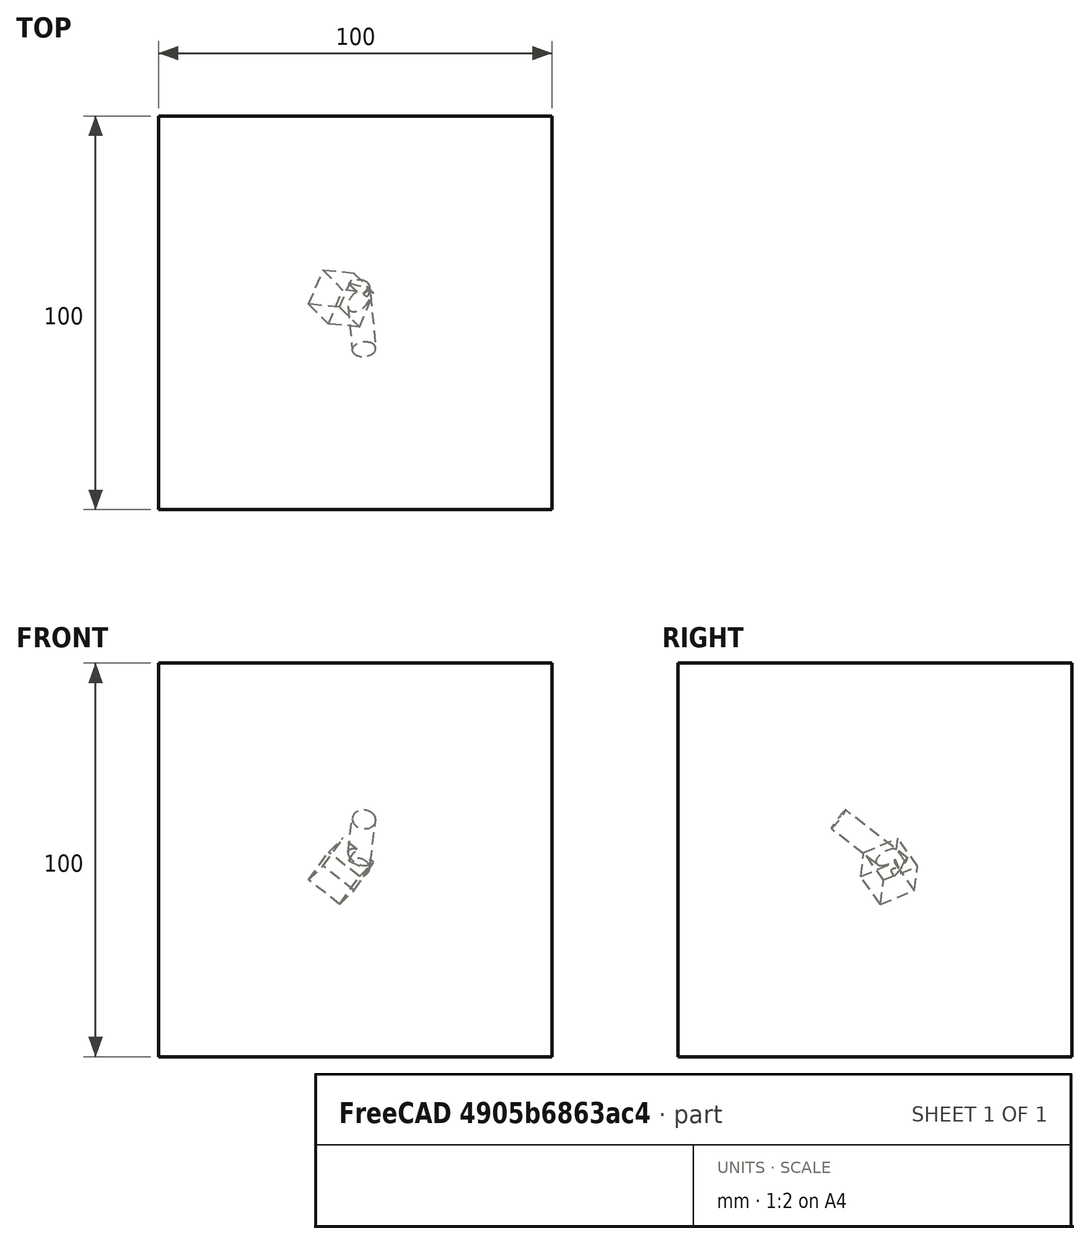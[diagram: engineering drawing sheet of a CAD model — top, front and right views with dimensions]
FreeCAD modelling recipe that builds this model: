
FCSTD DOCUMENT  (FreeCAD 1.0R39109 (Git))
Label: UnionTest
License: All rights reserved
objects: App::DocumentObjectGroupPython×1251, Part::FeaturePython×3, App::Part×2, Part::Fuse×1
note: 4 computed .brp shape members not serialized (recipe doc carries the construction recipe); baked Part::Feature solids carry a one-line shape summary decoded from their .brp

FEATURE [App::DocumentObjectGroupPython] HALFPI  # scripted group (container) (typed FeaturePython)
  name = HALFPI
  value = pi/2.
FEATURE [App::DocumentObjectGroupPython] PI  # scripted group (container) (typed FeaturePython)
  name = PI
  value = 1.*pi
FEATURE [App::DocumentObjectGroupPython] TWOPI  # scripted group (container) (typed FeaturePython)
  name = TWOPI
  value = 2.*pi
FEATURE [App::DocumentObjectGroupPython] Constants  # scripted group (container) (typed FeaturePython)
  Group = -> [HALFPI,PI,TWOPI]
FEATURE [App::DocumentObjectGroupPython] Variables  # scripted group (container) (typed FeaturePython)
FEATURE [App::DocumentObjectGroupPython] Quantities  # scripted group (container) (typed FeaturePython)
FEATURE [App::DocumentObjectGroupPython] Isotopes  # scripted group (container) (typed FeaturePython)
FEATURE [App::DocumentObjectGroupPython] Elements  # scripted group (container) (typed FeaturePython)
FEATURE [App::DocumentObjectGroupPython] Matrix  # scripted group (container) (typed FeaturePython)
FEATURE [App::DocumentObjectGroupPython] Surfaces  # scripted group (container) (typed FeaturePython)
FEATURE [App::DocumentObjectGroupPython] Opticals  # scripted group (container) (typed FeaturePython)
  Group = -> [Matrix,Surfaces]
FEATURE [App::DocumentObjectGroupPython] G4Isotopes  # scripted group (container) (typed FeaturePython)
FEATURE [App::DocumentObjectGroupPython] H_element  # scripted group (container) (typed FeaturePython)
  Z = 1
  atom_value = 1.008
  formula = H
  name = H_element
FEATURE [App::DocumentObjectGroupPython] He_element  # scripted group (container) (typed FeaturePython)
  Z = 2
  atom_value = 4.0026
  formula = He
  name = He_element
FEATURE [App::DocumentObjectGroupPython] Li_element  # scripted group (container) (typed FeaturePython)
  Z = 3
  atom_value = 6.94
  formula = Li
  name = Li_element
FEATURE [App::DocumentObjectGroupPython] Be_element  # scripted group (container) (typed FeaturePython)
  Z = 4
  atom_value = 9.01218
  formula = Be
  name = Be_element
FEATURE [App::DocumentObjectGroupPython] B_element  # scripted group (container) (typed FeaturePython)
  Z = 5
  atom_value = 10.81
  formula = B
  name = B_element
FEATURE [App::DocumentObjectGroupPython] C_element  # scripted group (container) (typed FeaturePython)
  Z = 6
  atom_value = 12.011
  formula = C
  name = C_element
FEATURE [App::DocumentObjectGroupPython] N_element  # scripted group (container) (typed FeaturePython)
  Z = 7
  atom_value = 14.007
  formula = N
  name = N_element
FEATURE [App::DocumentObjectGroupPython] O_element  # scripted group (container) (typed FeaturePython)
  Z = 8
  atom_value = 15.999
  formula = O
  name = O_element
FEATURE [App::DocumentObjectGroupPython] F_element  # scripted group (container) (typed FeaturePython)
  Z = 9
  atom_value = 18.9984
  formula = F
  name = F_element
FEATURE [App::DocumentObjectGroupPython] Ne_element  # scripted group (container) (typed FeaturePython)
  Z = 10
  atom_value = 20.1797
  formula = Ne
  name = Ne_element
FEATURE [App::DocumentObjectGroupPython] Na_element  # scripted group (container) (typed FeaturePython)
  Z = 11
  atom_value = 22.9898
  formula = Na
  name = Na_element
FEATURE [App::DocumentObjectGroupPython] Mg_element  # scripted group (container) (typed FeaturePython)
  Z = 12
  atom_value = 24.305
  formula = Mg
  name = Mg_element
FEATURE [App::DocumentObjectGroupPython] Al_element  # scripted group (container) (typed FeaturePython)
  Z = 13
  atom_value = 26.9815
  formula = Al
  name = Al_element
FEATURE [App::DocumentObjectGroupPython] Si_element  # scripted group (container) (typed FeaturePython)
  Z = 14
  atom_value = 28.085
  formula = Si
  name = Si_element
FEATURE [App::DocumentObjectGroupPython] P_element  # scripted group (container) (typed FeaturePython)
  Z = 15
  atom_value = 30.9738
  formula = P
  name = P_element
FEATURE [App::DocumentObjectGroupPython] S_element  # scripted group (container) (typed FeaturePython)
  Z = 16
  atom_value = 32.06
  formula = S
  name = S_element
FEATURE [App::DocumentObjectGroupPython] Cl_element  # scripted group (container) (typed FeaturePython)
  Z = 17
  atom_value = 35.45
  formula = Cl
  name = Cl_element
FEATURE [App::DocumentObjectGroupPython] Ar_element  # scripted group (container) (typed FeaturePython)
  Z = 18
  atom_value = 39.95
  formula = Ar
  name = Ar_element
FEATURE [App::DocumentObjectGroupPython] K_element  # scripted group (container) (typed FeaturePython)
  Z = 19
  atom_value = 39.0983
  formula = K
  name = K_element
FEATURE [App::DocumentObjectGroupPython] Ca_element  # scripted group (container) (typed FeaturePython)
  Z = 20
  atom_value = 40.078
  formula = Ca
  name = Ca_element
FEATURE [App::DocumentObjectGroupPython] Sc_element  # scripted group (container) (typed FeaturePython)
  Z = 21
  atom_value = 44.9559
  formula = Sc
  name = Sc_element
FEATURE [App::DocumentObjectGroupPython] Ti_element  # scripted group (container) (typed FeaturePython)
  Z = 22
  atom_value = 47.867
  formula = Ti
  name = Ti_element
FEATURE [App::DocumentObjectGroupPython] V_element  # scripted group (container) (typed FeaturePython)
  Z = 23
  atom_value = 50.9415
  formula = V
  name = V_element
FEATURE [App::DocumentObjectGroupPython] Cr_element  # scripted group (container) (typed FeaturePython)
  Z = 24
  atom_value = 51.9961
  formula = Cr
  name = Cr_element
FEATURE [App::DocumentObjectGroupPython] Mn_element  # scripted group (container) (typed FeaturePython)
  Z = 25
  atom_value = 54.938
  formula = Mn
  name = Mn_element
FEATURE [App::DocumentObjectGroupPython] Fe_element  # scripted group (container) (typed FeaturePython)
  Z = 26
  atom_value = 55.845
  formula = Fe
  name = Fe_element
FEATURE [App::DocumentObjectGroupPython] Co_element  # scripted group (container) (typed FeaturePython)
  Z = 27
  atom_value = 58.9332
  formula = Co
  name = Co_element
FEATURE [App::DocumentObjectGroupPython] Ni_element  # scripted group (container) (typed FeaturePython)
  Z = 28
  atom_value = 58.6934
  formula = Ni
  name = Ni_element
FEATURE [App::DocumentObjectGroupPython] Cu_element  # scripted group (container) (typed FeaturePython)
  Z = 29
  atom_value = 63.546
  formula = Cu
  name = Cu_element
FEATURE [App::DocumentObjectGroupPython] Zn_element  # scripted group (container) (typed FeaturePython)
  Z = 30
  atom_value = 65.38
  formula = Zn
  name = Zn_element
FEATURE [App::DocumentObjectGroupPython] Ga_element  # scripted group (container) (typed FeaturePython)
  Z = 31
  atom_value = 69.723
  formula = Ga
  name = Ga_element
FEATURE [App::DocumentObjectGroupPython] Ge_element  # scripted group (container) (typed FeaturePython)
  Z = 32
  atom_value = 72.63
  formula = Ge
  name = Ge_element
FEATURE [App::DocumentObjectGroupPython] As_element  # scripted group (container) (typed FeaturePython)
  Z = 33
  atom_value = 74.9216
  formula = As
  name = As_element
FEATURE [App::DocumentObjectGroupPython] Se_element  # scripted group (container) (typed FeaturePython)
  Z = 34
  atom_value = 78.971
  formula = Se
  name = Se_element
FEATURE [App::DocumentObjectGroupPython] Br_element  # scripted group (container) (typed FeaturePython)
  Z = 35
  atom_value = 79.904
  formula = Br
  name = Br_element
FEATURE [App::DocumentObjectGroupPython] Kr_element  # scripted group (container) (typed FeaturePython)
  Z = 36
  atom_value = 83.798
  formula = Kr
  name = Kr_element
FEATURE [App::DocumentObjectGroupPython] Rb_element  # scripted group (container) (typed FeaturePython)
  Z = 37
  atom_value = 85.4678
  formula = Rb
  name = Rb_element
FEATURE [App::DocumentObjectGroupPython] Sr_element  # scripted group (container) (typed FeaturePython)
  Z = 38
  atom_value = 87.62
  formula = Sr
  name = Sr_element
FEATURE [App::DocumentObjectGroupPython] Y_element  # scripted group (container) (typed FeaturePython)
  Z = 39
  atom_value = 88.9058
  formula = Y
  name = Y_element
FEATURE [App::DocumentObjectGroupPython] Zr_element  # scripted group (container) (typed FeaturePython)
  Z = 40
  atom_value = 91.224
  formula = Zr
  name = Zr_element
FEATURE [App::DocumentObjectGroupPython] Nb_element  # scripted group (container) (typed FeaturePython)
  Z = 41
  atom_value = 92.9064
  formula = Nb
  name = Nb_element
FEATURE [App::DocumentObjectGroupPython] Mo_element  # scripted group (container) (typed FeaturePython)
  Z = 42
  atom_value = 95.95
  formula = Mo
  name = Mo_element
FEATURE [App::DocumentObjectGroupPython] Tc_element  # scripted group (container) (typed FeaturePython)
  Z = 43
  atom_value = 97
  formula = Tc
  name = Tc_element
FEATURE [App::DocumentObjectGroupPython] Ru_element  # scripted group (container) (typed FeaturePython)
  Z = 44
  atom_value = 101.07
  formula = Ru
  name = Ru_element
FEATURE [App::DocumentObjectGroupPython] Rh_element  # scripted group (container) (typed FeaturePython)
  Z = 45
  atom_value = 102.905
  formula = Rh
  name = Rh_element
FEATURE [App::DocumentObjectGroupPython] Pd_element  # scripted group (container) (typed FeaturePython)
  Z = 46
  atom_value = 106.42
  formula = Pd
  name = Pd_element
FEATURE [App::DocumentObjectGroupPython] Ag_element  # scripted group (container) (typed FeaturePython)
  Z = 47
  atom_value = 107.868
  formula = Ag
  name = Ag_element
FEATURE [App::DocumentObjectGroupPython] Cd_element  # scripted group (container) (typed FeaturePython)
  Z = 48
  atom_value = 112.414
  formula = Cd
  name = Cd_element
FEATURE [App::DocumentObjectGroupPython] In_element  # scripted group (container) (typed FeaturePython)
  Z = 49
  atom_value = 114.818
  formula = In
  name = In_element
FEATURE [App::DocumentObjectGroupPython] Sn_element  # scripted group (container) (typed FeaturePython)
  Z = 50
  atom_value = 118.71
  formula = Sn
  name = Sn_element
FEATURE [App::DocumentObjectGroupPython] Sb_element  # scripted group (container) (typed FeaturePython)
  Z = 51
  atom_value = 121.76
  formula = Sb
  name = Sb_element
FEATURE [App::DocumentObjectGroupPython] Te_element  # scripted group (container) (typed FeaturePython)
  Z = 52
  atom_value = 127.6
  formula = Te
  name = Te_element
FEATURE [App::DocumentObjectGroupPython] I_element  # scripted group (container) (typed FeaturePython)
  Z = 53
  atom_value = 126.904
  formula = I
  name = I_element
FEATURE [App::DocumentObjectGroupPython] Xe_element  # scripted group (container) (typed FeaturePython)
  Z = 54
  atom_value = 131.293
  formula = Xe
  name = Xe_element
FEATURE [App::DocumentObjectGroupPython] Cs_element  # scripted group (container) (typed FeaturePython)
  Z = 55
  atom_value = 132.905
  formula = Cs
  name = Cs_element
FEATURE [App::DocumentObjectGroupPython] Ba_element  # scripted group (container) (typed FeaturePython)
  Z = 56
  atom_value = 137.327
  formula = Ba
  name = Ba_element
FEATURE [App::DocumentObjectGroupPython] La_element  # scripted group (container) (typed FeaturePython)
  Z = 57
  atom_value = 138.905
  formula = La
  name = La_element
FEATURE [App::DocumentObjectGroupPython] Ce_element  # scripted group (container) (typed FeaturePython)
  Z = 58
  atom_value = 140.116
  formula = Ce
  name = Ce_element
FEATURE [App::DocumentObjectGroupPython] Pr_element  # scripted group (container) (typed FeaturePython)
  Z = 59
  atom_value = 140.908
  formula = Pr
  name = Pr_element
FEATURE [App::DocumentObjectGroupPython] Nd_element  # scripted group (container) (typed FeaturePython)
  Z = 60
  atom_value = 144.242
  formula = Nd
  name = Nd_element
FEATURE [App::DocumentObjectGroupPython] Pm_element  # scripted group (container) (typed FeaturePython)
  Z = 61
  atom_value = 145
  formula = Pm
  name = Pm_element
FEATURE [App::DocumentObjectGroupPython] Sm_element  # scripted group (container) (typed FeaturePython)
  Z = 62
  atom_value = 150.36
  formula = Sm
  name = Sm_element
FEATURE [App::DocumentObjectGroupPython] Eu_element  # scripted group (container) (typed FeaturePython)
  Z = 63
  atom_value = 151.964
  formula = Eu
  name = Eu_element
FEATURE [App::DocumentObjectGroupPython] Gd_element  # scripted group (container) (typed FeaturePython)
  Z = 64
  atom_value = 157.25
  formula = Gd
  name = Gd_element
FEATURE [App::DocumentObjectGroupPython] Tb_element  # scripted group (container) (typed FeaturePython)
  Z = 65
  atom_value = 158.925
  formula = Tb
  name = Tb_element
FEATURE [App::DocumentObjectGroupPython] Dy_element  # scripted group (container) (typed FeaturePython)
  Z = 66
  atom_value = 162.5
  formula = Dy
  name = Dy_element
FEATURE [App::DocumentObjectGroupPython] Ho_element  # scripted group (container) (typed FeaturePython)
  Z = 67
  atom_value = 164.93
  formula = Ho
  name = Ho_element
FEATURE [App::DocumentObjectGroupPython] Er_element  # scripted group (container) (typed FeaturePython)
  Z = 68
  atom_value = 167.259
  formula = Er
  name = Er_element
FEATURE [App::DocumentObjectGroupPython] Tm_element  # scripted group (container) (typed FeaturePython)
  Z = 69
  atom_value = 168.934
  formula = Tm
  name = Tm_element
FEATURE [App::DocumentObjectGroupPython] Yb_element  # scripted group (container) (typed FeaturePython)
  Z = 70
  atom_value = 173.045
  formula = Yb
  name = Yb_element
FEATURE [App::DocumentObjectGroupPython] Lu_element  # scripted group (container) (typed FeaturePython)
  Z = 71
  atom_value = 174.967
  formula = Lu
  name = Lu_element
FEATURE [App::DocumentObjectGroupPython] Hf_element  # scripted group (container) (typed FeaturePython)
  Z = 72
  atom_value = 178.49
  formula = Hf
  name = Hf_element
FEATURE [App::DocumentObjectGroupPython] Ta_element  # scripted group (container) (typed FeaturePython)
  Z = 73
  atom_value = 180.948
  formula = Ta
  name = Ta_element
FEATURE [App::DocumentObjectGroupPython] W_element  # scripted group (container) (typed FeaturePython)
  Z = 74
  atom_value = 183.84
  formula = W
  name = W_element
FEATURE [App::DocumentObjectGroupPython] Re_element  # scripted group (container) (typed FeaturePython)
  Z = 75
  atom_value = 186.207
  formula = Re
  name = Re_element
FEATURE [App::DocumentObjectGroupPython] Os_element  # scripted group (container) (typed FeaturePython)
  Z = 76
  atom_value = 190.23
  formula = Os
  name = Os_element
FEATURE [App::DocumentObjectGroupPython] Ir_element  # scripted group (container) (typed FeaturePython)
  Z = 77
  atom_value = 192.217
  formula = Ir
  name = Ir_element
FEATURE [App::DocumentObjectGroupPython] Pt_element  # scripted group (container) (typed FeaturePython)
  Z = 78
  atom_value = 195.084
  formula = Pt
  name = Pt_element
FEATURE [App::DocumentObjectGroupPython] Au_element  # scripted group (container) (typed FeaturePython)
  Z = 79
  atom_value = 196.967
  formula = Au
  name = Au_element
FEATURE [App::DocumentObjectGroupPython] Hg_element  # scripted group (container) (typed FeaturePython)
  Z = 80
  atom_value = 200.592
  formula = Hg
  name = Hg_element
FEATURE [App::DocumentObjectGroupPython] Tl_element  # scripted group (container) (typed FeaturePython)
  Z = 81
  atom_value = 204.38
  formula = Tl
  name = Tl_element
FEATURE [App::DocumentObjectGroupPython] Pb_element  # scripted group (container) (typed FeaturePython)
  Z = 82
  atom_value = 207.2
  formula = Pb
  name = Pb_element
FEATURE [App::DocumentObjectGroupPython] Bi_element  # scripted group (container) (typed FeaturePython)
  Z = 83
  atom_value = 208.98
  formula = Bi
  name = Bi_element
FEATURE [App::DocumentObjectGroupPython] Po_element  # scripted group (container) (typed FeaturePython)
  Z = 84
  atom_value = 209
  formula = Po
  name = Po_element
FEATURE [App::DocumentObjectGroupPython] At_element  # scripted group (container) (typed FeaturePython)
  Z = 85
  atom_value = 210
  formula = At
  name = At_element
FEATURE [App::DocumentObjectGroupPython] Rn_element  # scripted group (container) (typed FeaturePython)
  Z = 86
  atom_value = 222
  formula = Rn
  name = Rn_element
FEATURE [App::DocumentObjectGroupPython] Fr_element  # scripted group (container) (typed FeaturePython)
  Z = 87
  atom_value = 223
  formula = Fr
  name = Fr_element
FEATURE [App::DocumentObjectGroupPython] Ra_element  # scripted group (container) (typed FeaturePython)
  Z = 88
  atom_value = 226
  formula = Ra
  name = Ra_element
FEATURE [App::DocumentObjectGroupPython] Ac_element  # scripted group (container) (typed FeaturePython)
  Z = 89
  atom_value = 227
  formula = Ac
  name = Ac_element
FEATURE [App::DocumentObjectGroupPython] Th_element  # scripted group (container) (typed FeaturePython)
  Z = 90
  atom_value = 232.038
  formula = Th
  name = Th_element
FEATURE [App::DocumentObjectGroupPython] Pa_element  # scripted group (container) (typed FeaturePython)
  Z = 91
  atom_value = 231.036
  formula = Pa
  name = Pa_element
FEATURE [App::DocumentObjectGroupPython] U_element  # scripted group (container) (typed FeaturePython)
  Z = 92
  atom_value = 238.029
  formula = U
  name = U_element
FEATURE [App::DocumentObjectGroupPython] Np_element  # scripted group (container) (typed FeaturePython)
  Z = 93
  atom_value = 237
  formula = Np
  name = Np_element
FEATURE [App::DocumentObjectGroupPython] Pu_element  # scripted group (container) (typed FeaturePython)
  Z = 94
  atom_value = 244
  formula = Pu
  name = Pu_element
FEATURE [App::DocumentObjectGroupPython] Am_element  # scripted group (container) (typed FeaturePython)
  Z = 95
  atom_value = 243
  formula = Am
  name = Am_element
FEATURE [App::DocumentObjectGroupPython] Cm_element  # scripted group (container) (typed FeaturePython)
  Z = 96
  atom_value = 247
  formula = Cm
  name = Cm_element
FEATURE [App::DocumentObjectGroupPython] Bk_element  # scripted group (container) (typed FeaturePython)
  Z = 97
  atom_value = 247
  formula = Bk
  name = Bk_element
FEATURE [App::DocumentObjectGroupPython] Cf_element  # scripted group (container) (typed FeaturePython)
  Z = 98
  atom_value = 251
  formula = Cf
  name = Cf_element
FEATURE [App::DocumentObjectGroupPython] G4Elements  # scripted group (container) (typed FeaturePython)
  Group = -> [H_element,He_element,Li_element,Be_element,B_element,C_element,N_element,O_element,F_element,Ne_element,Na_element,Mg_element,Al_element,Si_element,P_element,S_element,Cl_element,Ar_element,K_element,Ca_element,Sc_element,Ti_element,V_element,Cr_element,Mn_element,Fe_element,Co_element,Ni_element,Cu_element,Zn_element,Ga_element,Ge_element,As_element,Se_element,Br_element,Kr_element,Rb_element,+61 more]
FEATURE [App::DocumentObjectGroupPython] H_element001  label="H_element : 0.101"  # scripted group (container) (typed FeaturePython)
  n = 0.101327
FEATURE [App::DocumentObjectGroupPython] C_element001  label="C_element : 0.775"  # scripted group (container) (typed FeaturePython)
  n = 0.7755
FEATURE [App::DocumentObjectGroupPython] N_element001  label="N_element : 0.035"  # scripted group (container) (typed FeaturePython)
  n = 0.035057
FEATURE [App::DocumentObjectGroupPython] O_element001  label="O_element : 0.052"  # scripted group (container) (typed FeaturePython)
  n = 0.0523159
FEATURE [App::DocumentObjectGroupPython] F_element001  label="F_element : 0.017"  # scripted group (container) (typed FeaturePython)
  n = 0.017422
FEATURE [App::DocumentObjectGroupPython] Ca_element001  label="Ca_element : 0.018"  # scripted group (container) (typed FeaturePython)
  n = 0.018378
FEATURE [App::DocumentObjectGroupPython] G4_A_150_TISSUE  label="G4_A-150_TISSUE"  # scripted group (container) (typed FeaturePython)
  Dunit = g/cm3
  Dvalue = 1.127
  Group = -> [H_element001,C_element001,N_element001,O_element001,F_element001,Ca_element001]
  conduct = 2
  density = 1
  expand = 3
  formula = G4_A-150_TISSUE
  name = G4_A-150_TISSUE
  specific = 4
FEATURE [App::DocumentObjectGroupPython] C_element002  label="C_element : 3"  # scripted group (container) (typed FeaturePython)
  n = 3
  ref = C_element
FEATURE [App::DocumentObjectGroupPython] H_element002  label="H_element : 6"  # scripted group (container) (typed FeaturePython)
  n = 6
  ref = H_element
FEATURE [App::DocumentObjectGroupPython] O_element002  label="O_element : 1"  # scripted group (container) (typed FeaturePython)
  n = 1
  ref = O_element
FEATURE [App::DocumentObjectGroupPython] G4_ACETONE  # scripted group (container) (typed FeaturePython)
  Dunit = g/cm3
  Dvalue = 0.7899
  Group = -> [C_element002,H_element002,O_element002]
  conduct = 2
  density = 1
  expand = 3
  formula = G4_ACETONE
  name = G4_ACETONE
  specific = 4
FEATURE [App::DocumentObjectGroupPython] C_element003  label="C_element : 2"  # scripted group (container) (typed FeaturePython)
  n = 2
  ref = C_element
FEATURE [App::DocumentObjectGroupPython] H_element003  label="H_element : 2"  # scripted group (container) (typed FeaturePython)
  n = 2
  ref = H_element
FEATURE [App::DocumentObjectGroupPython] G4_ACETYLENE  # scripted group (container) (typed FeaturePython)
  Dunit = g/cm3
  Dvalue = 0.0010967
  Group = -> [C_element003,H_element003]
  conduct = 2
  density = 1
  expand = 3
  formula = G4_ACETYLENE
  name = G4_ACETYLENE
  specific = 4
FEATURE [App::DocumentObjectGroupPython] C_element004  label="C_element : 5"  # scripted group (container) (typed FeaturePython)
  n = 5
  ref = C_element
FEATURE [App::DocumentObjectGroupPython] H_element004  label="H_element : 5"  # scripted group (container) (typed FeaturePython)
  n = 5
  ref = H_element
FEATURE [App::DocumentObjectGroupPython] N_element002  label="N_element : 5"  # scripted group (container) (typed FeaturePython)
  n = 5
  ref = N_element
FEATURE [App::DocumentObjectGroupPython] G4_ADENINE  # scripted group (container) (typed FeaturePython)
  Dunit = g/cm3
  Dvalue = 1.6
  Group = -> [C_element004,H_element004,N_element002]
  conduct = 2
  density = 1
  expand = 3
  formula = G4_ADENINE
  name = G4_ADENINE
  specific = 4
FEATURE [App::DocumentObjectGroupPython] H_element005  label="H_element : 0.114"  # scripted group (container) (typed FeaturePython)
  n = 0.114
FEATURE [App::DocumentObjectGroupPython] C_element005  label="C_element : 0.598"  # scripted group (container) (typed FeaturePython)
  n = 0.598
FEATURE [App::DocumentObjectGroupPython] N_element003  label="N_element : 0.007"  # scripted group (container) (typed FeaturePython)
  n = 0.007
FEATURE [App::DocumentObjectGroupPython] O_element003  label="O_element : 0.278"  # scripted group (container) (typed FeaturePython)
  n = 0.278
FEATURE [App::DocumentObjectGroupPython] Na_element001  label="Na_element : 0.001"  # scripted group (container) (typed FeaturePython)
  n = 0.001
FEATURE [App::DocumentObjectGroupPython] S_element001  label="S_element : 0.001"  # scripted group (container) (typed FeaturePython)
  n = 0.001
FEATURE [App::DocumentObjectGroupPython] Cl_element001  label="Cl_element : 0.001"  # scripted group (container) (typed FeaturePython)
  n = 0.001
FEATURE [App::DocumentObjectGroupPython] G4_ADIPOSE_TISSUE_ICRP  # scripted group (container) (typed FeaturePython)
  Dunit = g/cm3
  Dvalue = 0.95
  Group = -> [H_element005,C_element005,N_element003,O_element003,Na_element001,S_element001,Cl_element001]
  conduct = 2
  density = 1
  expand = 3
  formula = G4_ADIPOSE_TISSUE_ICRP
  name = G4_ADIPOSE_TISSUE_ICRP
  specific = 4
FEATURE [App::DocumentObjectGroupPython] C_element006  label="C_element : 0.000"  # scripted group (container) (typed FeaturePython)
  n = 0.000124
FEATURE [App::DocumentObjectGroupPython] N_element004  label="N_element : 0.755"  # scripted group (container) (typed FeaturePython)
  n = 0.755268
FEATURE [App::DocumentObjectGroupPython] O_element004  label="O_element : 0.232"  # scripted group (container) (typed FeaturePython)
  n = 0.231781
FEATURE [App::DocumentObjectGroupPython] Ar_element001  label="Ar_element : 0.013"  # scripted group (container) (typed FeaturePython)
  n = 0.012827
FEATURE [App::DocumentObjectGroupPython] G4_AIR  # scripted group (container) (typed FeaturePython)
  Dunit = g/cm3
  Dvalue = 0.00120479
  Group = -> [C_element006,N_element004,O_element004,Ar_element001]
  conduct = 2
  density = 1
  expand = 3
  formula = G4_AIR
  name = G4_AIR
  specific = 4
FEATURE [App::DocumentObjectGroupPython] C_element007  label="C_element : 006"  # scripted group (container) (typed FeaturePython)
  n = 3
  ref = C_element
FEATURE [App::DocumentObjectGroupPython] H_element006  label="H_element : 7"  # scripted group (container) (typed FeaturePython)
  n = 7
  ref = H_element
FEATURE [App::DocumentObjectGroupPython] N_element005  label="N_element : 1"  # scripted group (container) (typed FeaturePython)
  n = 1
  ref = N_element
FEATURE [App::DocumentObjectGroupPython] O_element005  label="O_element : 2"  # scripted group (container) (typed FeaturePython)
  n = 2
  ref = O_element
FEATURE [App::DocumentObjectGroupPython] G4_ALANINE  # scripted group (container) (typed FeaturePython)
  Dunit = g/cm3
  Dvalue = 1.42
  Group = -> [C_element007,H_element006,N_element005,O_element005]
  conduct = 2
  density = 1
  expand = 3
  formula = G4_ALANINE
  name = G4_ALANINE
  specific = 4
FEATURE [App::DocumentObjectGroupPython] Al_element001  label="Al_element : 2"  # scripted group (container) (typed FeaturePython)
  n = 2
  ref = Al_element
FEATURE [App::DocumentObjectGroupPython] O_element006  label="O_element : 3"  # scripted group (container) (typed FeaturePython)
  n = 3
  ref = O_element
FEATURE [App::DocumentObjectGroupPython] G4_ALUMINUM_OXIDE  # scripted group (container) (typed FeaturePython)
  Dunit = g/cm3
  Dvalue = 3.97
  Group = -> [Al_element001,O_element006]
  conduct = 2
  density = 1
  expand = 3
  formula = G4_ALUMINUM_OXIDE
  name = G4_ALUMINUM_OXIDE
  specific = 4
FEATURE [App::DocumentObjectGroupPython] H_element007  label="H_element : 0.106"  # scripted group (container) (typed FeaturePython)
  n = 0.10593
FEATURE [App::DocumentObjectGroupPython] C_element008  label="C_element : 0.789"  # scripted group (container) (typed FeaturePython)
  n = 0.788974
FEATURE [App::DocumentObjectGroupPython] O_element007  label="O_element : 0.105"  # scripted group (container) (typed FeaturePython)
  n = 0.105096
FEATURE [App::DocumentObjectGroupPython] G4_AMBER  # scripted group (container) (typed FeaturePython)
  Dunit = g/cm3
  Dvalue = 1.1
  Group = -> [H_element007,C_element008,O_element007]
  conduct = 2
  density = 1
  expand = 3
  formula = G4_AMBER
  name = G4_AMBER
  specific = 4
FEATURE [App::DocumentObjectGroupPython] N_element006  label="N_element : 006"  # scripted group (container) (typed FeaturePython)
  n = 1
  ref = N_element
FEATURE [App::DocumentObjectGroupPython] H_element008  label="H_element : 3"  # scripted group (container) (typed FeaturePython)
  n = 3
  ref = H_element
FEATURE [App::DocumentObjectGroupPython] G4_AMMONIA  # scripted group (container) (typed FeaturePython)
  Dunit = g/cm3
  Dvalue = 0.000826019
  Group = -> [N_element006,H_element008]
  conduct = 2
  density = 1
  expand = 3
  formula = G4_AMMONIA
  name = G4_AMMONIA
  specific = 4
FEATURE [App::DocumentObjectGroupPython] C_element009  label="C_element : 6"  # scripted group (container) (typed FeaturePython)
  n = 6
  ref = C_element
FEATURE [App::DocumentObjectGroupPython] H_element009  label="H_element : 008"  # scripted group (container) (typed FeaturePython)
  n = 7
  ref = H_element
FEATURE [App::DocumentObjectGroupPython] N_element007  label="N_element : 007"  # scripted group (container) (typed FeaturePython)
  n = 1
  ref = N_element
FEATURE [App::DocumentObjectGroupPython] G4_ANILINE  # scripted group (container) (typed FeaturePython)
  Dunit = g/cm3
  Dvalue = 1.0235
  Group = -> [C_element009,H_element009,N_element007]
  conduct = 2
  density = 1
  expand = 3
  formula = G4_ANILINE
  name = G4_ANILINE
  specific = 4
FEATURE [App::DocumentObjectGroupPython] C_element010  label="C_element : 14"  # scripted group (container) (typed FeaturePython)
  n = 14
  ref = C_element
FEATURE [App::DocumentObjectGroupPython] H_element010  label="H_element : 10"  # scripted group (container) (typed FeaturePython)
  n = 10
  ref = H_element
FEATURE [App::DocumentObjectGroupPython] G4_ANTHRACENE  # scripted group (container) (typed FeaturePython)
  Dunit = g/cm3
  Dvalue = 1.283
  Group = -> [C_element010,H_element010]
  conduct = 2
  density = 1
  expand = 3
  formula = G4_ANTHRACENE
  name = G4_ANTHRACENE
  specific = 4
FEATURE [App::DocumentObjectGroupPython] H_element011  label="H_element : 0.065"  # scripted group (container) (typed FeaturePython)
  n = 0.0654709
FEATURE [App::DocumentObjectGroupPython] C_element011  label="C_element : 0.537"  # scripted group (container) (typed FeaturePython)
  n = 0.536944
FEATURE [App::DocumentObjectGroupPython] N_element008  label="N_element : 0.021"  # scripted group (container) (typed FeaturePython)
  n = 0.0215
FEATURE [App::DocumentObjectGroupPython] O_element008  label="O_element : 0.032"  # scripted group (container) (typed FeaturePython)
  n = 0.032085
FEATURE [App::DocumentObjectGroupPython] F_element002  label="F_element : 0.167"  # scripted group (container) (typed FeaturePython)
  n = 0.167411
FEATURE [App::DocumentObjectGroupPython] Ca_element002  label="Ca_element : 0.177"  # scripted group (container) (typed FeaturePython)
  n = 0.176589
FEATURE [App::DocumentObjectGroupPython] G4_B_100_BONE  label="G4_B-100_BONE"  # scripted group (container) (typed FeaturePython)
  Dunit = g/cm3
  Dvalue = 1.45
  Group = -> [H_element011,C_element011,N_element008,O_element008,F_element002,Ca_element002]
  conduct = 2
  density = 1
  expand = 3
  formula = G4_B-100_BONE
  name = G4_B-100_BONE
  specific = 4
FEATURE [App::DocumentObjectGroupPython] H_element012  label="H_element : 0.057"  # scripted group (container) (typed FeaturePython)
  n = 0.057441
FEATURE [App::DocumentObjectGroupPython] C_element012  label="C_element : 0.790"  # scripted group (container) (typed FeaturePython)
  n = 0.774591
FEATURE [App::DocumentObjectGroupPython] O_element009  label="O_element : 0.168"  # scripted group (container) (typed FeaturePython)
  n = 0.167968
FEATURE [App::DocumentObjectGroupPython] G4_BAKELITE  # scripted group (container) (typed FeaturePython)
  Dunit = g/cm3
  Dvalue = 1.25
  Group = -> [H_element012,C_element012,O_element009]
  conduct = 2
  density = 1
  expand = 3
  formula = G4_BAKELITE
  name = G4_BAKELITE
  specific = 4
FEATURE [App::DocumentObjectGroupPython] Ba_element001  label="Ba_element : 1"  # scripted group (container) (typed FeaturePython)
  n = 1
  ref = Ba_element
FEATURE [App::DocumentObjectGroupPython] F_element003  label="F_element : 2"  # scripted group (container) (typed FeaturePython)
  n = 2
  ref = F_element
FEATURE [App::DocumentObjectGroupPython] G4_BARIUM_FLUORIDE  # scripted group (container) (typed FeaturePython)
  Dunit = g/cm3
  Dvalue = 4.89
  Group = -> [Ba_element001,F_element003]
  conduct = 2
  density = 1
  expand = 3
  formula = G4_BARIUM_FLUORIDE
  name = G4_BARIUM_FLUORIDE
  specific = 4
FEATURE [App::DocumentObjectGroupPython] Ba_element002  label="Ba_element : 002"  # scripted group (container) (typed FeaturePython)
  n = 1
  ref = Ba_element
FEATURE [App::DocumentObjectGroupPython] S_element002  label="S_element : 1"  # scripted group (container) (typed FeaturePython)
  n = 1
  ref = S_element
FEATURE [App::DocumentObjectGroupPython] O_element010  label="O_element : 4"  # scripted group (container) (typed FeaturePython)
  n = 4
  ref = O_element
FEATURE [App::DocumentObjectGroupPython] G4_BARIUM_SULFATE  # scripted group (container) (typed FeaturePython)
  Dunit = g/cm3
  Dvalue = 4.5
  Group = -> [Ba_element002,S_element002,O_element010]
  conduct = 2
  density = 1
  expand = 3
  formula = G4_BARIUM_SULFATE
  name = G4_BARIUM_SULFATE
  specific = 4
FEATURE [App::DocumentObjectGroupPython] C_element013  label="C_element : 007"  # scripted group (container) (typed FeaturePython)
  n = 6
  ref = C_element
FEATURE [App::DocumentObjectGroupPython] H_element013  label="H_element : 009"  # scripted group (container) (typed FeaturePython)
  n = 6
  ref = H_element
FEATURE [App::DocumentObjectGroupPython] G4_BENZENE  # scripted group (container) (typed FeaturePython)
  Dunit = g/cm3
  Dvalue = 0.87865
  Group = -> [C_element013,H_element013]
  conduct = 2
  density = 1
  expand = 3
  formula = G4_BENZENE
  name = G4_BENZENE
  specific = 4
FEATURE [App::DocumentObjectGroupPython] Be_element001  label="Be_element : 1"  # scripted group (container) (typed FeaturePython)
  n = 1
  ref = Be_element
FEATURE [App::DocumentObjectGroupPython] O_element011  label="O_element : 005"  # scripted group (container) (typed FeaturePython)
  n = 1
  ref = O_element
FEATURE [App::DocumentObjectGroupPython] G4_BERYLLIUM_OXIDE  # scripted group (container) (typed FeaturePython)
  Dunit = g/cm3
  Dvalue = 3.01
  Group = -> [Be_element001,O_element011]
  conduct = 2
  density = 1
  expand = 3
  formula = G4_BERYLLIUM_OXIDE
  name = G4_BERYLLIUM_OXIDE
  specific = 4
FEATURE [App::DocumentObjectGroupPython] Bi_element001  label="Bi_element : 4"  # scripted group (container) (typed FeaturePython)
  n = 4
  ref = Bi_element
FEATURE [App::DocumentObjectGroupPython] Ge_element001  label="Ge_element : 3"  # scripted group (container) (typed FeaturePython)
  n = 3
  ref = Ge_element
FEATURE [App::DocumentObjectGroupPython] O_element012  label="O_element : 12"  # scripted group (container) (typed FeaturePython)
  n = 12
  ref = O_element
FEATURE [App::DocumentObjectGroupPython] G4_BGO  # scripted group (container) (typed FeaturePython)
  Dunit = g/cm3
  Dvalue = 7.13
  Group = -> [Bi_element001,Ge_element001,O_element012]
  conduct = 2
  density = 1
  expand = 3
  formula = G4_BGO
  name = G4_BGO
  specific = 4
FEATURE [App::DocumentObjectGroupPython] H_element014  label="H_element : 0.102"  # scripted group (container) (typed FeaturePython)
  n = 0.102
FEATURE [App::DocumentObjectGroupPython] C_element014  label="C_element : 0.110"  # scripted group (container) (typed FeaturePython)
  n = 0.11
FEATURE [App::DocumentObjectGroupPython] N_element009  label="N_element : 0.033"  # scripted group (container) (typed FeaturePython)
  n = 0.033
FEATURE [App::DocumentObjectGroupPython] O_element013  label="O_element : 0.745"  # scripted group (container) (typed FeaturePython)
  n = 0.745
FEATURE [App::DocumentObjectGroupPython] Na_element002  label="Na_element : 0.002"  # scripted group (container) (typed FeaturePython)
  n = 0.001
FEATURE [App::DocumentObjectGroupPython] P_element001  label="P_element : 0.001"  # scripted group (container) (typed FeaturePython)
  n = 0.001
FEATURE [App::DocumentObjectGroupPython] S_element003  label="S_element : 0.002"  # scripted group (container) (typed FeaturePython)
  n = 0.002
FEATURE [App::DocumentObjectGroupPython] Cl_element002  label="Cl_element : 0.003"  # scripted group (container) (typed FeaturePython)
  n = 0.003
FEATURE [App::DocumentObjectGroupPython] K_element001  label="K_element : 0.002"  # scripted group (container) (typed FeaturePython)
  n = 0.002
FEATURE [App::DocumentObjectGroupPython] Fe_element001  label="Fe_element : 0.001"  # scripted group (container) (typed FeaturePython)
  n = 0.001
FEATURE [App::DocumentObjectGroupPython] G4_BLOOD_ICRP  # scripted group (container) (typed FeaturePython)
  Dunit = g/cm3
  Dvalue = 1.06
  Group = -> [H_element014,C_element014,N_element009,O_element013,Na_element002,P_element001,S_element003,Cl_element002,K_element001,Fe_element001]
  conduct = 2
  density = 1
  expand = 3
  formula = G4_BLOOD_ICRP
  name = G4_BLOOD_ICRP
  specific = 4
FEATURE [App::DocumentObjectGroupPython] H_element015  label="H_element : 0.064"  # scripted group (container) (typed FeaturePython)
  n = 0.064
FEATURE [App::DocumentObjectGroupPython] C_element015  label="C_element : 0.278"  # scripted group (container) (typed FeaturePython)
  n = 0.278
FEATURE [App::DocumentObjectGroupPython] N_element010  label="N_element : 0.027"  # scripted group (container) (typed FeaturePython)
  n = 0.027
FEATURE [App::DocumentObjectGroupPython] O_element014  label="O_element : 0.410"  # scripted group (container) (typed FeaturePython)
  n = 0.41
FEATURE [App::DocumentObjectGroupPython] Mg_element001  label="Mg_element : 0.002"  # scripted group (container) (typed FeaturePython)
  n = 0.002
FEATURE [App::DocumentObjectGroupPython] P_element002  label="P_element : 0.070"  # scripted group (container) (typed FeaturePython)
  n = 0.07
FEATURE [App::DocumentObjectGroupPython] S_element004  label="S_element : 0.003"  # scripted group (container) (typed FeaturePython)
  n = 0.002
FEATURE [App::DocumentObjectGroupPython] Ca_element003  label="Ca_element : 0.147"  # scripted group (container) (typed FeaturePython)
  n = 0.147
FEATURE [App::DocumentObjectGroupPython] G4_BONE_COMPACT_ICRU  # scripted group (container) (typed FeaturePython)
  Dunit = g/cm3
  Dvalue = 1.85
  Group = -> [H_element015,C_element015,N_element010,O_element014,Mg_element001,P_element002,S_element004,Ca_element003]
  conduct = 2
  density = 1
  expand = 3
  formula = G4_BONE_COMPACT_ICRU
  name = G4_BONE_COMPACT_ICRU
  specific = 4
FEATURE [App::DocumentObjectGroupPython] H_element016  label="H_element : 0.034"  # scripted group (container) (typed FeaturePython)
  n = 0.034
FEATURE [App::DocumentObjectGroupPython] C_element016  label="C_element : 0.155"  # scripted group (container) (typed FeaturePython)
  n = 0.155
FEATURE [App::DocumentObjectGroupPython] N_element011  label="N_element : 0.042"  # scripted group (container) (typed FeaturePython)
  n = 0.042
FEATURE [App::DocumentObjectGroupPython] O_element015  label="O_element : 0.435"  # scripted group (container) (typed FeaturePython)
  n = 0.435
FEATURE [App::DocumentObjectGroupPython] Na_element003  label="Na_element : 0.003"  # scripted group (container) (typed FeaturePython)
  n = 0.001
FEATURE [App::DocumentObjectGroupPython] Mg_element002  label="Mg_element : 0.003"  # scripted group (container) (typed FeaturePython)
  n = 0.002
FEATURE [App::DocumentObjectGroupPython] P_element003  label="P_element : 0.103"  # scripted group (container) (typed FeaturePython)
  n = 0.103
FEATURE [App::DocumentObjectGroupPython] S_element005  label="S_element : 0.004"  # scripted group (container) (typed FeaturePython)
  n = 0.003
FEATURE [App::DocumentObjectGroupPython] Ca_element004  label="Ca_element : 0.225"  # scripted group (container) (typed FeaturePython)
  n = 0.225
FEATURE [App::DocumentObjectGroupPython] G4_BONE_CORTICAL_ICRP  # scripted group (container) (typed FeaturePython)
  Dunit = g/cm3
  Dvalue = 1.92
  Group = -> [H_element016,C_element016,N_element011,O_element015,Na_element003,Mg_element002,P_element003,S_element005,Ca_element004]
  conduct = 2
  density = 1
  expand = 3
  formula = G4_BONE_CORTICAL_ICRP
  name = G4_BONE_CORTICAL_ICRP
  specific = 4
FEATURE [App::DocumentObjectGroupPython] B_element001  label="B_element : 4"  # scripted group (container) (typed FeaturePython)
  n = 4
  ref = B_element
FEATURE [App::DocumentObjectGroupPython] C_element017  label="C_element : 1"  # scripted group (container) (typed FeaturePython)
  n = 1
  ref = C_element
FEATURE [App::DocumentObjectGroupPython] G4_BORON_CARBIDE  # scripted group (container) (typed FeaturePython)
  Dunit = g/cm3
  Dvalue = 2.52
  Group = -> [B_element001,C_element017]
  conduct = 2
  density = 1
  expand = 3
  formula = G4_BORON_CARBIDE
  name = G4_BORON_CARBIDE
  specific = 4
FEATURE [App::DocumentObjectGroupPython] B_element002  label="B_element : 2"  # scripted group (container) (typed FeaturePython)
  n = 2
  ref = B_element
FEATURE [App::DocumentObjectGroupPython] O_element016  label="O_element : 006"  # scripted group (container) (typed FeaturePython)
  n = 3
  ref = O_element
FEATURE [App::DocumentObjectGroupPython] G4_BORON_OXIDE  # scripted group (container) (typed FeaturePython)
  Dunit = g/cm3
  Dvalue = 1.812
  Group = -> [B_element002,O_element016]
  conduct = 2
  density = 1
  expand = 3
  formula = G4_BORON_OXIDE
  name = G4_BORON_OXIDE
  specific = 4
FEATURE [App::DocumentObjectGroupPython] H_element017  label="H_element : 0.107"  # scripted group (container) (typed FeaturePython)
  n = 0.107
FEATURE [App::DocumentObjectGroupPython] C_element018  label="C_element : 0.145"  # scripted group (container) (typed FeaturePython)
  n = 0.145
FEATURE [App::DocumentObjectGroupPython] N_element012  label="N_element : 0.022"  # scripted group (container) (typed FeaturePython)
  n = 0.022
FEATURE [App::DocumentObjectGroupPython] O_element017  label="O_element : 0.712"  # scripted group (container) (typed FeaturePython)
  n = 0.712
FEATURE [App::DocumentObjectGroupPython] Na_element004  label="Na_element : 0.004"  # scripted group (container) (typed FeaturePython)
  n = 0.002
FEATURE [App::DocumentObjectGroupPython] P_element004  label="P_element : 0.004"  # scripted group (container) (typed FeaturePython)
  n = 0.004
FEATURE [App::DocumentObjectGroupPython] S_element006  label="S_element : 0.005"  # scripted group (container) (typed FeaturePython)
  n = 0.002
FEATURE [App::DocumentObjectGroupPython] Cl_element003  label="Cl_element : 0.004"  # scripted group (container) (typed FeaturePython)
  n = 0.003
FEATURE [App::DocumentObjectGroupPython] K_element002  label="K_element : 0.003"  # scripted group (container) (typed FeaturePython)
  n = 0.003
FEATURE [App::DocumentObjectGroupPython] G4_BRAIN_ICRP  # scripted group (container) (typed FeaturePython)
  Dunit = g/cm3
  Dvalue = 1.04
  Group = -> [H_element017,C_element018,N_element012,O_element017,Na_element004,P_element004,S_element006,Cl_element003,K_element002]
  conduct = 2
  density = 1
  expand = 3
  formula = G4_BRAIN_ICRP
  name = G4_BRAIN_ICRP
  specific = 4
FEATURE [App::DocumentObjectGroupPython] C_element019  label="C_element : 4"  # scripted group (container) (typed FeaturePython)
  n = 4
  ref = C_element
FEATURE [App::DocumentObjectGroupPython] H_element018  label="H_element : 010"  # scripted group (container) (typed FeaturePython)
  n = 10
  ref = H_element
FEATURE [App::DocumentObjectGroupPython] G4_BUTANE  # scripted group (container) (typed FeaturePython)
  Dunit = g/cm3
  Dvalue = 0.00249343
  Group = -> [C_element019,H_element018]
  conduct = 2
  density = 1
  expand = 3
  formula = G4_BUTANE
  name = G4_BUTANE
  specific = 4
FEATURE [App::DocumentObjectGroupPython] C_element020  label="C_element : 008"  # scripted group (container) (typed FeaturePython)
  n = 4
  ref = C_element
FEATURE [App::DocumentObjectGroupPython] H_element019  label="H_element : 011"  # scripted group (container) (typed FeaturePython)
  n = 10
  ref = H_element
FEATURE [App::DocumentObjectGroupPython] O_element018  label="O_element : 007"  # scripted group (container) (typed FeaturePython)
  n = 1
  ref = O_element
FEATURE [App::DocumentObjectGroupPython] G4_N_BUTYL_ALCOHOL  label="G4_N-BUTYL_ALCOHOL"  # scripted group (container) (typed FeaturePython)
  Dunit = g/cm3
  Dvalue = 0.8098
  Group = -> [C_element020,H_element019,O_element018]
  conduct = 2
  density = 1
  expand = 3
  formula = G4_N-BUTYL_ALCOHOL
  name = G4_N-BUTYL_ALCOHOL
  specific = 4
FEATURE [App::DocumentObjectGroupPython] H_element020  label="H_element : 0.025"  # scripted group (container) (typed FeaturePython)
  n = 0.02468
FEATURE [App::DocumentObjectGroupPython] C_element021  label="C_element : 0.502"  # scripted group (container) (typed FeaturePython)
  n = 0.501611
FEATURE [App::DocumentObjectGroupPython] O_element019  label="O_element : 0.005"  # scripted group (container) (typed FeaturePython)
  n = 0.004527
FEATURE [App::DocumentObjectGroupPython] F_element004  label="F_element : 0.465"  # scripted group (container) (typed FeaturePython)
  n = 0.465209
FEATURE [App::DocumentObjectGroupPython] Si_element001  label="Si_element : 0.004"  # scripted group (container) (typed FeaturePython)
  n = 0.003973
FEATURE [App::DocumentObjectGroupPython] G4_C_552  label="G4_C-552"  # scripted group (container) (typed FeaturePython)
  Dunit = g/cm3
  Dvalue = 1.76
  Group = -> [H_element020,C_element021,O_element019,F_element004,Si_element001]
  conduct = 2
  density = 1
  expand = 3
  formula = G4_C-552
  name = G4_C-552
  specific = 4
FEATURE [App::DocumentObjectGroupPython] Cd_element001  label="Cd_element : 1"  # scripted group (container) (typed FeaturePython)
  n = 1
  ref = Cd_element
FEATURE [App::DocumentObjectGroupPython] Te_element001  label="Te_element : 1"  # scripted group (container) (typed FeaturePython)
  n = 1
  ref = Te_element
FEATURE [App::DocumentObjectGroupPython] G4_CADMIUM_TELLURIDE  # scripted group (container) (typed FeaturePython)
  Dunit = g/cm3
  Dvalue = 6.2
  Group = -> [Cd_element001,Te_element001]
  conduct = 2
  density = 1
  expand = 3
  formula = G4_CADMIUM_TELLURIDE
  name = G4_CADMIUM_TELLURIDE
  specific = 4
FEATURE [App::DocumentObjectGroupPython] Cd_element002  label="Cd_element : 002"  # scripted group (container) (typed FeaturePython)
  n = 1
  ref = Cd_element
FEATURE [App::DocumentObjectGroupPython] W_element001  label="W_element : 1"  # scripted group (container) (typed FeaturePython)
  n = 1
  ref = W_element
FEATURE [App::DocumentObjectGroupPython] O_element020  label="O_element : 008"  # scripted group (container) (typed FeaturePython)
  n = 4
  ref = O_element
FEATURE [App::DocumentObjectGroupPython] G4_CADMIUM_TUNGSTATE  # scripted group (container) (typed FeaturePython)
  Dunit = g/cm3
  Dvalue = 7.9
  Group = -> [Cd_element002,W_element001,O_element020]
  conduct = 2
  density = 1
  expand = 3
  formula = G4_CADMIUM_TUNGSTATE
  name = G4_CADMIUM_TUNGSTATE
  specific = 4
FEATURE [App::DocumentObjectGroupPython] Ca_element005  label="Ca_element : 1"  # scripted group (container) (typed FeaturePython)
  n = 1
  ref = Ca_element
FEATURE [App::DocumentObjectGroupPython] C_element022  label="C_element : 009"  # scripted group (container) (typed FeaturePython)
  n = 1
  ref = C_element
FEATURE [App::DocumentObjectGroupPython] O_element021  label="O_element : 009"  # scripted group (container) (typed FeaturePython)
  n = 3
  ref = O_element
FEATURE [App::DocumentObjectGroupPython] G4_CALCIUM_CARBONATE  # scripted group (container) (typed FeaturePython)
  Dunit = g/cm3
  Dvalue = 2.8
  Group = -> [Ca_element005,C_element022,O_element021]
  conduct = 2
  density = 1
  expand = 3
  formula = G4_CALCIUM_CARBONATE
  name = G4_CALCIUM_CARBONATE
  specific = 4
FEATURE [App::DocumentObjectGroupPython] Ca_element006  label="Ca_element : 002"  # scripted group (container) (typed FeaturePython)
  n = 1
  ref = Ca_element
FEATURE [App::DocumentObjectGroupPython] F_element005  label="F_element : 003"  # scripted group (container) (typed FeaturePython)
  n = 2
  ref = F_element
FEATURE [App::DocumentObjectGroupPython] G4_CALCIUM_FLUORIDE  # scripted group (container) (typed FeaturePython)
  Dunit = g/cm3
  Dvalue = 3.18
  Group = -> [Ca_element006,F_element005]
  conduct = 2
  density = 1
  expand = 3
  formula = G4_CALCIUM_FLUORIDE
  name = G4_CALCIUM_FLUORIDE
  specific = 4
FEATURE [App::DocumentObjectGroupPython] Ca_element007  label="Ca_element : 003"  # scripted group (container) (typed FeaturePython)
  n = 1
  ref = Ca_element
FEATURE [App::DocumentObjectGroupPython] O_element022  label="O_element : 010"  # scripted group (container) (typed FeaturePython)
  n = 1
  ref = O_element
FEATURE [App::DocumentObjectGroupPython] G4_CALCIUM_OXIDE  # scripted group (container) (typed FeaturePython)
  Dunit = g/cm3
  Dvalue = 3.3
  Group = -> [Ca_element007,O_element022]
  conduct = 2
  density = 1
  expand = 3
  formula = G4_CALCIUM_OXIDE
  name = G4_CALCIUM_OXIDE
  specific = 4
FEATURE [App::DocumentObjectGroupPython] Ca_element008  label="Ca_element : 004"  # scripted group (container) (typed FeaturePython)
  n = 1
  ref = Ca_element
FEATURE [App::DocumentObjectGroupPython] S_element007  label="S_element : 002"  # scripted group (container) (typed FeaturePython)
  n = 1
  ref = S_element
FEATURE [App::DocumentObjectGroupPython] O_element023  label="O_element : 011"  # scripted group (container) (typed FeaturePython)
  n = 4
  ref = O_element
FEATURE [App::DocumentObjectGroupPython] G4_CALCIUM_SULFATE  # scripted group (container) (typed FeaturePython)
  Dunit = g/cm3
  Dvalue = 2.96
  Group = -> [Ca_element008,S_element007,O_element023]
  conduct = 2
  density = 1
  expand = 3
  formula = G4_CALCIUM_SULFATE
  name = G4_CALCIUM_SULFATE
  specific = 4
FEATURE [App::DocumentObjectGroupPython] Ca_element009  label="Ca_element : 005"  # scripted group (container) (typed FeaturePython)
  n = 1
  ref = Ca_element
FEATURE [App::DocumentObjectGroupPython] W_element002  label="W_element : 002"  # scripted group (container) (typed FeaturePython)
  n = 1
  ref = W_element
FEATURE [App::DocumentObjectGroupPython] O_element024  label="O_element : 012"  # scripted group (container) (typed FeaturePython)
  n = 4
  ref = O_element
FEATURE [App::DocumentObjectGroupPython] G4_CALCIUM_TUNGSTATE  # scripted group (container) (typed FeaturePython)
  Dunit = g/cm3
  Dvalue = 6.062
  Group = -> [Ca_element009,W_element002,O_element024]
  conduct = 2
  density = 1
  expand = 3
  formula = G4_CALCIUM_TUNGSTATE
  name = G4_CALCIUM_TUNGSTATE
  specific = 4
FEATURE [App::DocumentObjectGroupPython] C_element023  label="C_element : 010"  # scripted group (container) (typed FeaturePython)
  n = 1
  ref = C_element
FEATURE [App::DocumentObjectGroupPython] O_element025  label="O_element : 013"  # scripted group (container) (typed FeaturePython)
  n = 2
  ref = O_element
FEATURE [App::DocumentObjectGroupPython] G4_CARBON_DIOXIDE  # scripted group (container) (typed FeaturePython)
  Dunit = g/cm3
  Dvalue = 0.00184212
  Group = -> [C_element023,O_element025]
  conduct = 2
  density = 1
  expand = 3
  formula = G4_CARBON_DIOXIDE
  name = G4_CARBON_DIOXIDE
  specific = 4
FEATURE [App::DocumentObjectGroupPython] C_element024  label="C_element : 011"  # scripted group (container) (typed FeaturePython)
  n = 1
  ref = C_element
FEATURE [App::DocumentObjectGroupPython] Cl_element004  label="Cl_element : 4"  # scripted group (container) (typed FeaturePython)
  n = 4
  ref = Cl_element
FEATURE [App::DocumentObjectGroupPython] G4_CARBON_TETRACHLORIDE  # scripted group (container) (typed FeaturePython)
  Dunit = g/cm3
  Dvalue = 1.594
  Group = -> [C_element024,Cl_element004]
  conduct = 2
  density = 1
  expand = 3
  formula = G4_CARBON_TETRACHLORIDE
  name = G4_CARBON_TETRACHLORIDE
  specific = 4
FEATURE [App::DocumentObjectGroupPython] C_element025  label="C_element : 012"  # scripted group (container) (typed FeaturePython)
  n = 6
  ref = C_element
FEATURE [App::DocumentObjectGroupPython] H_element021  label="H_element : 012"  # scripted group (container) (typed FeaturePython)
  n = 10
  ref = H_element
FEATURE [App::DocumentObjectGroupPython] O_element026  label="O_element : 5"  # scripted group (container) (typed FeaturePython)
  n = 5
  ref = O_element
FEATURE [App::DocumentObjectGroupPython] G4_CELLULOSE_CELLOPHANE  # scripted group (container) (typed FeaturePython)
  Dunit = g/cm3
  Dvalue = 1.42
  Group = -> [C_element025,H_element021,O_element026]
  conduct = 2
  density = 1
  expand = 3
  formula = G4_CELLULOSE_CELLOPHANE
  name = G4_CELLULOSE_CELLOPHANE
  specific = 4
FEATURE [App::DocumentObjectGroupPython] H_element022  label="H_element : 0.067"  # scripted group (container) (typed FeaturePython)
  n = 0.067125
FEATURE [App::DocumentObjectGroupPython] C_element026  label="C_element : 0.545"  # scripted group (container) (typed FeaturePython)
  n = 0.545403
FEATURE [App::DocumentObjectGroupPython] O_element027  label="O_element : 0.387"  # scripted group (container) (typed FeaturePython)
  n = 0.387472
FEATURE [App::DocumentObjectGroupPython] G4_CELLULOSE_BUTYRATE  # scripted group (container) (typed FeaturePython)
  Dunit = g/cm3
  Dvalue = 1.2
  Group = -> [H_element022,C_element026,O_element027]
  conduct = 2
  density = 1
  expand = 3
  formula = G4_CELLULOSE_BUTYRATE
  name = G4_CELLULOSE_BUTYRATE
  specific = 4
FEATURE [App::DocumentObjectGroupPython] H_element023  label="H_element : 0.029"  # scripted group (container) (typed FeaturePython)
  n = 0.029216
FEATURE [App::DocumentObjectGroupPython] C_element027  label="C_element : 0.271"  # scripted group (container) (typed FeaturePython)
  n = 0.271296
FEATURE [App::DocumentObjectGroupPython] N_element013  label="N_element : 0.121"  # scripted group (container) (typed FeaturePython)
  n = 0.121276
FEATURE [App::DocumentObjectGroupPython] O_element028  label="O_element : 0.578"  # scripted group (container) (typed FeaturePython)
  n = 0.578212
FEATURE [App::DocumentObjectGroupPython] G4_CELLULOSE_NITRATE  # scripted group (container) (typed FeaturePython)
  Dunit = g/cm3
  Dvalue = 1.49
  Group = -> [H_element023,C_element027,N_element013,O_element028]
  conduct = 2
  density = 1
  expand = 3
  formula = G4_CELLULOSE_NITRATE
  name = G4_CELLULOSE_NITRATE
  specific = 4
FEATURE [App::DocumentObjectGroupPython] H_element024  label="H_element : 0.108"  # scripted group (container) (typed FeaturePython)
  n = 0.107596
FEATURE [App::DocumentObjectGroupPython] N_element014  label="N_element : 0.001"  # scripted group (container) (typed FeaturePython)
  n = 0.0008
FEATURE [App::DocumentObjectGroupPython] O_element029  label="O_element : 0.875"  # scripted group (container) (typed FeaturePython)
  n = 0.874976
FEATURE [App::DocumentObjectGroupPython] S_element008  label="S_element : 0.015"  # scripted group (container) (typed FeaturePython)
  n = 0.014627
FEATURE [App::DocumentObjectGroupPython] Ce_element001  label="Ce_element : 0.002"  # scripted group (container) (typed FeaturePython)
  n = 0.002001
FEATURE [App::DocumentObjectGroupPython] G4_CERIC_SULFATE  # scripted group (container) (typed FeaturePython)
  Dunit = g/cm3
  Dvalue = 1.03
  Group = -> [H_element024,N_element014,O_element029,S_element008,Ce_element001]
  conduct = 2
  density = 1
  expand = 3
  formula = G4_CERIC_SULFATE
  name = G4_CERIC_SULFATE
  specific = 4
FEATURE [App::DocumentObjectGroupPython] Cs_element001  label="Cs_element : 1"  # scripted group (container) (typed FeaturePython)
  n = 1
  ref = Cs_element
FEATURE [App::DocumentObjectGroupPython] F_element006  label="F_element : 1"  # scripted group (container) (typed FeaturePython)
  n = 1
  ref = F_element
FEATURE [App::DocumentObjectGroupPython] G4_CESIUM_FLUORIDE  # scripted group (container) (typed FeaturePython)
  Dunit = g/cm3
  Dvalue = 4.115
  Group = -> [Cs_element001,F_element006]
  conduct = 2
  density = 1
  expand = 3
  formula = G4_CESIUM_FLUORIDE
  name = G4_CESIUM_FLUORIDE
  specific = 4
FEATURE [App::DocumentObjectGroupPython] Cs_element002  label="Cs_element : 002"  # scripted group (container) (typed FeaturePython)
  n = 1
  ref = Cs_element
FEATURE [App::DocumentObjectGroupPython] I_element001  label="I_element : 1"  # scripted group (container) (typed FeaturePython)
  n = 1
  ref = I_element
FEATURE [App::DocumentObjectGroupPython] G4_CESIUM_IODIDE  # scripted group (container) (typed FeaturePython)
  Dunit = g/cm3
  Dvalue = 4.51
  Group = -> [Cs_element002,I_element001]
  conduct = 2
  density = 1
  expand = 3
  formula = G4_CESIUM_IODIDE
  name = G4_CESIUM_IODIDE
  specific = 4
FEATURE [App::DocumentObjectGroupPython] C_element028  label="C_element : 013"  # scripted group (container) (typed FeaturePython)
  n = 6
  ref = C_element
FEATURE [App::DocumentObjectGroupPython] H_element025  label="H_element : 013"  # scripted group (container) (typed FeaturePython)
  n = 5
  ref = H_element
FEATURE [App::DocumentObjectGroupPython] Cl_element005  label="Cl_element : 1"  # scripted group (container) (typed FeaturePython)
  n = 1
  ref = Cl_element
FEATURE [App::DocumentObjectGroupPython] G4_CHLOROBENZENE  # scripted group (container) (typed FeaturePython)
  Dunit = g/cm3
  Dvalue = 1.1058
  Group = -> [C_element028,H_element025,Cl_element005]
  conduct = 2
  density = 1
  expand = 3
  formula = G4_CHLOROBENZENE
  name = G4_CHLOROBENZENE
  specific = 4
FEATURE [App::DocumentObjectGroupPython] C_element029  label="C_element : 014"  # scripted group (container) (typed FeaturePython)
  n = 1
  ref = C_element
FEATURE [App::DocumentObjectGroupPython] H_element026  label="H_element : 1"  # scripted group (container) (typed FeaturePython)
  n = 1
  ref = H_element
FEATURE [App::DocumentObjectGroupPython] Cl_element006  label="Cl_element : 3"  # scripted group (container) (typed FeaturePython)
  n = 3
  ref = Cl_element
FEATURE [App::DocumentObjectGroupPython] G4_CHLOROFORM  # scripted group (container) (typed FeaturePython)
  Dunit = g/cm3
  Dvalue = 1.4832
  Group = -> [C_element029,H_element026,Cl_element006]
  conduct = 2
  density = 1
  expand = 3
  formula = G4_CHLOROFORM
  name = G4_CHLOROFORM
  specific = 4
FEATURE [App::DocumentObjectGroupPython] H_element027  label="H_element : 0.010"  # scripted group (container) (typed FeaturePython)
  n = 0.01
FEATURE [App::DocumentObjectGroupPython] C_element030  label="C_element : 0.001"  # scripted group (container) (typed FeaturePython)
  n = 0.001
FEATURE [App::DocumentObjectGroupPython] O_element030  label="O_element : 0.529"  # scripted group (container) (typed FeaturePython)
  n = 0.529107
FEATURE [App::DocumentObjectGroupPython] Na_element005  label="Na_element : 0.016"  # scripted group (container) (typed FeaturePython)
  n = 0.016
FEATURE [App::DocumentObjectGroupPython] Mg_element003  label="Mg_element : 0.004"  # scripted group (container) (typed FeaturePython)
  n = 0.002
FEATURE [App::DocumentObjectGroupPython] Al_element002  label="Al_element : 0.034"  # scripted group (container) (typed FeaturePython)
  n = 0.033872
FEATURE [App::DocumentObjectGroupPython] Si_element002  label="Si_element : 0.337"  # scripted group (container) (typed FeaturePython)
  n = 0.337021
FEATURE [App::DocumentObjectGroupPython] K_element003  label="K_element : 0.013"  # scripted group (container) (typed FeaturePython)
  n = 0.013
FEATURE [App::DocumentObjectGroupPython] Ca_element010  label="Ca_element : 0.044"  # scripted group (container) (typed FeaturePython)
  n = 0.044
FEATURE [App::DocumentObjectGroupPython] Fe_element002  label="Fe_element : 0.014"  # scripted group (container) (typed FeaturePython)
  n = 0.014
FEATURE [App::DocumentObjectGroupPython] G4_CONCRETE  # scripted group (container) (typed FeaturePython)
  Dunit = g/cm3
  Dvalue = 2.3
  Group = -> [H_element027,C_element030,O_element030,Na_element005,Mg_element003,Al_element002,Si_element002,K_element003,Ca_element010,Fe_element002]
  conduct = 2
  density = 1
  expand = 3
  formula = G4_CONCRETE
  name = G4_CONCRETE
  specific = 4
FEATURE [App::DocumentObjectGroupPython] C_element031  label="C_element : 015"  # scripted group (container) (typed FeaturePython)
  n = 6
  ref = C_element
FEATURE [App::DocumentObjectGroupPython] H_element028  label="H_element : 12"  # scripted group (container) (typed FeaturePython)
  n = 12
  ref = H_element
FEATURE [App::DocumentObjectGroupPython] G4_CYCLOHEXANE  # scripted group (container) (typed FeaturePython)
  Dunit = g/cm3
  Dvalue = 0.779
  Group = -> [C_element031,H_element028]
  conduct = 2
  density = 1
  expand = 3
  formula = G4_CYCLOHEXANE
  name = G4_CYCLOHEXANE
  specific = 4
FEATURE [App::DocumentObjectGroupPython] C_element032  label="C_element : 016"  # scripted group (container) (typed FeaturePython)
  n = 6
  ref = C_element
FEATURE [App::DocumentObjectGroupPython] H_element029  label="H_element : 4"  # scripted group (container) (typed FeaturePython)
  n = 4
  ref = H_element
FEATURE [App::DocumentObjectGroupPython] Cl_element007  label="Cl_element : 2"  # scripted group (container) (typed FeaturePython)
  n = 2
  ref = Cl_element
FEATURE [App::DocumentObjectGroupPython] G4_1_2_DICHLOROBENZENE  label="G4_1.2-DICHLOROBENZENE"  # scripted group (container) (typed FeaturePython)
  Dunit = g/cm3
  Dvalue = 1.3048
  Group = -> [C_element032,H_element029,Cl_element007]
  conduct = 2
  density = 1
  expand = 3
  formula = G4_1.2-DICHLOROBENZENE
  name = G4_1.2-DICHLOROBENZENE
  specific = 4
FEATURE [App::DocumentObjectGroupPython] C_element033  label="C_element : 017"  # scripted group (container) (typed FeaturePython)
  n = 4
  ref = C_element
FEATURE [App::DocumentObjectGroupPython] H_element030  label="H_element : 8"  # scripted group (container) (typed FeaturePython)
  n = 8
  ref = H_element
FEATURE [App::DocumentObjectGroupPython] O_element031  label="O_element : 014"  # scripted group (container) (typed FeaturePython)
  n = 1
  ref = O_element
FEATURE [App::DocumentObjectGroupPython] Cl_element008  label="Cl_element : 005"  # scripted group (container) (typed FeaturePython)
  n = 2
  ref = Cl_element
FEATURE [App::DocumentObjectGroupPython] G4_DICHLORODIETHYL_ETHER  # scripted group (container) (typed FeaturePython)
  Dunit = g/cm3
  Dvalue = 1.2199
  Group = -> [C_element033,H_element030,O_element031,Cl_element008]
  conduct = 2
  density = 1
  expand = 3
  formula = G4_DICHLORODIETHYL_ETHER
  name = G4_DICHLORODIETHYL_ETHER
  specific = 4
FEATURE [App::DocumentObjectGroupPython] C_element034  label="C_element : 018"  # scripted group (container) (typed FeaturePython)
  n = 2
  ref = C_element
FEATURE [App::DocumentObjectGroupPython] H_element031  label="H_element : 014"  # scripted group (container) (typed FeaturePython)
  n = 4
  ref = H_element
FEATURE [App::DocumentObjectGroupPython] Cl_element009  label="Cl_element : 006"  # scripted group (container) (typed FeaturePython)
  n = 2
  ref = Cl_element
FEATURE [App::DocumentObjectGroupPython] G4_1_2_DICHLOROETHANE  label="G4_1.2-DICHLOROETHANE"  # scripted group (container) (typed FeaturePython)
  Dunit = g/cm3
  Dvalue = 1.2351
  Group = -> [C_element034,H_element031,Cl_element009]
  conduct = 2
  density = 1
  expand = 3
  formula = G4_1.2-DICHLOROETHANE
  name = G4_1.2-DICHLOROETHANE
  specific = 4
FEATURE [App::DocumentObjectGroupPython] C_element035  label="C_element : 019"  # scripted group (container) (typed FeaturePython)
  n = 4
  ref = C_element
FEATURE [App::DocumentObjectGroupPython] H_element032  label="H_element : 015"  # scripted group (container) (typed FeaturePython)
  n = 10
  ref = H_element
FEATURE [App::DocumentObjectGroupPython] O_element032  label="O_element : 015"  # scripted group (container) (typed FeaturePython)
  n = 1
  ref = O_element
FEATURE [App::DocumentObjectGroupPython] G4_DIETHYL_ETHER  # scripted group (container) (typed FeaturePython)
  Dunit = g/cm3
  Dvalue = 0.71378
  Group = -> [C_element035,H_element032,O_element032]
  conduct = 2
  density = 1
  expand = 3
  formula = G4_DIETHYL_ETHER
  name = G4_DIETHYL_ETHER
  specific = 4
FEATURE [App::DocumentObjectGroupPython] C_element036  label="C_element : 020"  # scripted group (container) (typed FeaturePython)
  n = 3
  ref = C_element
FEATURE [App::DocumentObjectGroupPython] H_element033  label="H_element : 016"  # scripted group (container) (typed FeaturePython)
  n = 7
  ref = H_element
FEATURE [App::DocumentObjectGroupPython] N_element015  label="N_element : 008"  # scripted group (container) (typed FeaturePython)
  n = 1
  ref = N_element
FEATURE [App::DocumentObjectGroupPython] O_element033  label="O_element : 016"  # scripted group (container) (typed FeaturePython)
  n = 1
  ref = O_element
FEATURE [App::DocumentObjectGroupPython] G4_N_N_DIMETHYL_FORMAMIDE  label="G4_N.N-DIMETHYL_FORMAMIDE"  # scripted group (container) (typed FeaturePython)
  Dunit = g/cm3
  Dvalue = 0.9487
  Group = -> [C_element036,H_element033,N_element015,O_element033]
  conduct = 2
  density = 1
  expand = 3
  formula = G4_N.N-DIMETHYL_FORMAMIDE
  name = G4_N.N-DIMETHYL_FORMAMIDE
  specific = 4
FEATURE [App::DocumentObjectGroupPython] C_element037  label="C_element : 021"  # scripted group (container) (typed FeaturePython)
  n = 2
  ref = C_element
FEATURE [App::DocumentObjectGroupPython] H_element034  label="H_element : 017"  # scripted group (container) (typed FeaturePython)
  n = 6
  ref = H_element
FEATURE [App::DocumentObjectGroupPython] O_element034  label="O_element : 017"  # scripted group (container) (typed FeaturePython)
  n = 1
  ref = O_element
FEATURE [App::DocumentObjectGroupPython] S_element009  label="S_element : 003"  # scripted group (container) (typed FeaturePython)
  n = 1
  ref = S_element
FEATURE [App::DocumentObjectGroupPython] G4_DIMETHYL_SULFOXIDE  # scripted group (container) (typed FeaturePython)
  Dunit = g/cm3
  Dvalue = 1.1014
  Group = -> [C_element037,H_element034,O_element034,S_element009]
  conduct = 2
  density = 1
  expand = 3
  formula = G4_DIMETHYL_SULFOXIDE
  name = G4_DIMETHYL_SULFOXIDE
  specific = 4
FEATURE [App::DocumentObjectGroupPython] C_element038  label="C_element : 022"  # scripted group (container) (typed FeaturePython)
  n = 2
  ref = C_element
FEATURE [App::DocumentObjectGroupPython] H_element035  label="H_element : 018"  # scripted group (container) (typed FeaturePython)
  n = 6
  ref = H_element
FEATURE [App::DocumentObjectGroupPython] G4_ETHANE  # scripted group (container) (typed FeaturePython)
  Dunit = g/cm3
  Dvalue = 0.00125324
  Group = -> [C_element038,H_element035]
  conduct = 2
  density = 1
  expand = 3
  formula = G4_ETHANE
  name = G4_ETHANE
  specific = 4
FEATURE [App::DocumentObjectGroupPython] C_element039  label="C_element : 023"  # scripted group (container) (typed FeaturePython)
  n = 2
  ref = C_element
FEATURE [App::DocumentObjectGroupPython] H_element036  label="H_element : 019"  # scripted group (container) (typed FeaturePython)
  n = 6
  ref = H_element
FEATURE [App::DocumentObjectGroupPython] O_element035  label="O_element : 018"  # scripted group (container) (typed FeaturePython)
  n = 1
  ref = O_element
FEATURE [App::DocumentObjectGroupPython] G4_ETHYL_ALCOHOL  # scripted group (container) (typed FeaturePython)
  Dunit = g/cm3
  Dvalue = 0.7893
  Group = -> [C_element039,H_element036,O_element035]
  conduct = 2
  density = 1
  expand = 3
  formula = G4_ETHYL_ALCOHOL
  name = G4_ETHYL_ALCOHOL
  specific = 4
FEATURE [App::DocumentObjectGroupPython] H_element037  label="H_element : 0.090"  # scripted group (container) (typed FeaturePython)
  n = 0.090027
FEATURE [App::DocumentObjectGroupPython] C_element040  label="C_element : 0.585"  # scripted group (container) (typed FeaturePython)
  n = 0.585182
FEATURE [App::DocumentObjectGroupPython] O_element036  label="O_element : 0.325"  # scripted group (container) (typed FeaturePython)
  n = 0.324791
FEATURE [App::DocumentObjectGroupPython] G4_ETHYL_CELLULOSE  # scripted group (container) (typed FeaturePython)
  Dunit = g/cm3
  Dvalue = 1.13
  Group = -> [H_element037,C_element040,O_element036]
  conduct = 2
  density = 1
  expand = 3
  formula = G4_ETHYL_CELLULOSE
  name = G4_ETHYL_CELLULOSE
  specific = 4
FEATURE [App::DocumentObjectGroupPython] C_element041  label="C_element : 024"  # scripted group (container) (typed FeaturePython)
  n = 2
  ref = C_element
FEATURE [App::DocumentObjectGroupPython] H_element038  label="H_element : 020"  # scripted group (container) (typed FeaturePython)
  n = 4
  ref = H_element
FEATURE [App::DocumentObjectGroupPython] G4_ETHYLENE  # scripted group (container) (typed FeaturePython)
  Dunit = g/cm3
  Dvalue = 0.00117497
  Group = -> [C_element041,H_element038]
  conduct = 2
  density = 1
  expand = 3
  formula = G4_ETHYLENE
  name = G4_ETHYLENE
  specific = 4
FEATURE [App::DocumentObjectGroupPython] H_element039  label="H_element : 0.096"  # scripted group (container) (typed FeaturePython)
  n = 0.096
FEATURE [App::DocumentObjectGroupPython] C_element042  label="C_element : 0.195"  # scripted group (container) (typed FeaturePython)
  n = 0.195
FEATURE [App::DocumentObjectGroupPython] N_element016  label="N_element : 0.057"  # scripted group (container) (typed FeaturePython)
  n = 0.057
FEATURE [App::DocumentObjectGroupPython] O_element037  label="O_element : 0.646"  # scripted group (container) (typed FeaturePython)
  n = 0.646
FEATURE [App::DocumentObjectGroupPython] Na_element006  label="Na_element : 0.017"  # scripted group (container) (typed FeaturePython)
  n = 0.001
FEATURE [App::DocumentObjectGroupPython] P_element005  label="P_element : 0.104"  # scripted group (container) (typed FeaturePython)
  n = 0.001
FEATURE [App::DocumentObjectGroupPython] S_element010  label="S_element : 0.016"  # scripted group (container) (typed FeaturePython)
  n = 0.003
FEATURE [App::DocumentObjectGroupPython] Cl_element010  label="Cl_element : 0.005"  # scripted group (container) (typed FeaturePython)
  n = 0.001
FEATURE [App::DocumentObjectGroupPython] G4_EYE_LENS_ICRP  # scripted group (container) (typed FeaturePython)
  Dunit = g/cm3
  Dvalue = 1.07
  Group = -> [H_element039,C_element042,N_element016,O_element037,Na_element006,P_element005,S_element010,Cl_element010]
  conduct = 2
  density = 1
  expand = 3
  formula = G4_EYE_LENS_ICRP
  name = G4_EYE_LENS_ICRP
  specific = 4
FEATURE [App::DocumentObjectGroupPython] Fe_element003  label="Fe_element : 2"  # scripted group (container) (typed FeaturePython)
  n = 2
  ref = Fe_element
FEATURE [App::DocumentObjectGroupPython] O_element038  label="O_element : 019"  # scripted group (container) (typed FeaturePython)
  n = 3
  ref = O_element
FEATURE [App::DocumentObjectGroupPython] G4_FERRIC_OXIDE  # scripted group (container) (typed FeaturePython)
  Dunit = g/cm3
  Dvalue = 5.2
  Group = -> [Fe_element003,O_element038]
  conduct = 2
  density = 1
  expand = 3
  formula = G4_FERRIC_OXIDE
  name = G4_FERRIC_OXIDE
  specific = 4
FEATURE [App::DocumentObjectGroupPython] Fe_element004  label="Fe_element : 1"  # scripted group (container) (typed FeaturePython)
  n = 1
  ref = Fe_element
FEATURE [App::DocumentObjectGroupPython] B_element003  label="B_element : 1"  # scripted group (container) (typed FeaturePython)
  n = 1
  ref = B_element
FEATURE [App::DocumentObjectGroupPython] G4_FERROBORIDE  # scripted group (container) (typed FeaturePython)
  Dunit = g/cm3
  Dvalue = 7.15
  Group = -> [Fe_element004,B_element003]
  conduct = 2
  density = 1
  expand = 3
  formula = G4_FERROBORIDE
  name = G4_FERROBORIDE
  specific = 4
FEATURE [App::DocumentObjectGroupPython] Fe_element005  label="Fe_element : 003"  # scripted group (container) (typed FeaturePython)
  n = 1
  ref = Fe_element
FEATURE [App::DocumentObjectGroupPython] O_element039  label="O_element : 020"  # scripted group (container) (typed FeaturePython)
  n = 1
  ref = O_element
FEATURE [App::DocumentObjectGroupPython] G4_FERROUS_OXIDE  # scripted group (container) (typed FeaturePython)
  Dunit = g/cm3
  Dvalue = 5.7
  Group = -> [Fe_element005,O_element039]
  conduct = 2
  density = 1
  expand = 3
  formula = G4_FERROUS_OXIDE
  name = G4_FERROUS_OXIDE
  specific = 4
FEATURE [App::DocumentObjectGroupPython] H_element040  label="H_element : 0.115"  # scripted group (container) (typed FeaturePython)
  n = 0.108259
FEATURE [App::DocumentObjectGroupPython] N_element017  label="N_element : 0.000"  # scripted group (container) (typed FeaturePython)
  n = 2.7e-05
FEATURE [App::DocumentObjectGroupPython] O_element040  label="O_element : 0.879"  # scripted group (container) (typed FeaturePython)
  n = 0.878636
FEATURE [App::DocumentObjectGroupPython] Na_element007  label="Na_element : 0.000"  # scripted group (container) (typed FeaturePython)
  n = 2.2e-05
FEATURE [App::DocumentObjectGroupPython] S_element011  label="S_element : 0.013"  # scripted group (container) (typed FeaturePython)
  n = 0.012968
FEATURE [App::DocumentObjectGroupPython] Cl_element011  label="Cl_element : 0.000"  # scripted group (container) (typed FeaturePython)
  n = 3.4e-05
FEATURE [App::DocumentObjectGroupPython] Fe_element006  label="Fe_element : 0.000"  # scripted group (container) (typed FeaturePython)
  n = 5.4e-05
FEATURE [App::DocumentObjectGroupPython] G4_FERROUS_SULFATE  # scripted group (container) (typed FeaturePython)
  Dunit = g/cm3
  Dvalue = 1.024
  Group = -> [H_element040,N_element017,O_element040,Na_element007,S_element011,Cl_element011,Fe_element006]
  conduct = 2
  density = 1
  expand = 3
  formula = G4_FERROUS_SULFATE
  name = G4_FERROUS_SULFATE
  specific = 4
FEATURE [App::DocumentObjectGroupPython] C_element043  label="C_element : 0.099"  # scripted group (container) (typed FeaturePython)
  n = 0.099335
FEATURE [App::DocumentObjectGroupPython] F_element007  label="F_element : 0.314"  # scripted group (container) (typed FeaturePython)
  n = 0.314247
FEATURE [App::DocumentObjectGroupPython] Cl_element012  label="Cl_element : 0.586"  # scripted group (container) (typed FeaturePython)
  n = 0.586418
FEATURE [App::DocumentObjectGroupPython] G4_FREON_12  label="G4_FREON-12"  # scripted group (container) (typed FeaturePython)
  Dunit = g/cm3
  Dvalue = 1.12
  Group = -> [C_element043,F_element007,Cl_element012]
  conduct = 2
  density = 1
  expand = 3
  formula = G4_FREON-12
  name = G4_FREON-12
  specific = 4
FEATURE [App::DocumentObjectGroupPython] C_element044  label="C_element : 0.057"  # scripted group (container) (typed FeaturePython)
  n = 0.057245
FEATURE [App::DocumentObjectGroupPython] F_element008  label="F_element : 0.181"  # scripted group (container) (typed FeaturePython)
  n = 0.181096
FEATURE [App::DocumentObjectGroupPython] Br_element001  label="Br_element : 0.762"  # scripted group (container) (typed FeaturePython)
  n = 0.761659
FEATURE [App::DocumentObjectGroupPython] G4_FREON_12B2  label="G4_FREON-12B2"  # scripted group (container) (typed FeaturePython)
  Dunit = g/cm3
  Dvalue = 1.8
  Group = -> [C_element044,F_element008,Br_element001]
  conduct = 2
  density = 1
  expand = 3
  formula = G4_FREON-12B2
  name = G4_FREON-12B2
  specific = 4
FEATURE [App::DocumentObjectGroupPython] C_element045  label="C_element : 0.115"  # scripted group (container) (typed FeaturePython)
  n = 0.114983
FEATURE [App::DocumentObjectGroupPython] F_element009  label="F_element : 0.546"  # scripted group (container) (typed FeaturePython)
  n = 0.545621
FEATURE [App::DocumentObjectGroupPython] Cl_element013  label="Cl_element : 0.339"  # scripted group (container) (typed FeaturePython)
  n = 0.339396
FEATURE [App::DocumentObjectGroupPython] G4_FREON_13  label="G4_FREON-13"  # scripted group (container) (typed FeaturePython)
  Dunit = g/cm3
  Dvalue = 0.95
  Group = -> [C_element045,F_element009,Cl_element013]
  conduct = 2
  density = 1
  expand = 3
  formula = G4_FREON-13
  name = G4_FREON-13
  specific = 4
FEATURE [App::DocumentObjectGroupPython] C_element046  label="C_element : 025"  # scripted group (container) (typed FeaturePython)
  n = 1
  ref = C_element
FEATURE [App::DocumentObjectGroupPython] F_element010  label="F_element : 3"  # scripted group (container) (typed FeaturePython)
  n = 3
  ref = F_element
FEATURE [App::DocumentObjectGroupPython] Br_element002  label="Br_element : 1"  # scripted group (container) (typed FeaturePython)
  n = 1
  ref = Br_element
FEATURE [App::DocumentObjectGroupPython] G4_FREON_13B1  label="G4_FREON-13B1"  # scripted group (container) (typed FeaturePython)
  Dunit = g/cm3
  Dvalue = 1.5
  Group = -> [C_element046,F_element010,Br_element002]
  conduct = 2
  density = 1
  expand = 3
  formula = G4_FREON-13B1
  name = G4_FREON-13B1
  specific = 4
FEATURE [App::DocumentObjectGroupPython] C_element047  label="C_element : 0.061"  # scripted group (container) (typed FeaturePython)
  n = 0.061309
FEATURE [App::DocumentObjectGroupPython] F_element011  label="F_element : 0.291"  # scripted group (container) (typed FeaturePython)
  n = 0.290924
FEATURE [App::DocumentObjectGroupPython] I_element002  label="I_element : 0.648"  # scripted group (container) (typed FeaturePython)
  n = 0.647767
FEATURE [App::DocumentObjectGroupPython] G4_FREON_13I1  label="G4_FREON-13I1"  # scripted group (container) (typed FeaturePython)
  Dunit = g/cm3
  Dvalue = 1.8
  Group = -> [C_element047,F_element011,I_element002]
  conduct = 2
  density = 1
  expand = 3
  formula = G4_FREON-13I1
  name = G4_FREON-13I1
  specific = 4
FEATURE [App::DocumentObjectGroupPython] Gd_element001  label="Gd_element : 2"  # scripted group (container) (typed FeaturePython)
  n = 2
  ref = Gd_element
FEATURE [App::DocumentObjectGroupPython] O_element041  label="O_element : 021"  # scripted group (container) (typed FeaturePython)
  n = 2
  ref = O_element
FEATURE [App::DocumentObjectGroupPython] S_element012  label="S_element : 004"  # scripted group (container) (typed FeaturePython)
  n = 1
  ref = S_element
FEATURE [App::DocumentObjectGroupPython] G4_GADOLINIUM_OXYSULFIDE  # scripted group (container) (typed FeaturePython)
  Dunit = g/cm3
  Dvalue = 7.44
  Group = -> [Gd_element001,O_element041,S_element012]
  conduct = 2
  density = 1
  expand = 3
  formula = G4_GADOLINIUM_OXYSULFIDE
  name = G4_GADOLINIUM_OXYSULFIDE
  specific = 4
FEATURE [App::DocumentObjectGroupPython] Ga_element001  label="Ga_element : 1"  # scripted group (container) (typed FeaturePython)
  n = 1
  ref = Ga_element
FEATURE [App::DocumentObjectGroupPython] As_element001  label="As_element : 1"  # scripted group (container) (typed FeaturePython)
  n = 1
  ref = As_element
FEATURE [App::DocumentObjectGroupPython] G4_GALLIUM_ARSENIDE  # scripted group (container) (typed FeaturePython)
  Dunit = g/cm3
  Dvalue = 5.31
  Group = -> [Ga_element001,As_element001]
  conduct = 2
  density = 1
  expand = 3
  formula = G4_GALLIUM_ARSENIDE
  name = G4_GALLIUM_ARSENIDE
  specific = 4
FEATURE [App::DocumentObjectGroupPython] H_element041  label="H_element : 0.081"  # scripted group (container) (typed FeaturePython)
  n = 0.08118
FEATURE [App::DocumentObjectGroupPython] C_element048  label="C_element : 0.416"  # scripted group (container) (typed FeaturePython)
  n = 0.41606
FEATURE [App::DocumentObjectGroupPython] N_element018  label="N_element : 0.111"  # scripted group (container) (typed FeaturePython)
  n = 0.11124
FEATURE [App::DocumentObjectGroupPython] O_element042  label="O_element : 0.381"  # scripted group (container) (typed FeaturePython)
  n = 0.38064
FEATURE [App::DocumentObjectGroupPython] S_element013  label="S_element : 0.011"  # scripted group (container) (typed FeaturePython)
  n = 0.01088
FEATURE [App::DocumentObjectGroupPython] G4_GEL_PHOTO_EMULSION  # scripted group (container) (typed FeaturePython)
  Dunit = g/cm3
  Dvalue = 1.2914
  Group = -> [H_element041,C_element048,N_element018,O_element042,S_element013]
  conduct = 2
  density = 1
  expand = 3
  formula = G4_GEL_PHOTO_EMULSION
  name = G4_GEL_PHOTO_EMULSION
  specific = 4
FEATURE [App::DocumentObjectGroupPython] B_element004  label="B_element : 0.040"  # scripted group (container) (typed FeaturePython)
  n = 0.0400639
FEATURE [App::DocumentObjectGroupPython] O_element043  label="O_element : 0.540"  # scripted group (container) (typed FeaturePython)
  n = 0.539561
FEATURE [App::DocumentObjectGroupPython] Na_element008  label="Na_element : 0.028"  # scripted group (container) (typed FeaturePython)
  n = 0.0281909
FEATURE [App::DocumentObjectGroupPython] Al_element003  label="Al_element : 0.012"  # scripted group (container) (typed FeaturePython)
  n = 0.011644
FEATURE [App::DocumentObjectGroupPython] Si_element003  label="Si_element : 0.377"  # scripted group (container) (typed FeaturePython)
  n = 0.377219
FEATURE [App::DocumentObjectGroupPython] K_element004  label="K_element : 0.014"  # scripted group (container) (typed FeaturePython)
  n = 0.00332099
FEATURE [App::DocumentObjectGroupPython] G4_Pyrex_Glass  # scripted group (container) (typed FeaturePython)
  Dunit = g/cm3
  Dvalue = 2.23
  Group = -> [B_element004,O_element043,Na_element008,Al_element003,Si_element003,K_element004]
  conduct = 2
  density = 1
  expand = 3
  formula = G4_Pyrex_Glass
  name = G4_Pyrex_Glass
  specific = 4
FEATURE [App::DocumentObjectGroupPython] O_element044  label="O_element : 0.156"  # scripted group (container) (typed FeaturePython)
  n = 0.156453
FEATURE [App::DocumentObjectGroupPython] Si_element004  label="Si_element : 0.081"  # scripted group (container) (typed FeaturePython)
  n = 0.080866
FEATURE [App::DocumentObjectGroupPython] Ti_element001  label="Ti_element : 0.008"  # scripted group (container) (typed FeaturePython)
  n = 0.008092
FEATURE [App::DocumentObjectGroupPython] As_element002  label="As_element : 0.003"  # scripted group (container) (typed FeaturePython)
  n = 0.002651
FEATURE [App::DocumentObjectGroupPython] Pb_element001  label="Pb_element : 0.752"  # scripted group (container) (typed FeaturePython)
  n = 0.751938
FEATURE [App::DocumentObjectGroupPython] G4_GLASS_LEAD  # scripted group (container) (typed FeaturePython)
  Dunit = g/cm3
  Dvalue = 6.22
  Group = -> [O_element044,Si_element004,Ti_element001,As_element002,Pb_element001]
  conduct = 2
  density = 1
  expand = 3
  formula = G4_GLASS_LEAD
  name = G4_GLASS_LEAD
  specific = 4
FEATURE [App::DocumentObjectGroupPython] O_element045  label="O_element : 0.460"  # scripted group (container) (typed FeaturePython)
  n = 0.4598
FEATURE [App::DocumentObjectGroupPython] Na_element009  label="Na_element : 0.096"  # scripted group (container) (typed FeaturePython)
  n = 0.0964411
FEATURE [App::DocumentObjectGroupPython] Si_element005  label="Si_element : 0.378"  # scripted group (container) (typed FeaturePython)
  n = 0.336553
FEATURE [App::DocumentObjectGroupPython] Ca_element011  label="Ca_element : 0.107"  # scripted group (container) (typed FeaturePython)
  n = 0.107205
FEATURE [App::DocumentObjectGroupPython] G4_GLASS_PLATE  # scripted group (container) (typed FeaturePython)
  Dunit = g/cm3
  Dvalue = 2.4
  Group = -> [O_element045,Na_element009,Si_element005,Ca_element011]
  conduct = 2
  density = 1
  expand = 3
  formula = G4_GLASS_PLATE
  name = G4_GLASS_PLATE
  specific = 4
FEATURE [App::DocumentObjectGroupPython] C_element049  label="C_element : 026"  # scripted group (container) (typed FeaturePython)
  n = 5
  ref = C_element
FEATURE [App::DocumentObjectGroupPython] H_element042  label="H_element : 021"  # scripted group (container) (typed FeaturePython)
  n = 10
  ref = H_element
FEATURE [App::DocumentObjectGroupPython] N_element019  label="N_element : 2"  # scripted group (container) (typed FeaturePython)
  n = 2
  ref = N_element
FEATURE [App::DocumentObjectGroupPython] O_element046  label="O_element : 022"  # scripted group (container) (typed FeaturePython)
  n = 3
  ref = O_element
FEATURE [App::DocumentObjectGroupPython] G4_GLUTAMINE  # scripted group (container) (typed FeaturePython)
  Dunit = g/cm3
  Dvalue = 1.46
  Group = -> [C_element049,H_element042,N_element019,O_element046]
  conduct = 2
  density = 1
  expand = 3
  formula = G4_GLUTAMINE
  name = G4_GLUTAMINE
  specific = 4
FEATURE [App::DocumentObjectGroupPython] C_element050  label="C_element : 027"  # scripted group (container) (typed FeaturePython)
  n = 3
  ref = C_element
FEATURE [App::DocumentObjectGroupPython] H_element043  label="H_element : 022"  # scripted group (container) (typed FeaturePython)
  n = 8
  ref = H_element
FEATURE [App::DocumentObjectGroupPython] O_element047  label="O_element : 023"  # scripted group (container) (typed FeaturePython)
  n = 3
  ref = O_element
FEATURE [App::DocumentObjectGroupPython] G4_GLYCEROL  # scripted group (container) (typed FeaturePython)
  Dunit = g/cm3
  Dvalue = 1.2613
  Group = -> [C_element050,H_element043,O_element047]
  conduct = 2
  density = 1
  expand = 3
  formula = G4_GLYCEROL
  name = G4_GLYCEROL
  specific = 4
FEATURE [App::DocumentObjectGroupPython] C_element051  label="C_element : 028"  # scripted group (container) (typed FeaturePython)
  n = 5
  ref = C_element
FEATURE [App::DocumentObjectGroupPython] H_element044  label="H_element : 023"  # scripted group (container) (typed FeaturePython)
  n = 5
  ref = H_element
FEATURE [App::DocumentObjectGroupPython] N_element020  label="N_element : 009"  # scripted group (container) (typed FeaturePython)
  n = 5
  ref = N_element
FEATURE [App::DocumentObjectGroupPython] O_element048  label="O_element : 024"  # scripted group (container) (typed FeaturePython)
  n = 1
  ref = O_element
FEATURE [App::DocumentObjectGroupPython] G4_GUANINE  # scripted group (container) (typed FeaturePython)
  Dunit = g/cm3
  Dvalue = 2.2
  Group = -> [C_element051,H_element044,N_element020,O_element048]
  conduct = 2
  density = 1
  expand = 3
  formula = G4_GUANINE
  name = G4_GUANINE
  specific = 4
FEATURE [App::DocumentObjectGroupPython] Ca_element012  label="Ca_element : 006"  # scripted group (container) (typed FeaturePython)
  n = 1
  ref = Ca_element
FEATURE [App::DocumentObjectGroupPython] S_element014  label="S_element : 005"  # scripted group (container) (typed FeaturePython)
  n = 1
  ref = S_element
FEATURE [App::DocumentObjectGroupPython] O_element049  label="O_element : 6"  # scripted group (container) (typed FeaturePython)
  n = 6
  ref = O_element
FEATURE [App::DocumentObjectGroupPython] H_element045  label="H_element : 024"  # scripted group (container) (typed FeaturePython)
  n = 4
  ref = H_element
FEATURE [App::DocumentObjectGroupPython] G4_GYPSUM  # scripted group (container) (typed FeaturePython)
  Dunit = g/cm3
  Dvalue = 2.32
  Group = -> [Ca_element012,S_element014,O_element049,H_element045]
  conduct = 2
  density = 1
  expand = 3
  formula = G4_GYPSUM
  name = G4_GYPSUM
  specific = 4
FEATURE [App::DocumentObjectGroupPython] C_element052  label="C_element : 7"  # scripted group (container) (typed FeaturePython)
  n = 7
  ref = C_element
FEATURE [App::DocumentObjectGroupPython] H_element046  label="H_element : 16"  # scripted group (container) (typed FeaturePython)
  n = 16
  ref = H_element
FEATURE [App::DocumentObjectGroupPython] G4_N_HEPTANE  label="G4_N-HEPTANE"  # scripted group (container) (typed FeaturePython)
  Dunit = g/cm3
  Dvalue = 0.68376
  Group = -> [C_element052,H_element046]
  conduct = 2
  density = 1
  expand = 3
  formula = G4_N-HEPTANE
  name = G4_N-HEPTANE
  specific = 4
FEATURE [App::DocumentObjectGroupPython] C_element053  label="C_element : 029"  # scripted group (container) (typed FeaturePython)
  n = 6
  ref = C_element
FEATURE [App::DocumentObjectGroupPython] H_element047  label="H_element : 14"  # scripted group (container) (typed FeaturePython)
  n = 14
  ref = H_element
FEATURE [App::DocumentObjectGroupPython] G4_N_HEXANE  label="G4_N-HEXANE"  # scripted group (container) (typed FeaturePython)
  Dunit = g/cm3
  Dvalue = 0.6603
  Group = -> [C_element053,H_element047]
  conduct = 2
  density = 1
  expand = 3
  formula = G4_N-HEXANE
  name = G4_N-HEXANE
  specific = 4
FEATURE [App::DocumentObjectGroupPython] C_element054  label="C_element : 22"  # scripted group (container) (typed FeaturePython)
  n = 22
  ref = C_element
FEATURE [App::DocumentObjectGroupPython] H_element048  label="H_element : 025"  # scripted group (container) (typed FeaturePython)
  n = 10
  ref = H_element
FEATURE [App::DocumentObjectGroupPython] N_element021  label="N_element : 010"  # scripted group (container) (typed FeaturePython)
  n = 2
  ref = N_element
FEATURE [App::DocumentObjectGroupPython] O_element050  label="O_element : 025"  # scripted group (container) (typed FeaturePython)
  n = 5
  ref = O_element
FEATURE [App::DocumentObjectGroupPython] G4_KAPTON  # scripted group (container) (typed FeaturePython)
  Dunit = g/cm3
  Dvalue = 1.42
  Group = -> [C_element054,H_element048,N_element021,O_element050]
  conduct = 2
  density = 1
  expand = 3
  formula = G4_KAPTON
  name = G4_KAPTON
  specific = 4
FEATURE [App::DocumentObjectGroupPython] La_element001  label="La_element : 1"  # scripted group (container) (typed FeaturePython)
  n = 1
  ref = La_element
FEATURE [App::DocumentObjectGroupPython] Br_element003  label="Br_element : 002"  # scripted group (container) (typed FeaturePython)
  n = 1
  ref = Br_element
FEATURE [App::DocumentObjectGroupPython] O_element051  label="O_element : 026"  # scripted group (container) (typed FeaturePython)
  n = 1
  ref = O_element
FEATURE [App::DocumentObjectGroupPython] G4_LANTHANUM_OXYBROMIDE  # scripted group (container) (typed FeaturePython)
  Dunit = g/cm3
  Dvalue = 6.28
  Group = -> [La_element001,Br_element003,O_element051]
  conduct = 2
  density = 1
  expand = 3
  formula = G4_LANTHANUM_OXYBROMIDE
  name = G4_LANTHANUM_OXYBROMIDE
  specific = 4
FEATURE [App::DocumentObjectGroupPython] La_element002  label="La_element : 2"  # scripted group (container) (typed FeaturePython)
  n = 2
  ref = La_element
FEATURE [App::DocumentObjectGroupPython] O_element052  label="O_element : 027"  # scripted group (container) (typed FeaturePython)
  n = 2
  ref = O_element
FEATURE [App::DocumentObjectGroupPython] S_element015  label="S_element : 006"  # scripted group (container) (typed FeaturePython)
  n = 1
  ref = S_element
FEATURE [App::DocumentObjectGroupPython] G4_LANTHANUM_OXYSULFIDE  # scripted group (container) (typed FeaturePython)
  Dunit = g/cm3
  Dvalue = 5.86
  Group = -> [La_element002,O_element052,S_element015]
  conduct = 2
  density = 1
  expand = 3
  formula = G4_LANTHANUM_OXYSULFIDE
  name = G4_LANTHANUM_OXYSULFIDE
  specific = 4
FEATURE [App::DocumentObjectGroupPython] O_element053  label="O_element : 0.072"  # scripted group (container) (typed FeaturePython)
  n = 0.071682
FEATURE [App::DocumentObjectGroupPython] Pb_element002  label="Pb_element : 0.928"  # scripted group (container) (typed FeaturePython)
  n = 0.928318
FEATURE [App::DocumentObjectGroupPython] G4_LEAD_OXIDE  # scripted group (container) (typed FeaturePython)
  Dunit = g/cm3
  Dvalue = 9.53
  Group = -> [O_element053,Pb_element002]
  conduct = 2
  density = 1
  expand = 3
  formula = G4_LEAD_OXIDE
  name = G4_LEAD_OXIDE
  specific = 4
FEATURE [App::DocumentObjectGroupPython] Li_element001  label="Li_element : 1"  # scripted group (container) (typed FeaturePython)
  n = 1
  ref = Li_element
FEATURE [App::DocumentObjectGroupPython] N_element022  label="N_element : 011"  # scripted group (container) (typed FeaturePython)
  n = 1
  ref = N_element
FEATURE [App::DocumentObjectGroupPython] H_element049  label="H_element : 026"  # scripted group (container) (typed FeaturePython)
  n = 2
  ref = H_element
FEATURE [App::DocumentObjectGroupPython] G4_LITHIUM_AMIDE  # scripted group (container) (typed FeaturePython)
  Dunit = g/cm3
  Dvalue = 1.178
  Group = -> [Li_element001,N_element022,H_element049]
  conduct = 2
  density = 1
  expand = 3
  formula = G4_LITHIUM_AMIDE
  name = G4_LITHIUM_AMIDE
  specific = 4
FEATURE [App::DocumentObjectGroupPython] Li_element002  label="Li_element : 2"  # scripted group (container) (typed FeaturePython)
  n = 2
  ref = Li_element
FEATURE [App::DocumentObjectGroupPython] C_element055  label="C_element : 030"  # scripted group (container) (typed FeaturePython)
  n = 1
  ref = C_element
FEATURE [App::DocumentObjectGroupPython] O_element054  label="O_element : 028"  # scripted group (container) (typed FeaturePython)
  n = 3
  ref = O_element
FEATURE [App::DocumentObjectGroupPython] G4_LITHIUM_CARBONATE  # scripted group (container) (typed FeaturePython)
  Dunit = g/cm3
  Dvalue = 2.11
  Group = -> [Li_element002,C_element055,O_element054]
  conduct = 2
  density = 1
  expand = 3
  formula = G4_LITHIUM_CARBONATE
  name = G4_LITHIUM_CARBONATE
  specific = 4
FEATURE [App::DocumentObjectGroupPython] Li_element003  label="Li_element : 003"  # scripted group (container) (typed FeaturePython)
  n = 1
  ref = Li_element
FEATURE [App::DocumentObjectGroupPython] F_element012  label="F_element : 004"  # scripted group (container) (typed FeaturePython)
  n = 1
  ref = F_element
FEATURE [App::DocumentObjectGroupPython] G4_LITHIUM_FLUORIDE  # scripted group (container) (typed FeaturePython)
  Dunit = g/cm3
  Dvalue = 2.635
  Group = -> [Li_element003,F_element012]
  conduct = 2
  density = 1
  expand = 3
  formula = G4_LITHIUM_FLUORIDE
  name = G4_LITHIUM_FLUORIDE
  specific = 4
FEATURE [App::DocumentObjectGroupPython] Li_element004  label="Li_element : 004"  # scripted group (container) (typed FeaturePython)
  n = 1
  ref = Li_element
FEATURE [App::DocumentObjectGroupPython] H_element050  label="H_element : 027"  # scripted group (container) (typed FeaturePython)
  n = 1
  ref = H_element
FEATURE [App::DocumentObjectGroupPython] G4_LITHIUM_HYDRIDE  # scripted group (container) (typed FeaturePython)
  Dunit = g/cm3
  Dvalue = 0.82
  Group = -> [Li_element004,H_element050]
  conduct = 2
  density = 1
  expand = 3
  formula = G4_LITHIUM_HYDRIDE
  name = G4_LITHIUM_HYDRIDE
  specific = 4
FEATURE [App::DocumentObjectGroupPython] Li_element005  label="Li_element : 005"  # scripted group (container) (typed FeaturePython)
  n = 1
  ref = Li_element
FEATURE [App::DocumentObjectGroupPython] I_element003  label="I_element : 002"  # scripted group (container) (typed FeaturePython)
  n = 1
  ref = I_element
FEATURE [App::DocumentObjectGroupPython] G4_LITHIUM_IODIDE  # scripted group (container) (typed FeaturePython)
  Dunit = g/cm3
  Dvalue = 3.494
  Group = -> [Li_element005,I_element003]
  conduct = 2
  density = 1
  expand = 3
  formula = G4_LITHIUM_IODIDE
  name = G4_LITHIUM_IODIDE
  specific = 4
FEATURE [App::DocumentObjectGroupPython] Li_element006  label="Li_element : 006"  # scripted group (container) (typed FeaturePython)
  n = 2
  ref = Li_element
FEATURE [App::DocumentObjectGroupPython] O_element055  label="O_element : 029"  # scripted group (container) (typed FeaturePython)
  n = 1
  ref = O_element
FEATURE [App::DocumentObjectGroupPython] G4_LITHIUM_OXIDE  # scripted group (container) (typed FeaturePython)
  Dunit = g/cm3
  Dvalue = 2.013
  Group = -> [Li_element006,O_element055]
  conduct = 2
  density = 1
  expand = 3
  formula = G4_LITHIUM_OXIDE
  name = G4_LITHIUM_OXIDE
  specific = 4
FEATURE [App::DocumentObjectGroupPython] Li_element007  label="Li_element : 007"  # scripted group (container) (typed FeaturePython)
  n = 2
  ref = Li_element
FEATURE [App::DocumentObjectGroupPython] B_element005  label="B_element : 005"  # scripted group (container) (typed FeaturePython)
  n = 4
  ref = B_element
FEATURE [App::DocumentObjectGroupPython] O_element056  label="O_element : 7"  # scripted group (container) (typed FeaturePython)
  n = 7
  ref = O_element
FEATURE [App::DocumentObjectGroupPython] G4_LITHIUM_TETRABORATE  # scripted group (container) (typed FeaturePython)
  Dunit = g/cm3
  Dvalue = 2.44
  Group = -> [Li_element007,B_element005,O_element056]
  conduct = 2
  density = 1
  expand = 3
  formula = G4_LITHIUM_TETRABORATE
  name = G4_LITHIUM_TETRABORATE
  specific = 4
FEATURE [App::DocumentObjectGroupPython] H_element051  label="H_element : 0.105"  # scripted group (container) (typed FeaturePython)
  n = 0.105
FEATURE [App::DocumentObjectGroupPython] C_element056  label="C_element : 0.083"  # scripted group (container) (typed FeaturePython)
  n = 0.083
FEATURE [App::DocumentObjectGroupPython] N_element023  label="N_element : 0.023"  # scripted group (container) (typed FeaturePython)
  n = 0.023
FEATURE [App::DocumentObjectGroupPython] O_element057  label="O_element : 0.779"  # scripted group (container) (typed FeaturePython)
  n = 0.779
FEATURE [App::DocumentObjectGroupPython] Na_element010  label="Na_element : 0.097"  # scripted group (container) (typed FeaturePython)
  n = 0.002
FEATURE [App::DocumentObjectGroupPython] P_element006  label="P_element : 0.105"  # scripted group (container) (typed FeaturePython)
  n = 0.001
FEATURE [App::DocumentObjectGroupPython] S_element016  label="S_element : 0.017"  # scripted group (container) (typed FeaturePython)
  n = 0.002
FEATURE [App::DocumentObjectGroupPython] Cl_element014  label="Cl_element : 0.587"  # scripted group (container) (typed FeaturePython)
  n = 0.003
FEATURE [App::DocumentObjectGroupPython] K_element005  label="K_element : 0.015"  # scripted group (container) (typed FeaturePython)
  n = 0.002
FEATURE [App::DocumentObjectGroupPython] G4_LUNG_ICRP  # scripted group (container) (typed FeaturePython)
  Dunit = g/cm3
  Dvalue = 1.04
  Group = -> [H_element051,C_element056,N_element023,O_element057,Na_element010,P_element006,S_element016,Cl_element014,K_element005]
  conduct = 2
  density = 1
  expand = 3
  formula = G4_LUNG_ICRP
  name = G4_LUNG_ICRP
  specific = 4
FEATURE [App::DocumentObjectGroupPython] H_element052  label="H_element : 0.116"  # scripted group (container) (typed FeaturePython)
  n = 0.114318
FEATURE [App::DocumentObjectGroupPython] C_element057  label="C_element : 0.656"  # scripted group (container) (typed FeaturePython)
  n = 0.655824
FEATURE [App::DocumentObjectGroupPython] O_element058  label="O_element : 0.092"  # scripted group (container) (typed FeaturePython)
  n = 0.0921831
FEATURE [App::DocumentObjectGroupPython] Mg_element004  label="Mg_element : 0.135"  # scripted group (container) (typed FeaturePython)
  n = 0.134792
FEATURE [App::DocumentObjectGroupPython] Ca_element013  label="Ca_element : 0.003"  # scripted group (container) (typed FeaturePython)
  n = 0.002883
FEATURE [App::DocumentObjectGroupPython] G4_M3_WAX  # scripted group (container) (typed FeaturePython)
  Dunit = g/cm3
  Dvalue = 1.05
  Group = -> [H_element052,C_element057,O_element058,Mg_element004,Ca_element013]
  conduct = 2
  density = 1
  expand = 3
  formula = G4_M3_WAX
  name = G4_M3_WAX
  specific = 4
FEATURE [App::DocumentObjectGroupPython] Mg_element005  label="Mg_element : 1"  # scripted group (container) (typed FeaturePython)
  n = 1
  ref = Mg_element
FEATURE [App::DocumentObjectGroupPython] C_element058  label="C_element : 031"  # scripted group (container) (typed FeaturePython)
  n = 1
  ref = C_element
FEATURE [App::DocumentObjectGroupPython] O_element059  label="O_element : 030"  # scripted group (container) (typed FeaturePython)
  n = 3
  ref = O_element
FEATURE [App::DocumentObjectGroupPython] G4_MAGNESIUM_CARBONATE  # scripted group (container) (typed FeaturePython)
  Dunit = g/cm3
  Dvalue = 2.958
  Group = -> [Mg_element005,C_element058,O_element059]
  conduct = 2
  density = 1
  expand = 3
  formula = G4_MAGNESIUM_CARBONATE
  name = G4_MAGNESIUM_CARBONATE
  specific = 4
FEATURE [App::DocumentObjectGroupPython] Mg_element006  label="Mg_element : 002"  # scripted group (container) (typed FeaturePython)
  n = 1
  ref = Mg_element
FEATURE [App::DocumentObjectGroupPython] F_element013  label="F_element : 005"  # scripted group (container) (typed FeaturePython)
  n = 2
  ref = F_element
FEATURE [App::DocumentObjectGroupPython] G4_MAGNESIUM_FLUORIDE  # scripted group (container) (typed FeaturePython)
  Dunit = g/cm3
  Dvalue = 3
  Group = -> [Mg_element006,F_element013]
  conduct = 2
  density = 1
  expand = 3
  formula = G4_MAGNESIUM_FLUORIDE
  name = G4_MAGNESIUM_FLUORIDE
  specific = 4
FEATURE [App::DocumentObjectGroupPython] Mg_element007  label="Mg_element : 003"  # scripted group (container) (typed FeaturePython)
  n = 1
  ref = Mg_element
FEATURE [App::DocumentObjectGroupPython] O_element060  label="O_element : 031"  # scripted group (container) (typed FeaturePython)
  n = 1
  ref = O_element
FEATURE [App::DocumentObjectGroupPython] G4_MAGNESIUM_OXIDE  # scripted group (container) (typed FeaturePython)
  Dunit = g/cm3
  Dvalue = 3.58
  Group = -> [Mg_element007,O_element060]
  conduct = 2
  density = 1
  expand = 3
  formula = G4_MAGNESIUM_OXIDE
  name = G4_MAGNESIUM_OXIDE
  specific = 4
FEATURE [App::DocumentObjectGroupPython] Mg_element008  label="Mg_element : 004"  # scripted group (container) (typed FeaturePython)
  n = 1
  ref = Mg_element
FEATURE [App::DocumentObjectGroupPython] B_element006  label="B_element : 006"  # scripted group (container) (typed FeaturePython)
  n = 4
  ref = B_element
FEATURE [App::DocumentObjectGroupPython] O_element061  label="O_element : 032"  # scripted group (container) (typed FeaturePython)
  n = 7
  ref = O_element
FEATURE [App::DocumentObjectGroupPython] G4_MAGNESIUM_TETRABORATE  # scripted group (container) (typed FeaturePython)
  Dunit = g/cm3
  Dvalue = 2.53
  Group = -> [Mg_element008,B_element006,O_element061]
  conduct = 2
  density = 1
  expand = 3
  formula = G4_MAGNESIUM_TETRABORATE
  name = G4_MAGNESIUM_TETRABORATE
  specific = 4
FEATURE [App::DocumentObjectGroupPython] Hg_element001  label="Hg_element : 1"  # scripted group (container) (typed FeaturePython)
  n = 1
  ref = Hg_element
FEATURE [App::DocumentObjectGroupPython] I_element004  label="I_element : 2"  # scripted group (container) (typed FeaturePython)
  n = 2
  ref = I_element
FEATURE [App::DocumentObjectGroupPython] G4_MERCURIC_IODIDE  # scripted group (container) (typed FeaturePython)
  Dunit = g/cm3
  Dvalue = 6.36
  Group = -> [Hg_element001,I_element004]
  conduct = 2
  density = 1
  expand = 3
  formula = G4_MERCURIC_IODIDE
  name = G4_MERCURIC_IODIDE
  specific = 4
FEATURE [App::DocumentObjectGroupPython] C_element059  label="C_element : 032"  # scripted group (container) (typed FeaturePython)
  n = 1
  ref = C_element
FEATURE [App::DocumentObjectGroupPython] H_element053  label="H_element : 028"  # scripted group (container) (typed FeaturePython)
  n = 4
  ref = H_element
FEATURE [App::DocumentObjectGroupPython] G4_METHANE  # scripted group (container) (typed FeaturePython)
  Dunit = g/cm3
  Dvalue = 0.000667151
  Group = -> [C_element059,H_element053]
  conduct = 2
  density = 1
  expand = 3
  formula = G4_METHANE
  name = G4_METHANE
  specific = 4
FEATURE [App::DocumentObjectGroupPython] C_element060  label="C_element : 033"  # scripted group (container) (typed FeaturePython)
  n = 1
  ref = C_element
FEATURE [App::DocumentObjectGroupPython] H_element054  label="H_element : 029"  # scripted group (container) (typed FeaturePython)
  n = 4
  ref = H_element
FEATURE [App::DocumentObjectGroupPython] O_element062  label="O_element : 033"  # scripted group (container) (typed FeaturePython)
  n = 1
  ref = O_element
FEATURE [App::DocumentObjectGroupPython] G4_METHANOL  # scripted group (container) (typed FeaturePython)
  Dunit = g/cm3
  Dvalue = 0.7914
  Group = -> [C_element060,H_element054,O_element062]
  conduct = 2
  density = 1
  expand = 3
  formula = G4_METHANOL
  name = G4_METHANOL
  specific = 4
FEATURE [App::DocumentObjectGroupPython] H_element055  label="H_element : 0.134"  # scripted group (container) (typed FeaturePython)
  n = 0.13404
FEATURE [App::DocumentObjectGroupPython] C_element061  label="C_element : 0.778"  # scripted group (container) (typed FeaturePython)
  n = 0.77796
FEATURE [App::DocumentObjectGroupPython] O_element063  label="O_element : 0.035"  # scripted group (container) (typed FeaturePython)
  n = 0.03502
FEATURE [App::DocumentObjectGroupPython] Mg_element009  label="Mg_element : 0.039"  # scripted group (container) (typed FeaturePython)
  n = 0.038594
FEATURE [App::DocumentObjectGroupPython] Ti_element002  label="Ti_element : 0.014"  # scripted group (container) (typed FeaturePython)
  n = 0.014386
FEATURE [App::DocumentObjectGroupPython] G4_MIX_D_WAX  # scripted group (container) (typed FeaturePython)
  Dunit = g/cm3
  Dvalue = 0.99
  Group = -> [H_element055,C_element061,O_element063,Mg_element009,Ti_element002]
  conduct = 2
  density = 1
  expand = 3
  formula = G4_MIX_D_WAX
  name = G4_MIX_D_WAX
  specific = 4
FEATURE [App::DocumentObjectGroupPython] H_element056  label="H_element : 0.135"  # scripted group (container) (typed FeaturePython)
  n = 0.081192
FEATURE [App::DocumentObjectGroupPython] C_element062  label="C_element : 0.583"  # scripted group (container) (typed FeaturePython)
  n = 0.583442
FEATURE [App::DocumentObjectGroupPython] N_element024  label="N_element : 0.018"  # scripted group (container) (typed FeaturePython)
  n = 0.017798
FEATURE [App::DocumentObjectGroupPython] O_element064  label="O_element : 0.186"  # scripted group (container) (typed FeaturePython)
  n = 0.186381
FEATURE [App::DocumentObjectGroupPython] Mg_element010  label="Mg_element : 0.130"  # scripted group (container) (typed FeaturePython)
  n = 0.130287
FEATURE [App::DocumentObjectGroupPython] Cl_element015  label="Cl_element : 0.588"  # scripted group (container) (typed FeaturePython)
  n = 0.0009
FEATURE [App::DocumentObjectGroupPython] G4_MS20_TISSUE  # scripted group (container) (typed FeaturePython)
  Dunit = g/cm3
  Dvalue = 1
  Group = -> [H_element056,C_element062,N_element024,O_element064,Mg_element010,Cl_element015]
  conduct = 2
  density = 1
  expand = 3
  formula = G4_MS20_TISSUE
  name = G4_MS20_TISSUE
  specific = 4
FEATURE [App::DocumentObjectGroupPython] H_element057  label="H_element : 0.136"  # scripted group (container) (typed FeaturePython)
  n = 0.102
FEATURE [App::DocumentObjectGroupPython] C_element063  label="C_element : 0.143"  # scripted group (container) (typed FeaturePython)
  n = 0.143
FEATURE [App::DocumentObjectGroupPython] N_element025  label="N_element : 0.034"  # scripted group (container) (typed FeaturePython)
  n = 0.034
FEATURE [App::DocumentObjectGroupPython] O_element065  label="O_element : 0.710"  # scripted group (container) (typed FeaturePython)
  n = 0.71
FEATURE [App::DocumentObjectGroupPython] Na_element011  label="Na_element : 0.098"  # scripted group (container) (typed FeaturePython)
  n = 0.001
FEATURE [App::DocumentObjectGroupPython] P_element007  label="P_element : 0.002"  # scripted group (container) (typed FeaturePython)
  n = 0.002
FEATURE [App::DocumentObjectGroupPython] S_element017  label="S_element : 0.018"  # scripted group (container) (typed FeaturePython)
  n = 0.003
FEATURE [App::DocumentObjectGroupPython] Cl_element016  label="Cl_element : 0.589"  # scripted group (container) (typed FeaturePython)
  n = 0.001
FEATURE [App::DocumentObjectGroupPython] K_element006  label="K_element : 0.004"  # scripted group (container) (typed FeaturePython)
  n = 0.004
FEATURE [App::DocumentObjectGroupPython] G4_MUSCLE_SKELETAL_ICRP  # scripted group (container) (typed FeaturePython)
  Dunit = g/cm3
  Dvalue = 1.05
  Group = -> [H_element057,C_element063,N_element025,O_element065,Na_element011,P_element007,S_element017,Cl_element016,K_element006]
  conduct = 2
  density = 1
  expand = 3
  formula = G4_MUSCLE_SKELETAL_ICRP
  name = G4_MUSCLE_SKELETAL_ICRP
  specific = 4
FEATURE [App::DocumentObjectGroupPython] H_element058  label="H_element : 0.137"  # scripted group (container) (typed FeaturePython)
  n = 0.102102
FEATURE [App::DocumentObjectGroupPython] C_element064  label="C_element : 0.123"  # scripted group (container) (typed FeaturePython)
  n = 0.123123
FEATURE [App::DocumentObjectGroupPython] N_element026  label="N_element : 0.756"  # scripted group (container) (typed FeaturePython)
  n = 0.035035
FEATURE [App::DocumentObjectGroupPython] O_element066  label="O_element : 0.730"  # scripted group (container) (typed FeaturePython)
  n = 0.72973
FEATURE [App::DocumentObjectGroupPython] Na_element012  label="Na_element : 0.099"  # scripted group (container) (typed FeaturePython)
  n = 0.001001
FEATURE [App::DocumentObjectGroupPython] P_element008  label="P_element : 0.106"  # scripted group (container) (typed FeaturePython)
  n = 0.002002
FEATURE [App::DocumentObjectGroupPython] S_element018  label="S_element : 0.019"  # scripted group (container) (typed FeaturePython)
  n = 0.004004
FEATURE [App::DocumentObjectGroupPython] K_element007  label="K_element : 0.016"  # scripted group (container) (typed FeaturePython)
  n = 0.003003
FEATURE [App::DocumentObjectGroupPython] G4_MUSCLE_STRIATED_ICRU  # scripted group (container) (typed FeaturePython)
  Dunit = g/cm3
  Dvalue = 1.04
  Group = -> [H_element058,C_element064,N_element026,O_element066,Na_element012,P_element008,S_element018,K_element007]
  conduct = 2
  density = 1
  expand = 3
  formula = G4_MUSCLE_STRIATED_ICRU
  name = G4_MUSCLE_STRIATED_ICRU
  specific = 4
FEATURE [App::DocumentObjectGroupPython] H_element059  label="H_element : 0.098"  # scripted group (container) (typed FeaturePython)
  n = 0.0982341
FEATURE [App::DocumentObjectGroupPython] C_element065  label="C_element : 0.156"  # scripted group (container) (typed FeaturePython)
  n = 0.156214
FEATURE [App::DocumentObjectGroupPython] N_element027  label="N_element : 0.757"  # scripted group (container) (typed FeaturePython)
  n = 0.035451
FEATURE [App::DocumentObjectGroupPython] O_element067  label="O_element : 0.880"  # scripted group (container) (typed FeaturePython)
  n = 0.710101
FEATURE [App::DocumentObjectGroupPython] G4_MUSCLE_WITH_SUCROSE  # scripted group (container) (typed FeaturePython)
  Dunit = g/cm3
  Dvalue = 1.11
  Group = -> [H_element059,C_element065,N_element027,O_element067]
  conduct = 2
  density = 1
  expand = 3
  formula = G4_MUSCLE_WITH_SUCROSE
  name = G4_MUSCLE_WITH_SUCROSE
  specific = 4
FEATURE [App::DocumentObjectGroupPython] H_element060  label="H_element : 0.138"  # scripted group (container) (typed FeaturePython)
  n = 0.101969
FEATURE [App::DocumentObjectGroupPython] C_element066  label="C_element : 0.120"  # scripted group (container) (typed FeaturePython)
  n = 0.120058
FEATURE [App::DocumentObjectGroupPython] N_element028  label="N_element : 0.758"  # scripted group (container) (typed FeaturePython)
  n = 0.035451
FEATURE [App::DocumentObjectGroupPython] O_element068  label="O_element : 0.743"  # scripted group (container) (typed FeaturePython)
  n = 0.742522
FEATURE [App::DocumentObjectGroupPython] G4_MUSCLE_WITHOUT_SUCROSE  # scripted group (container) (typed FeaturePython)
  Dunit = g/cm3
  Dvalue = 1.07
  Group = -> [H_element060,C_element066,N_element028,O_element068]
  conduct = 2
  density = 1
  expand = 3
  formula = G4_MUSCLE_WITHOUT_SUCROSE
  name = G4_MUSCLE_WITHOUT_SUCROSE
  specific = 4
FEATURE [App::DocumentObjectGroupPython] C_element067  label="C_element : 10"  # scripted group (container) (typed FeaturePython)
  n = 10
  ref = C_element
FEATURE [App::DocumentObjectGroupPython] H_element061  label="H_element : 030"  # scripted group (container) (typed FeaturePython)
  n = 8
  ref = H_element
FEATURE [App::DocumentObjectGroupPython] G4_NAPHTHALENE  # scripted group (container) (typed FeaturePython)
  Dunit = g/cm3
  Dvalue = 1.145
  Group = -> [C_element067,H_element061]
  conduct = 2
  density = 1
  expand = 3
  formula = G4_NAPHTHALENE
  name = G4_NAPHTHALENE
  specific = 4
FEATURE [App::DocumentObjectGroupPython] C_element068  label="C_element : 034"  # scripted group (container) (typed FeaturePython)
  n = 6
  ref = C_element
FEATURE [App::DocumentObjectGroupPython] H_element062  label="H_element : 031"  # scripted group (container) (typed FeaturePython)
  n = 5
  ref = H_element
FEATURE [App::DocumentObjectGroupPython] N_element029  label="N_element : 012"  # scripted group (container) (typed FeaturePython)
  n = 1
  ref = N_element
FEATURE [App::DocumentObjectGroupPython] O_element069  label="O_element : 034"  # scripted group (container) (typed FeaturePython)
  n = 2
  ref = O_element
FEATURE [App::DocumentObjectGroupPython] G4_NITROBENZENE  # scripted group (container) (typed FeaturePython)
  Dunit = g/cm3
  Dvalue = 1.19867
  Group = -> [C_element068,H_element062,N_element029,O_element069]
  conduct = 2
  density = 1
  expand = 3
  formula = G4_NITROBENZENE
  name = G4_NITROBENZENE
  specific = 4
FEATURE [App::DocumentObjectGroupPython] N_element030  label="N_element : 013"  # scripted group (container) (typed FeaturePython)
  n = 2
  ref = N_element
FEATURE [App::DocumentObjectGroupPython] O_element070  label="O_element : 035"  # scripted group (container) (typed FeaturePython)
  n = 1
  ref = O_element
FEATURE [App::DocumentObjectGroupPython] G4_NITROUS_OXIDE  # scripted group (container) (typed FeaturePython)
  Dunit = g/cm3
  Dvalue = 0.00183094
  Group = -> [N_element030,O_element070]
  conduct = 2
  density = 1
  expand = 3
  formula = G4_NITROUS_OXIDE
  name = G4_NITROUS_OXIDE
  specific = 4
FEATURE [App::DocumentObjectGroupPython] H_element063  label="H_element : 0.104"  # scripted group (container) (typed FeaturePython)
  n = 0.103509
FEATURE [App::DocumentObjectGroupPython] C_element069  label="C_element : 0.648"  # scripted group (container) (typed FeaturePython)
  n = 0.648416
FEATURE [App::DocumentObjectGroupPython] N_element031  label="N_element : 0.100"  # scripted group (container) (typed FeaturePython)
  n = 0.0995361
FEATURE [App::DocumentObjectGroupPython] O_element071  label="O_element : 0.149"  # scripted group (container) (typed FeaturePython)
  n = 0.148539
FEATURE [App::DocumentObjectGroupPython] G4_NYLON_8062  label="G4_NYLON-8062"  # scripted group (container) (typed FeaturePython)
  Dunit = g/cm3
  Dvalue = 1.08
  Group = -> [H_element063,C_element069,N_element031,O_element071]
  conduct = 2
  density = 1
  expand = 3
  formula = G4_NYLON-8062
  name = G4_NYLON-8062
  specific = 4
FEATURE [App::DocumentObjectGroupPython] C_element070  label="C_element : 035"  # scripted group (container) (typed FeaturePython)
  n = 6
  ref = C_element
FEATURE [App::DocumentObjectGroupPython] H_element064  label="H_element : 11"  # scripted group (container) (typed FeaturePython)
  n = 11
  ref = H_element
FEATURE [App::DocumentObjectGroupPython] N_element032  label="N_element : 014"  # scripted group (container) (typed FeaturePython)
  n = 1
  ref = N_element
FEATURE [App::DocumentObjectGroupPython] O_element072  label="O_element : 036"  # scripted group (container) (typed FeaturePython)
  n = 1
  ref = O_element
FEATURE [App::DocumentObjectGroupPython] G4_NYLON_6_6  label="G4_NYLON-6-6"  # scripted group (container) (typed FeaturePython)
  Dunit = g/cm3
  Dvalue = 1.14
  Group = -> [C_element070,H_element064,N_element032,O_element072]
  conduct = 2
  density = 1
  expand = 3
  formula = G4_NYLON-6-6
  name = G4_NYLON-6-6
  specific = 4
FEATURE [App::DocumentObjectGroupPython] H_element065  label="H_element : 0.139"  # scripted group (container) (typed FeaturePython)
  n = 0.107062
FEATURE [App::DocumentObjectGroupPython] C_element071  label="C_element : 0.680"  # scripted group (container) (typed FeaturePython)
  n = 0.680449
FEATURE [App::DocumentObjectGroupPython] N_element033  label="N_element : 0.099"  # scripted group (container) (typed FeaturePython)
  n = 0.099189
FEATURE [App::DocumentObjectGroupPython] O_element073  label="O_element : 0.113"  # scripted group (container) (typed FeaturePython)
  n = 0.1133
FEATURE [App::DocumentObjectGroupPython] G4_NYLON_6_10  label="G4_NYLON-6-10"  # scripted group (container) (typed FeaturePython)
  Dunit = g/cm3
  Dvalue = 1.14
  Group = -> [H_element065,C_element071,N_element033,O_element073]
  conduct = 2
  density = 1
  expand = 3
  formula = G4_NYLON-6-10
  name = G4_NYLON-6-10
  specific = 4
FEATURE [App::DocumentObjectGroupPython] H_element066  label="H_element : 0.140"  # scripted group (container) (typed FeaturePython)
  n = 0.115476
FEATURE [App::DocumentObjectGroupPython] C_element072  label="C_element : 0.721"  # scripted group (container) (typed FeaturePython)
  n = 0.720818
FEATURE [App::DocumentObjectGroupPython] N_element034  label="N_element : 0.076"  # scripted group (container) (typed FeaturePython)
  n = 0.0764169
FEATURE [App::DocumentObjectGroupPython] O_element074  label="O_element : 0.087"  # scripted group (container) (typed FeaturePython)
  n = 0.0872889
FEATURE [App::DocumentObjectGroupPython] G4_NYLON_11_RILSAN  label="G4_NYLON-11_RILSAN"  # scripted group (container) (typed FeaturePython)
  Dunit = g/cm3
  Dvalue = 1.425
  Group = -> [H_element066,C_element072,N_element034,O_element074]
  conduct = 2
  density = 1
  expand = 3
  formula = G4_NYLON-11_RILSAN
  name = G4_NYLON-11_RILSAN
  specific = 4
FEATURE [App::DocumentObjectGroupPython] C_element073  label="C_element : 8"  # scripted group (container) (typed FeaturePython)
  n = 8
  ref = C_element
FEATURE [App::DocumentObjectGroupPython] H_element067  label="H_element : 18"  # scripted group (container) (typed FeaturePython)
  n = 18
  ref = H_element
FEATURE [App::DocumentObjectGroupPython] G4_OCTANE  # scripted group (container) (typed FeaturePython)
  Dunit = g/cm3
  Dvalue = 0.7026
  Group = -> [C_element073,H_element067]
  conduct = 2
  density = 1
  expand = 3
  formula = G4_OCTANE
  name = G4_OCTANE
  specific = 4
FEATURE [App::DocumentObjectGroupPython] C_element074  label="C_element : 25"  # scripted group (container) (typed FeaturePython)
  n = 25
  ref = C_element
FEATURE [App::DocumentObjectGroupPython] H_element068  label="H_element : 52"  # scripted group (container) (typed FeaturePython)
  n = 52
  ref = H_element
FEATURE [App::DocumentObjectGroupPython] G4_PARAFFIN  # scripted group (container) (typed FeaturePython)
  Dunit = g/cm3
  Dvalue = 0.93
  Group = -> [C_element074,H_element068]
  conduct = 2
  density = 1
  expand = 3
  formula = G4_PARAFFIN
  name = G4_PARAFFIN
  specific = 4
FEATURE [App::DocumentObjectGroupPython] C_element075  label="C_element : 036"  # scripted group (container) (typed FeaturePython)
  n = 5
  ref = C_element
FEATURE [App::DocumentObjectGroupPython] H_element069  label="H_element : 032"  # scripted group (container) (typed FeaturePython)
  n = 12
  ref = H_element
FEATURE [App::DocumentObjectGroupPython] G4_N_PENTANE  label="G4_N-PENTANE"  # scripted group (container) (typed FeaturePython)
  Dunit = g/cm3
  Dvalue = 0.6262
  Group = -> [C_element075,H_element069]
  conduct = 2
  density = 1
  expand = 3
  formula = G4_N-PENTANE
  name = G4_N-PENTANE
  specific = 4
FEATURE [App::DocumentObjectGroupPython] H_element070  label="H_element : 0.014"  # scripted group (container) (typed FeaturePython)
  n = 0.0141
FEATURE [App::DocumentObjectGroupPython] C_element076  label="C_element : 0.072"  # scripted group (container) (typed FeaturePython)
  n = 0.072261
FEATURE [App::DocumentObjectGroupPython] N_element035  label="N_element : 0.019"  # scripted group (container) (typed FeaturePython)
  n = 0.01932
FEATURE [App::DocumentObjectGroupPython] O_element075  label="O_element : 0.066"  # scripted group (container) (typed FeaturePython)
  n = 0.066101
FEATURE [App::DocumentObjectGroupPython] S_element019  label="S_element : 0.020"  # scripted group (container) (typed FeaturePython)
  n = 0.00189
FEATURE [App::DocumentObjectGroupPython] Br_element004  label="Br_element : 0.349"  # scripted group (container) (typed FeaturePython)
  n = 0.349103
FEATURE [App::DocumentObjectGroupPython] Ag_element001  label="Ag_element : 0.474"  # scripted group (container) (typed FeaturePython)
  n = 0.474105
FEATURE [App::DocumentObjectGroupPython] I_element005  label="I_element : 0.003"  # scripted group (container) (typed FeaturePython)
  n = 0.00312
FEATURE [App::DocumentObjectGroupPython] G4_PHOTO_EMULSION  # scripted group (container) (typed FeaturePython)
  Dunit = g/cm3
  Dvalue = 3.815
  Group = -> [H_element070,C_element076,N_element035,O_element075,S_element019,Br_element004,Ag_element001,I_element005]
  conduct = 2
  density = 1
  expand = 3
  formula = G4_PHOTO_EMULSION
  name = G4_PHOTO_EMULSION
  specific = 4
FEATURE [App::DocumentObjectGroupPython] C_element077  label="C_element : 9"  # scripted group (container) (typed FeaturePython)
  n = 9
  ref = C_element
FEATURE [App::DocumentObjectGroupPython] H_element071  label="H_element : 033"  # scripted group (container) (typed FeaturePython)
  n = 10
  ref = H_element
FEATURE [App::DocumentObjectGroupPython] G4_PLASTIC_SC_VINYLTOLUENE  # scripted group (container) (typed FeaturePython)
  Dunit = g/cm3
  Dvalue = 1.032
  Group = -> [C_element077,H_element071]
  conduct = 2
  density = 1
  expand = 3
  formula = G4_PLASTIC_SC_VINYLTOLUENE
  name = G4_PLASTIC_SC_VINYLTOLUENE
  specific = 4
FEATURE [App::DocumentObjectGroupPython] Pu_element001  label="Pu_element : 1"  # scripted group (container) (typed FeaturePython)
  n = 1
  ref = Pu_element
FEATURE [App::DocumentObjectGroupPython] O_element076  label="O_element : 037"  # scripted group (container) (typed FeaturePython)
  n = 2
  ref = O_element
FEATURE [App::DocumentObjectGroupPython] G4_PLUTONIUM_DIOXIDE  # scripted group (container) (typed FeaturePython)
  Dunit = g/cm3
  Dvalue = 11.46
  Group = -> [Pu_element001,O_element076]
  conduct = 2
  density = 1
  expand = 3
  formula = G4_PLUTONIUM_DIOXIDE
  name = G4_PLUTONIUM_DIOXIDE
  specific = 4
FEATURE [App::DocumentObjectGroupPython] C_element078  label="C_element : 037"  # scripted group (container) (typed FeaturePython)
  n = 3
  ref = C_element
FEATURE [App::DocumentObjectGroupPython] H_element072  label="H_element : 034"  # scripted group (container) (typed FeaturePython)
  n = 3
  ref = H_element
FEATURE [App::DocumentObjectGroupPython] N_element036  label="N_element : 015"  # scripted group (container) (typed FeaturePython)
  n = 1
  ref = N_element
FEATURE [App::DocumentObjectGroupPython] G4_POLYACRYLONITRILE  # scripted group (container) (typed FeaturePython)
  Dunit = g/cm3
  Dvalue = 1.17
  Group = -> [C_element078,H_element072,N_element036]
  conduct = 2
  density = 1
  expand = 3
  formula = G4_POLYACRYLONITRILE
  name = G4_POLYACRYLONITRILE
  specific = 4
FEATURE [App::DocumentObjectGroupPython] C_element079  label="C_element : 16"  # scripted group (container) (typed FeaturePython)
  n = 16
  ref = C_element
FEATURE [App::DocumentObjectGroupPython] H_element073  label="H_element : 035"  # scripted group (container) (typed FeaturePython)
  n = 14
  ref = H_element
FEATURE [App::DocumentObjectGroupPython] O_element077  label="O_element : 038"  # scripted group (container) (typed FeaturePython)
  n = 3
  ref = O_element
FEATURE [App::DocumentObjectGroupPython] G4_POLYCARBONATE  # scripted group (container) (typed FeaturePython)
  Dunit = g/cm3
  Dvalue = 1.2
  Group = -> [C_element079,H_element073,O_element077]
  conduct = 2
  density = 1
  expand = 3
  formula = G4_POLYCARBONATE
  name = G4_POLYCARBONATE
  specific = 4
FEATURE [App::DocumentObjectGroupPython] C_element080  label="C_element : 038"  # scripted group (container) (typed FeaturePython)
  n = 8
  ref = C_element
FEATURE [App::DocumentObjectGroupPython] H_element074  label="H_element : 036"  # scripted group (container) (typed FeaturePython)
  n = 7
  ref = H_element
FEATURE [App::DocumentObjectGroupPython] Cl_element017  label="Cl_element : 007"  # scripted group (container) (typed FeaturePython)
  n = 1
  ref = Cl_element
FEATURE [App::DocumentObjectGroupPython] G4_POLYCHLOROSTYRENE  # scripted group (container) (typed FeaturePython)
  Dunit = g/cm3
  Dvalue = 1.3
  Group = -> [C_element080,H_element074,Cl_element017]
  conduct = 2
  density = 1
  expand = 3
  formula = G4_POLYCHLOROSTYRENE
  name = G4_POLYCHLOROSTYRENE
  specific = 4
FEATURE [App::DocumentObjectGroupPython] C_element081  label="C_element : 039"  # scripted group (container) (typed FeaturePython)
  n = 1
  ref = C_element
FEATURE [App::DocumentObjectGroupPython] H_element075  label="H_element : 037"  # scripted group (container) (typed FeaturePython)
  n = 2
  ref = H_element
FEATURE [App::DocumentObjectGroupPython] G4_POLYETHYLENE  # scripted group (container) (typed FeaturePython)
  Dunit = g/cm3
  Dvalue = 0.94
  Group = -> [C_element081,H_element075]
  conduct = 2
  density = 1
  expand = 3
  formula = G4_POLYETHYLENE
  name = G4_POLYETHYLENE
  specific = 4
FEATURE [App::DocumentObjectGroupPython] C_element082  label="C_element : 040"  # scripted group (container) (typed FeaturePython)
  n = 10
  ref = C_element
FEATURE [App::DocumentObjectGroupPython] H_element076  label="H_element : 038"  # scripted group (container) (typed FeaturePython)
  n = 8
  ref = H_element
FEATURE [App::DocumentObjectGroupPython] O_element078  label="O_element : 039"  # scripted group (container) (typed FeaturePython)
  n = 4
  ref = O_element
FEATURE [App::DocumentObjectGroupPython] G4_MYLAR  # scripted group (container) (typed FeaturePython)
  Dunit = g/cm3
  Dvalue = 1.4
  Group = -> [C_element082,H_element076,O_element078]
  conduct = 2
  density = 1
  expand = 3
  formula = G4_MYLAR
  name = G4_MYLAR
  specific = 4
FEATURE [App::DocumentObjectGroupPython] C_element083  label="C_element : 041"  # scripted group (container) (typed FeaturePython)
  n = 5
  ref = C_element
FEATURE [App::DocumentObjectGroupPython] H_element077  label="H_element : 039"  # scripted group (container) (typed FeaturePython)
  n = 8
  ref = H_element
FEATURE [App::DocumentObjectGroupPython] O_element079  label="O_element : 040"  # scripted group (container) (typed FeaturePython)
  n = 2
  ref = O_element
FEATURE [App::DocumentObjectGroupPython] G4_PLEXIGLASS  # scripted group (container) (typed FeaturePython)
  Dunit = g/cm3
  Dvalue = 1.19
  Group = -> [C_element083,H_element077,O_element079]
  conduct = 2
  density = 1
  expand = 3
  formula = G4_PLEXIGLASS
  name = G4_PLEXIGLASS
  specific = 4
FEATURE [App::DocumentObjectGroupPython] C_element084  label="C_element : 042"  # scripted group (container) (typed FeaturePython)
  n = 1
  ref = C_element
FEATURE [App::DocumentObjectGroupPython] H_element078  label="H_element : 040"  # scripted group (container) (typed FeaturePython)
  n = 2
  ref = H_element
FEATURE [App::DocumentObjectGroupPython] O_element080  label="O_element : 041"  # scripted group (container) (typed FeaturePython)
  n = 1
  ref = O_element
FEATURE [App::DocumentObjectGroupPython] G4_POLYOXYMETHYLENE  # scripted group (container) (typed FeaturePython)
  Dunit = g/cm3
  Dvalue = 1.425
  Group = -> [C_element084,H_element078,O_element080]
  conduct = 2
  density = 1
  expand = 3
  formula = G4_POLYOXYMETHYLENE
  name = G4_POLYOXYMETHYLENE
  specific = 4
FEATURE [App::DocumentObjectGroupPython] C_element085  label="C_element : 043"  # scripted group (container) (typed FeaturePython)
  n = 2
  ref = C_element
FEATURE [App::DocumentObjectGroupPython] H_element079  label="H_element : 041"  # scripted group (container) (typed FeaturePython)
  n = 4
  ref = H_element
FEATURE [App::DocumentObjectGroupPython] G4_POLYPROPYLENE  # scripted group (container) (typed FeaturePython)
  Dunit = g/cm3
  Dvalue = 0.9
  Group = -> [C_element085,H_element079]
  conduct = 2
  density = 1
  expand = 3
  formula = G4_POLYPROPYLENE
  name = G4_POLYPROPYLENE
  specific = 4
FEATURE [App::DocumentObjectGroupPython] C_element086  label="C_element : 044"  # scripted group (container) (typed FeaturePython)
  n = 8
  ref = C_element
FEATURE [App::DocumentObjectGroupPython] H_element080  label="H_element : 042"  # scripted group (container) (typed FeaturePython)
  n = 8
  ref = H_element
FEATURE [App::DocumentObjectGroupPython] G4_POLYSTYRENE  # scripted group (container) (typed FeaturePython)
  Dunit = g/cm3
  Dvalue = 1.06
  Group = -> [C_element086,H_element080]
  conduct = 2
  density = 1
  expand = 3
  formula = G4_POLYSTYRENE
  name = G4_POLYSTYRENE
  specific = 4
FEATURE [App::DocumentObjectGroupPython] C_element087  label="C_element : 045"  # scripted group (container) (typed FeaturePython)
  n = 2
  ref = C_element
FEATURE [App::DocumentObjectGroupPython] F_element014  label="F_element : 4"  # scripted group (container) (typed FeaturePython)
  n = 4
  ref = F_element
FEATURE [App::DocumentObjectGroupPython] G4_TEFLON  # scripted group (container) (typed FeaturePython)
  Dunit = g/cm3
  Dvalue = 2.2
  Group = -> [C_element087,F_element014]
  conduct = 2
  density = 1
  expand = 3
  formula = G4_TEFLON
  name = G4_TEFLON
  specific = 4
FEATURE [App::DocumentObjectGroupPython] C_element088  label="C_element : 046"  # scripted group (container) (typed FeaturePython)
  n = 2
  ref = C_element
FEATURE [App::DocumentObjectGroupPython] F_element015  label="F_element : 006"  # scripted group (container) (typed FeaturePython)
  n = 3
  ref = F_element
FEATURE [App::DocumentObjectGroupPython] Cl_element018  label="Cl_element : 008"  # scripted group (container) (typed FeaturePython)
  n = 1
  ref = Cl_element
FEATURE [App::DocumentObjectGroupPython] G4_POLYTRIFLUOROCHLOROETHYLENE  # scripted group (container) (typed FeaturePython)
  Dunit = g/cm3
  Dvalue = 2.1
  Group = -> [C_element088,F_element015,Cl_element018]
  conduct = 2
  density = 1
  expand = 3
  formula = G4_POLYTRIFLUOROCHLOROETHYLENE
  name = G4_POLYTRIFLUOROCHLOROETHYLENE
  specific = 4
FEATURE [App::DocumentObjectGroupPython] C_element089  label="C_element : 047"  # scripted group (container) (typed FeaturePython)
  n = 4
  ref = C_element
FEATURE [App::DocumentObjectGroupPython] H_element081  label="H_element : 043"  # scripted group (container) (typed FeaturePython)
  n = 6
  ref = H_element
FEATURE [App::DocumentObjectGroupPython] O_element081  label="O_element : 042"  # scripted group (container) (typed FeaturePython)
  n = 2
  ref = O_element
FEATURE [App::DocumentObjectGroupPython] G4_POLYVINYL_ACETATE  # scripted group (container) (typed FeaturePython)
  Dunit = g/cm3
  Dvalue = 1.19
  Group = -> [C_element089,H_element081,O_element081]
  conduct = 2
  density = 1
  expand = 3
  formula = G4_POLYVINYL_ACETATE
  name = G4_POLYVINYL_ACETATE
  specific = 4
FEATURE [App::DocumentObjectGroupPython] C_element090  label="C_element : 048"  # scripted group (container) (typed FeaturePython)
  n = 2
  ref = C_element
FEATURE [App::DocumentObjectGroupPython] H_element082  label="H_element : 044"  # scripted group (container) (typed FeaturePython)
  n = 4
  ref = H_element
FEATURE [App::DocumentObjectGroupPython] O_element082  label="O_element : 043"  # scripted group (container) (typed FeaturePython)
  n = 1
  ref = O_element
FEATURE [App::DocumentObjectGroupPython] G4_POLYVINYL_ALCOHOL  # scripted group (container) (typed FeaturePython)
  Dunit = g/cm3
  Dvalue = 1.3
  Group = -> [C_element090,H_element082,O_element082]
  conduct = 2
  density = 1
  expand = 3
  formula = G4_POLYVINYL_ALCOHOL
  name = G4_POLYVINYL_ALCOHOL
  specific = 4
FEATURE [App::DocumentObjectGroupPython] C_element091  label="C_element : 049"  # scripted group (container) (typed FeaturePython)
  n = 8
  ref = C_element
FEATURE [App::DocumentObjectGroupPython] H_element083  label="H_element : 045"  # scripted group (container) (typed FeaturePython)
  n = 14
  ref = H_element
FEATURE [App::DocumentObjectGroupPython] O_element083  label="O_element : 044"  # scripted group (container) (typed FeaturePython)
  n = 2
  ref = O_element
FEATURE [App::DocumentObjectGroupPython] G4_POLYVINYL_BUTYRAL  # scripted group (container) (typed FeaturePython)
  Dunit = g/cm3
  Dvalue = 1.12
  Group = -> [C_element091,H_element083,O_element083]
  conduct = 2
  density = 1
  expand = 3
  formula = G4_POLYVINYL_BUTYRAL
  name = G4_POLYVINYL_BUTYRAL
  specific = 4
FEATURE [App::DocumentObjectGroupPython] C_element092  label="C_element : 050"  # scripted group (container) (typed FeaturePython)
  n = 2
  ref = C_element
FEATURE [App::DocumentObjectGroupPython] H_element084  label="H_element : 046"  # scripted group (container) (typed FeaturePython)
  n = 3
  ref = H_element
FEATURE [App::DocumentObjectGroupPython] Cl_element019  label="Cl_element : 009"  # scripted group (container) (typed FeaturePython)
  n = 1
  ref = Cl_element
FEATURE [App::DocumentObjectGroupPython] G4_POLYVINYL_CHLORIDE  # scripted group (container) (typed FeaturePython)
  Dunit = g/cm3
  Dvalue = 1.3
  Group = -> [C_element092,H_element084,Cl_element019]
  conduct = 2
  density = 1
  expand = 3
  formula = G4_POLYVINYL_CHLORIDE
  name = G4_POLYVINYL_CHLORIDE
  specific = 4
FEATURE [App::DocumentObjectGroupPython] C_element093  label="C_element : 051"  # scripted group (container) (typed FeaturePython)
  n = 2
  ref = C_element
FEATURE [App::DocumentObjectGroupPython] H_element085  label="H_element : 047"  # scripted group (container) (typed FeaturePython)
  n = 2
  ref = H_element
FEATURE [App::DocumentObjectGroupPython] Cl_element020  label="Cl_element : 010"  # scripted group (container) (typed FeaturePython)
  n = 2
  ref = Cl_element
FEATURE [App::DocumentObjectGroupPython] G4_POLYVINYLIDENE_CHLORIDE  # scripted group (container) (typed FeaturePython)
  Dunit = g/cm3
  Dvalue = 1.7
  Group = -> [C_element093,H_element085,Cl_element020]
  conduct = 2
  density = 1
  expand = 3
  formula = G4_POLYVINYLIDENE_CHLORIDE
  name = G4_POLYVINYLIDENE_CHLORIDE
  specific = 4
FEATURE [App::DocumentObjectGroupPython] C_element094  label="C_element : 052"  # scripted group (container) (typed FeaturePython)
  n = 2
  ref = C_element
FEATURE [App::DocumentObjectGroupPython] H_element086  label="H_element : 048"  # scripted group (container) (typed FeaturePython)
  n = 2
  ref = H_element
FEATURE [App::DocumentObjectGroupPython] F_element016  label="F_element : 007"  # scripted group (container) (typed FeaturePython)
  n = 2
  ref = F_element
FEATURE [App::DocumentObjectGroupPython] G4_POLYVINYLIDENE_FLUORIDE  # scripted group (container) (typed FeaturePython)
  Dunit = g/cm3
  Dvalue = 1.76
  Group = -> [C_element094,H_element086,F_element016]
  conduct = 2
  density = 1
  expand = 3
  formula = G4_POLYVINYLIDENE_FLUORIDE
  name = G4_POLYVINYLIDENE_FLUORIDE
  specific = 4
FEATURE [App::DocumentObjectGroupPython] C_element095  label="C_element : 053"  # scripted group (container) (typed FeaturePython)
  n = 6
  ref = C_element
FEATURE [App::DocumentObjectGroupPython] H_element087  label="H_element : 9"  # scripted group (container) (typed FeaturePython)
  n = 9
  ref = H_element
FEATURE [App::DocumentObjectGroupPython] N_element037  label="N_element : 016"  # scripted group (container) (typed FeaturePython)
  n = 1
  ref = N_element
FEATURE [App::DocumentObjectGroupPython] O_element084  label="O_element : 045"  # scripted group (container) (typed FeaturePython)
  n = 1
  ref = O_element
FEATURE [App::DocumentObjectGroupPython] G4_POLYVINYL_PYRROLIDONE  # scripted group (container) (typed FeaturePython)
  Dunit = g/cm3
  Dvalue = 1.25
  Group = -> [C_element095,H_element087,N_element037,O_element084]
  conduct = 2
  density = 1
  expand = 3
  formula = G4_POLYVINYL_PYRROLIDONE
  name = G4_POLYVINYL_PYRROLIDONE
  specific = 4
FEATURE [App::DocumentObjectGroupPython] K_element008  label="K_element : 1"  # scripted group (container) (typed FeaturePython)
  n = 1
  ref = K_element
FEATURE [App::DocumentObjectGroupPython] I_element006  label="I_element : 003"  # scripted group (container) (typed FeaturePython)
  n = 1
  ref = I_element
FEATURE [App::DocumentObjectGroupPython] G4_POTASSIUM_IODIDE  # scripted group (container) (typed FeaturePython)
  Dunit = g/cm3
  Dvalue = 3.13
  Group = -> [K_element008,I_element006]
  conduct = 2
  density = 1
  expand = 3
  formula = G4_POTASSIUM_IODIDE
  name = G4_POTASSIUM_IODIDE
  specific = 4
FEATURE [App::DocumentObjectGroupPython] K_element009  label="K_element : 2"  # scripted group (container) (typed FeaturePython)
  n = 2
  ref = K_element
FEATURE [App::DocumentObjectGroupPython] O_element085  label="O_element : 046"  # scripted group (container) (typed FeaturePython)
  n = 1
  ref = O_element
FEATURE [App::DocumentObjectGroupPython] G4_POTASSIUM_OXIDE  # scripted group (container) (typed FeaturePython)
  Dunit = g/cm3
  Dvalue = 2.32
  Group = -> [K_element009,O_element085]
  conduct = 2
  density = 1
  expand = 3
  formula = G4_POTASSIUM_OXIDE
  name = G4_POTASSIUM_OXIDE
  specific = 4
FEATURE [App::DocumentObjectGroupPython] C_element096  label="C_element : 054"  # scripted group (container) (typed FeaturePython)
  n = 3
  ref = C_element
FEATURE [App::DocumentObjectGroupPython] H_element088  label="H_element : 049"  # scripted group (container) (typed FeaturePython)
  n = 8
  ref = H_element
FEATURE [App::DocumentObjectGroupPython] G4_PROPANE  # scripted group (container) (typed FeaturePython)
  Dunit = g/cm3
  Dvalue = 0.00187939
  Group = -> [C_element096,H_element088]
  conduct = 2
  density = 1
  expand = 3
  formula = G4_PROPANE
  name = G4_PROPANE
  specific = 4
FEATURE [App::DocumentObjectGroupPython] C_element097  label="C_element : 055"  # scripted group (container) (typed FeaturePython)
  n = 3
  ref = C_element
FEATURE [App::DocumentObjectGroupPython] H_element089  label="H_element : 050"  # scripted group (container) (typed FeaturePython)
  n = 8
  ref = H_element
FEATURE [App::DocumentObjectGroupPython] G4_lPROPANE  # scripted group (container) (typed FeaturePython)
  Dunit = g/cm3
  Dvalue = 0.43
  Group = -> [C_element097,H_element089]
  conduct = 2
  density = 1
  expand = 3
  formula = G4_lPROPANE
  name = G4_lPROPANE
  specific = 4
FEATURE [App::DocumentObjectGroupPython] C_element098  label="C_element : 056"  # scripted group (container) (typed FeaturePython)
  n = 3
  ref = C_element
FEATURE [App::DocumentObjectGroupPython] H_element090  label="H_element : 051"  # scripted group (container) (typed FeaturePython)
  n = 8
  ref = H_element
FEATURE [App::DocumentObjectGroupPython] O_element086  label="O_element : 047"  # scripted group (container) (typed FeaturePython)
  n = 1
  ref = O_element
FEATURE [App::DocumentObjectGroupPython] G4_N_PROPYL_ALCOHOL  label="G4_N-PROPYL_ALCOHOL"  # scripted group (container) (typed FeaturePython)
  Dunit = g/cm3
  Dvalue = 0.8035
  Group = -> [C_element098,H_element090,O_element086]
  conduct = 2
  density = 1
  expand = 3
  formula = G4_N-PROPYL_ALCOHOL
  name = G4_N-PROPYL_ALCOHOL
  specific = 4
FEATURE [App::DocumentObjectGroupPython] C_element099  label="C_element : 057"  # scripted group (container) (typed FeaturePython)
  n = 5
  ref = C_element
FEATURE [App::DocumentObjectGroupPython] H_element091  label="H_element : 052"  # scripted group (container) (typed FeaturePython)
  n = 5
  ref = H_element
FEATURE [App::DocumentObjectGroupPython] N_element038  label="N_element : 017"  # scripted group (container) (typed FeaturePython)
  n = 1
  ref = N_element
FEATURE [App::DocumentObjectGroupPython] G4_PYRIDINE  # scripted group (container) (typed FeaturePython)
  Dunit = g/cm3
  Dvalue = 0.9819
  Group = -> [C_element099,H_element091,N_element038]
  conduct = 2
  density = 1
  expand = 3
  formula = G4_PYRIDINE
  name = G4_PYRIDINE
  specific = 4
FEATURE [App::DocumentObjectGroupPython] H_element092  label="H_element : 0.144"  # scripted group (container) (typed FeaturePython)
  n = 0.143711
FEATURE [App::DocumentObjectGroupPython] C_element100  label="C_element : 0.856"  # scripted group (container) (typed FeaturePython)
  n = 0.856289
FEATURE [App::DocumentObjectGroupPython] G4_RUBBER_BUTYL  # scripted group (container) (typed FeaturePython)
  Dunit = g/cm3
  Dvalue = 0.92
  Group = -> [H_element092,C_element100]
  conduct = 2
  density = 1
  expand = 3
  formula = G4_RUBBER_BUTYL
  name = G4_RUBBER_BUTYL
  specific = 4
FEATURE [App::DocumentObjectGroupPython] H_element093  label="H_element : 0.118"  # scripted group (container) (typed FeaturePython)
  n = 0.118371
FEATURE [App::DocumentObjectGroupPython] C_element101  label="C_element : 0.882"  # scripted group (container) (typed FeaturePython)
  n = 0.881629
FEATURE [App::DocumentObjectGroupPython] G4_RUBBER_NATURAL  # scripted group (container) (typed FeaturePython)
  Dunit = g/cm3
  Dvalue = 0.92
  Group = -> [H_element093,C_element101]
  conduct = 2
  density = 1
  expand = 3
  formula = G4_RUBBER_NATURAL
  name = G4_RUBBER_NATURAL
  specific = 4
FEATURE [App::DocumentObjectGroupPython] H_element094  label="H_element : 0.145"  # scripted group (container) (typed FeaturePython)
  n = 0.05692
FEATURE [App::DocumentObjectGroupPython] C_element102  label="C_element : 0.543"  # scripted group (container) (typed FeaturePython)
  n = 0.542646
FEATURE [App::DocumentObjectGroupPython] Cl_element021  label="Cl_element : 0.400"  # scripted group (container) (typed FeaturePython)
  n = 0.400434
FEATURE [App::DocumentObjectGroupPython] G4_RUBBER_NEOPRENE  # scripted group (container) (typed FeaturePython)
  Dunit = g/cm3
  Dvalue = 1.23
  Group = -> [H_element094,C_element102,Cl_element021]
  conduct = 2
  density = 1
  expand = 3
  formula = G4_RUBBER_NEOPRENE
  name = G4_RUBBER_NEOPRENE
  specific = 4
FEATURE [App::DocumentObjectGroupPython] Si_element006  label="Si_element : 1"  # scripted group (container) (typed FeaturePython)
  n = 1
  ref = Si_element
FEATURE [App::DocumentObjectGroupPython] O_element087  label="O_element : 048"  # scripted group (container) (typed FeaturePython)
  n = 2
  ref = O_element
FEATURE [App::DocumentObjectGroupPython] G4_SILICON_DIOXIDE  # scripted group (container) (typed FeaturePython)
  Dunit = g/cm3
  Dvalue = 2.32
  Group = -> [Si_element006,O_element087]
  conduct = 2
  density = 1
  expand = 3
  formula = G4_SILICON_DIOXIDE
  name = G4_SILICON_DIOXIDE
  specific = 4
FEATURE [App::DocumentObjectGroupPython] Ag_element002  label="Ag_element : 1"  # scripted group (container) (typed FeaturePython)
  n = 1
  ref = Ag_element
FEATURE [App::DocumentObjectGroupPython] Br_element005  label="Br_element : 003"  # scripted group (container) (typed FeaturePython)
  n = 1
  ref = Br_element
FEATURE [App::DocumentObjectGroupPython] G4_SILVER_BROMIDE  # scripted group (container) (typed FeaturePython)
  Dunit = g/cm3
  Dvalue = 6.473
  Group = -> [Ag_element002,Br_element005]
  conduct = 2
  density = 1
  expand = 3
  formula = G4_SILVER_BROMIDE
  name = G4_SILVER_BROMIDE
  specific = 4
FEATURE [App::DocumentObjectGroupPython] Ag_element003  label="Ag_element : 002"  # scripted group (container) (typed FeaturePython)
  n = 1
  ref = Ag_element
FEATURE [App::DocumentObjectGroupPython] Cl_element022  label="Cl_element : 011"  # scripted group (container) (typed FeaturePython)
  n = 1
  ref = Cl_element
FEATURE [App::DocumentObjectGroupPython] G4_SILVER_CHLORIDE  # scripted group (container) (typed FeaturePython)
  Dunit = g/cm3
  Dvalue = 5.56
  Group = -> [Ag_element003,Cl_element022]
  conduct = 2
  density = 1
  expand = 3
  formula = G4_SILVER_CHLORIDE
  name = G4_SILVER_CHLORIDE
  specific = 4
FEATURE [App::DocumentObjectGroupPython] Br_element006  label="Br_element : 0.423"  # scripted group (container) (typed FeaturePython)
  n = 0.422895
FEATURE [App::DocumentObjectGroupPython] Ag_element004  label="Ag_element : 0.574"  # scripted group (container) (typed FeaturePython)
  n = 0.573748
FEATURE [App::DocumentObjectGroupPython] I_element007  label="I_element : 0.649"  # scripted group (container) (typed FeaturePython)
  n = 0.003357
FEATURE [App::DocumentObjectGroupPython] G4_SILVER_HALIDES  # scripted group (container) (typed FeaturePython)
  Dunit = g/cm3
  Dvalue = 6.47
  Group = -> [Br_element006,Ag_element004,I_element007]
  conduct = 2
  density = 1
  expand = 3
  formula = G4_SILVER_HALIDES
  name = G4_SILVER_HALIDES
  specific = 4
FEATURE [App::DocumentObjectGroupPython] Ag_element005  label="Ag_element : 003"  # scripted group (container) (typed FeaturePython)
  n = 1
  ref = Ag_element
FEATURE [App::DocumentObjectGroupPython] I_element008  label="I_element : 004"  # scripted group (container) (typed FeaturePython)
  n = 1
  ref = I_element
FEATURE [App::DocumentObjectGroupPython] G4_SILVER_IODIDE  # scripted group (container) (typed FeaturePython)
  Dunit = g/cm3
  Dvalue = 6.01
  Group = -> [Ag_element005,I_element008]
  conduct = 2
  density = 1
  expand = 3
  formula = G4_SILVER_IODIDE
  name = G4_SILVER_IODIDE
  specific = 4
FEATURE [App::DocumentObjectGroupPython] H_element095  label="H_element : 0.100"  # scripted group (container) (typed FeaturePython)
  n = 0.1
FEATURE [App::DocumentObjectGroupPython] C_element103  label="C_element : 0.204"  # scripted group (container) (typed FeaturePython)
  n = 0.204
FEATURE [App::DocumentObjectGroupPython] N_element039  label="N_element : 0.759"  # scripted group (container) (typed FeaturePython)
  n = 0.042
FEATURE [App::DocumentObjectGroupPython] O_element088  label="O_element : 0.645"  # scripted group (container) (typed FeaturePython)
  n = 0.645
FEATURE [App::DocumentObjectGroupPython] Na_element013  label="Na_element : 0.100"  # scripted group (container) (typed FeaturePython)
  n = 0.002
FEATURE [App::DocumentObjectGroupPython] P_element009  label="P_element : 0.107"  # scripted group (container) (typed FeaturePython)
  n = 0.001
FEATURE [App::DocumentObjectGroupPython] S_element020  label="S_element : 0.021"  # scripted group (container) (typed FeaturePython)
  n = 0.002
FEATURE [App::DocumentObjectGroupPython] Cl_element023  label="Cl_element : 0.590"  # scripted group (container) (typed FeaturePython)
  n = 0.003
FEATURE [App::DocumentObjectGroupPython] K_element010  label="K_element : 0.001"  # scripted group (container) (typed FeaturePython)
  n = 0.001
FEATURE [App::DocumentObjectGroupPython] G4_SKIN_ICRP  # scripted group (container) (typed FeaturePython)
  Dunit = g/cm3
  Dvalue = 1.09
  Group = -> [H_element095,C_element103,N_element039,O_element088,Na_element013,P_element009,S_element020,Cl_element023,K_element010]
  conduct = 2
  density = 1
  expand = 3
  formula = G4_SKIN_ICRP
  name = G4_SKIN_ICRP
  specific = 4
FEATURE [App::DocumentObjectGroupPython] Na_element014  label="Na_element : 2"  # scripted group (container) (typed FeaturePython)
  n = 2
  ref = Na_element
FEATURE [App::DocumentObjectGroupPython] C_element104  label="C_element : 058"  # scripted group (container) (typed FeaturePython)
  n = 1
  ref = C_element
FEATURE [App::DocumentObjectGroupPython] O_element089  label="O_element : 049"  # scripted group (container) (typed FeaturePython)
  n = 3
  ref = O_element
FEATURE [App::DocumentObjectGroupPython] G4_SODIUM_CARBONATE  # scripted group (container) (typed FeaturePython)
  Dunit = g/cm3
  Dvalue = 2.532
  Group = -> [Na_element014,C_element104,O_element089]
  conduct = 2
  density = 1
  expand = 3
  formula = G4_SODIUM_CARBONATE
  name = G4_SODIUM_CARBONATE
  specific = 4
FEATURE [App::DocumentObjectGroupPython] Na_element015  label="Na_element : 1"  # scripted group (container) (typed FeaturePython)
  n = 1
  ref = Na_element
FEATURE [App::DocumentObjectGroupPython] I_element009  label="I_element : 005"  # scripted group (container) (typed FeaturePython)
  n = 1
  ref = I_element
FEATURE [App::DocumentObjectGroupPython] G4_SODIUM_IODIDE  # scripted group (container) (typed FeaturePython)
  Dunit = g/cm3
  Dvalue = 3.667
  Group = -> [Na_element015,I_element009]
  conduct = 2
  density = 1
  expand = 3
  formula = G4_SODIUM_IODIDE
  name = G4_SODIUM_IODIDE
  specific = 4
FEATURE [App::DocumentObjectGroupPython] Na_element016  label="Na_element : 003"  # scripted group (container) (typed FeaturePython)
  n = 2
  ref = Na_element
FEATURE [App::DocumentObjectGroupPython] O_element090  label="O_element : 050"  # scripted group (container) (typed FeaturePython)
  n = 1
  ref = O_element
FEATURE [App::DocumentObjectGroupPython] G4_SODIUM_MONOXIDE  # scripted group (container) (typed FeaturePython)
  Dunit = g/cm3
  Dvalue = 2.27
  Group = -> [Na_element016,O_element090]
  conduct = 2
  density = 1
  expand = 3
  formula = G4_SODIUM_MONOXIDE
  name = G4_SODIUM_MONOXIDE
  specific = 4
FEATURE [App::DocumentObjectGroupPython] Na_element017  label="Na_element : 004"  # scripted group (container) (typed FeaturePython)
  n = 1
  ref = Na_element
FEATURE [App::DocumentObjectGroupPython] N_element040  label="N_element : 018"  # scripted group (container) (typed FeaturePython)
  n = 1
  ref = N_element
FEATURE [App::DocumentObjectGroupPython] O_element091  label="O_element : 051"  # scripted group (container) (typed FeaturePython)
  n = 3
  ref = O_element
FEATURE [App::DocumentObjectGroupPython] G4_SODIUM_NITRATE  # scripted group (container) (typed FeaturePython)
  Dunit = g/cm3
  Dvalue = 2.261
  Group = -> [Na_element017,N_element040,O_element091]
  conduct = 2
  density = 1
  expand = 3
  formula = G4_SODIUM_NITRATE
  name = G4_SODIUM_NITRATE
  specific = 4
FEATURE [App::DocumentObjectGroupPython] C_element105  label="C_element : 059"  # scripted group (container) (typed FeaturePython)
  n = 14
  ref = C_element
FEATURE [App::DocumentObjectGroupPython] H_element096  label="H_element : 053"  # scripted group (container) (typed FeaturePython)
  n = 12
  ref = H_element
FEATURE [App::DocumentObjectGroupPython] G4_STILBENE  # scripted group (container) (typed FeaturePython)
  Dunit = g/cm3
  Dvalue = 0.9707
  Group = -> [C_element105,H_element096]
  conduct = 2
  density = 1
  expand = 3
  formula = G4_STILBENE
  name = G4_STILBENE
  specific = 4
FEATURE [App::DocumentObjectGroupPython] C_element106  label="C_element : 12"  # scripted group (container) (typed FeaturePython)
  n = 12
  ref = C_element
FEATURE [App::DocumentObjectGroupPython] H_element097  label="H_element : 22"  # scripted group (container) (typed FeaturePython)
  n = 22
  ref = H_element
FEATURE [App::DocumentObjectGroupPython] O_element092  label="O_element : 11"  # scripted group (container) (typed FeaturePython)
  n = 11
  ref = O_element
FEATURE [App::DocumentObjectGroupPython] G4_SUCROSE  # scripted group (container) (typed FeaturePython)
  Dunit = g/cm3
  Dvalue = 1.5805
  Group = -> [C_element106,H_element097,O_element092]
  conduct = 2
  density = 1
  expand = 3
  formula = G4_SUCROSE
  name = G4_SUCROSE
  specific = 4
FEATURE [App::DocumentObjectGroupPython] C_element107  label="C_element : 18"  # scripted group (container) (typed FeaturePython)
  n = 18
  ref = C_element
FEATURE [App::DocumentObjectGroupPython] H_element098  label="H_element : 054"  # scripted group (container) (typed FeaturePython)
  n = 14
  ref = H_element
FEATURE [App::DocumentObjectGroupPython] G4_TERPHENYL  # scripted group (container) (typed FeaturePython)
  Dunit = g/cm3
  Dvalue = 1.24
  Group = -> [C_element107,H_element098]
  conduct = 2
  density = 1
  expand = 3
  formula = G4_TERPHENYL
  name = G4_TERPHENYL
  specific = 4
FEATURE [App::DocumentObjectGroupPython] H_element099  label="H_element : 0.146"  # scripted group (container) (typed FeaturePython)
  n = 0.106
FEATURE [App::DocumentObjectGroupPython] C_element108  label="C_element : 0.883"  # scripted group (container) (typed FeaturePython)
  n = 0.099
FEATURE [App::DocumentObjectGroupPython] N_element041  label="N_element : 0.020"  # scripted group (container) (typed FeaturePython)
  n = 0.02
FEATURE [App::DocumentObjectGroupPython] O_element093  label="O_element : 0.766"  # scripted group (container) (typed FeaturePython)
  n = 0.766
FEATURE [App::DocumentObjectGroupPython] Na_element018  label="Na_element : 0.101"  # scripted group (container) (typed FeaturePython)
  n = 0.002
FEATURE [App::DocumentObjectGroupPython] P_element010  label="P_element : 0.108"  # scripted group (container) (typed FeaturePython)
  n = 0.001
FEATURE [App::DocumentObjectGroupPython] S_element021  label="S_element : 0.022"  # scripted group (container) (typed FeaturePython)
  n = 0.002
FEATURE [App::DocumentObjectGroupPython] Cl_element024  label="Cl_element : 0.002"  # scripted group (container) (typed FeaturePython)
  n = 0.002
FEATURE [App::DocumentObjectGroupPython] K_element011  label="K_element : 0.017"  # scripted group (container) (typed FeaturePython)
  n = 0.002
FEATURE [App::DocumentObjectGroupPython] G4_TESTIS_ICRP  # scripted group (container) (typed FeaturePython)
  Dunit = g/cm3
  Dvalue = 1.04
  Group = -> [H_element099,C_element108,N_element041,O_element093,Na_element018,P_element010,S_element021,Cl_element024,K_element011]
  conduct = 2
  density = 1
  expand = 3
  formula = G4_TESTIS_ICRP
  name = G4_TESTIS_ICRP
  specific = 4
FEATURE [App::DocumentObjectGroupPython] C_element109  label="C_element : 060"  # scripted group (container) (typed FeaturePython)
  n = 2
  ref = C_element
FEATURE [App::DocumentObjectGroupPython] Cl_element025  label="Cl_element : 012"  # scripted group (container) (typed FeaturePython)
  n = 4
  ref = Cl_element
FEATURE [App::DocumentObjectGroupPython] G4_TETRACHLOROETHYLENE  # scripted group (container) (typed FeaturePython)
  Dunit = g/cm3
  Dvalue = 1.625
  Group = -> [C_element109,Cl_element025]
  conduct = 2
  density = 1
  expand = 3
  formula = G4_TETRACHLOROETHYLENE
  name = G4_TETRACHLOROETHYLENE
  specific = 4
FEATURE [App::DocumentObjectGroupPython] Tl_element001  label="Tl_element : 1"  # scripted group (container) (typed FeaturePython)
  n = 1
  ref = Tl_element
FEATURE [App::DocumentObjectGroupPython] Cl_element026  label="Cl_element : 013"  # scripted group (container) (typed FeaturePython)
  n = 1
  ref = Cl_element
FEATURE [App::DocumentObjectGroupPython] G4_THALLIUM_CHLORIDE  # scripted group (container) (typed FeaturePython)
  Dunit = g/cm3
  Dvalue = 7.004
  Group = -> [Tl_element001,Cl_element026]
  conduct = 2
  density = 1
  expand = 3
  formula = G4_THALLIUM_CHLORIDE
  name = G4_THALLIUM_CHLORIDE
  specific = 4
FEATURE [App::DocumentObjectGroupPython] H_element100  label="H_element : 0.147"  # scripted group (container) (typed FeaturePython)
  n = 0.105
FEATURE [App::DocumentObjectGroupPython] C_element110  label="C_element : 0.256"  # scripted group (container) (typed FeaturePython)
  n = 0.256
FEATURE [App::DocumentObjectGroupPython] N_element042  label="N_element : 0.760"  # scripted group (container) (typed FeaturePython)
  n = 0.027
FEATURE [App::DocumentObjectGroupPython] O_element094  label="O_element : 0.602"  # scripted group (container) (typed FeaturePython)
  n = 0.602
FEATURE [App::DocumentObjectGroupPython] Na_element019  label="Na_element : 0.102"  # scripted group (container) (typed FeaturePython)
  n = 0.001
FEATURE [App::DocumentObjectGroupPython] P_element011  label="P_element : 0.109"  # scripted group (container) (typed FeaturePython)
  n = 0.002
FEATURE [App::DocumentObjectGroupPython] S_element022  label="S_element : 0.023"  # scripted group (container) (typed FeaturePython)
  n = 0.003
FEATURE [App::DocumentObjectGroupPython] Cl_element027  label="Cl_element : 0.591"  # scripted group (container) (typed FeaturePython)
  n = 0.002
FEATURE [App::DocumentObjectGroupPython] K_element012  label="K_element : 0.018"  # scripted group (container) (typed FeaturePython)
  n = 0.002
FEATURE [App::DocumentObjectGroupPython] G4_TISSUE_SOFT_ICRP  # scripted group (container) (typed FeaturePython)
  Dunit = g/cm3
  Dvalue = 1.03
  Group = -> [H_element100,C_element110,N_element042,O_element094,Na_element019,P_element011,S_element022,Cl_element027,K_element012]
  conduct = 2
  density = 1
  expand = 3
  formula = G4_TISSUE_SOFT_ICRP
  name = G4_TISSUE_SOFT_ICRP
  specific = 4
FEATURE [App::DocumentObjectGroupPython] H_element101  label="H_element : 0.148"  # scripted group (container) (typed FeaturePython)
  n = 0.101
FEATURE [App::DocumentObjectGroupPython] C_element111  label="C_element : 0.111"  # scripted group (container) (typed FeaturePython)
  n = 0.111
FEATURE [App::DocumentObjectGroupPython] N_element043  label="N_element : 0.026"  # scripted group (container) (typed FeaturePython)
  n = 0.026
FEATURE [App::DocumentObjectGroupPython] O_element095  label="O_element : 0.762"  # scripted group (container) (typed FeaturePython)
  n = 0.762
FEATURE [App::DocumentObjectGroupPython] G4_TISSUE_SOFT_ICRU_4  label="G4_TISSUE_SOFT_ICRU-4"  # scripted group (container) (typed FeaturePython)
  Dunit = g/cm3
  Dvalue = 1
  Group = -> [H_element101,C_element111,N_element043,O_element095]
  conduct = 2
  density = 1
  expand = 3
  formula = G4_TISSUE_SOFT_ICRU-4
  name = G4_TISSUE_SOFT_ICRU-4
  specific = 4
FEATURE [App::DocumentObjectGroupPython] H_element102  label="H_element : 0.149"  # scripted group (container) (typed FeaturePython)
  n = 0.101869
FEATURE [App::DocumentObjectGroupPython] C_element112  label="C_element : 0.456"  # scripted group (container) (typed FeaturePython)
  n = 0.456179
FEATURE [App::DocumentObjectGroupPython] N_element044  label="N_element : 0.761"  # scripted group (container) (typed FeaturePython)
  n = 0.035172
FEATURE [App::DocumentObjectGroupPython] O_element096  label="O_element : 0.407"  # scripted group (container) (typed FeaturePython)
  n = 0.40678
FEATURE [App::DocumentObjectGroupPython] G4_TISSUE_METHANE  label="G4_TISSUE-METHANE"  # scripted group (container) (typed FeaturePython)
  Dunit = g/cm3
  Dvalue = 0.00106409
  Group = -> [H_element102,C_element112,N_element044,O_element096]
  conduct = 2
  density = 1
  expand = 3
  formula = G4_TISSUE-METHANE
  name = G4_TISSUE-METHANE
  specific = 4
FEATURE [App::DocumentObjectGroupPython] H_element103  label="H_element : 0.103"  # scripted group (container) (typed FeaturePython)
  n = 0.102672
FEATURE [App::DocumentObjectGroupPython] C_element113  label="C_element : 0.569"  # scripted group (container) (typed FeaturePython)
  n = 0.56894
FEATURE [App::DocumentObjectGroupPython] N_element045  label="N_element : 0.762"  # scripted group (container) (typed FeaturePython)
  n = 0.035022
FEATURE [App::DocumentObjectGroupPython] O_element097  label="O_element : 0.293"  # scripted group (container) (typed FeaturePython)
  n = 0.293366
FEATURE [App::DocumentObjectGroupPython] G4_TISSUE_PROPANE  label="G4_TISSUE-PROPANE"  # scripted group (container) (typed FeaturePython)
  Dunit = g/cm3
  Dvalue = 0.00182628
  Group = -> [H_element103,C_element113,N_element045,O_element097]
  conduct = 2
  density = 1
  expand = 3
  formula = G4_TISSUE-PROPANE
  name = G4_TISSUE-PROPANE
  specific = 4
FEATURE [App::DocumentObjectGroupPython] Ti_element003  label="Ti_element : 1"  # scripted group (container) (typed FeaturePython)
  n = 1
  ref = Ti_element
FEATURE [App::DocumentObjectGroupPython] O_element098  label="O_element : 052"  # scripted group (container) (typed FeaturePython)
  n = 2
  ref = O_element
FEATURE [App::DocumentObjectGroupPython] G4_TITANIUM_DIOXIDE  # scripted group (container) (typed FeaturePython)
  Dunit = g/cm3
  Dvalue = 4.26
  Group = -> [Ti_element003,O_element098]
  conduct = 2
  density = 1
  expand = 3
  formula = G4_TITANIUM_DIOXIDE
  name = G4_TITANIUM_DIOXIDE
  specific = 4
FEATURE [App::DocumentObjectGroupPython] C_element114  label="C_element : 061"  # scripted group (container) (typed FeaturePython)
  n = 7
  ref = C_element
FEATURE [App::DocumentObjectGroupPython] H_element104  label="H_element : 055"  # scripted group (container) (typed FeaturePython)
  n = 8
  ref = H_element
FEATURE [App::DocumentObjectGroupPython] G4_TOLUENE  # scripted group (container) (typed FeaturePython)
  Dunit = g/cm3
  Dvalue = 0.8669
  Group = -> [C_element114,H_element104]
  conduct = 2
  density = 1
  expand = 3
  formula = G4_TOLUENE
  name = G4_TOLUENE
  specific = 4
FEATURE [App::DocumentObjectGroupPython] C_element115  label="C_element : 062"  # scripted group (container) (typed FeaturePython)
  n = 2
  ref = C_element
FEATURE [App::DocumentObjectGroupPython] H_element105  label="H_element : 056"  # scripted group (container) (typed FeaturePython)
  n = 1
  ref = H_element
FEATURE [App::DocumentObjectGroupPython] Cl_element028  label="Cl_element : 014"  # scripted group (container) (typed FeaturePython)
  n = 3
  ref = Cl_element
FEATURE [App::DocumentObjectGroupPython] G4_TRICHLOROETHYLENE  # scripted group (container) (typed FeaturePython)
  Dunit = g/cm3
  Dvalue = 1.46
  Group = -> [C_element115,H_element105,Cl_element028]
  conduct = 2
  density = 1
  expand = 3
  formula = G4_TRICHLOROETHYLENE
  name = G4_TRICHLOROETHYLENE
  specific = 4
FEATURE [App::DocumentObjectGroupPython] C_element116  label="C_element : 063"  # scripted group (container) (typed FeaturePython)
  n = 6
  ref = C_element
FEATURE [App::DocumentObjectGroupPython] H_element106  label="H_element : 15"  # scripted group (container) (typed FeaturePython)
  n = 15
  ref = H_element
FEATURE [App::DocumentObjectGroupPython] O_element099  label="O_element : 053"  # scripted group (container) (typed FeaturePython)
  n = 4
  ref = O_element
FEATURE [App::DocumentObjectGroupPython] P_element012  label="P_element : 1"  # scripted group (container) (typed FeaturePython)
  n = 1
  ref = P_element
FEATURE [App::DocumentObjectGroupPython] G4_TRIETHYL_PHOSPHATE  # scripted group (container) (typed FeaturePython)
  Dunit = g/cm3
  Dvalue = 1.07
  Group = -> [C_element116,H_element106,O_element099,P_element012]
  conduct = 2
  density = 1
  expand = 3
  formula = G4_TRIETHYL_PHOSPHATE
  name = G4_TRIETHYL_PHOSPHATE
  specific = 4
FEATURE [App::DocumentObjectGroupPython] W_element003  label="W_element : 003"  # scripted group (container) (typed FeaturePython)
  n = 1
  ref = W_element
FEATURE [App::DocumentObjectGroupPython] F_element017  label="F_element : 6"  # scripted group (container) (typed FeaturePython)
  n = 6
  ref = F_element
FEATURE [App::DocumentObjectGroupPython] G4_TUNGSTEN_HEXAFLUORIDE  # scripted group (container) (typed FeaturePython)
  Dunit = g/cm3
  Dvalue = 2.4
  Group = -> [W_element003,F_element017]
  conduct = 2
  density = 1
  expand = 3
  formula = G4_TUNGSTEN_HEXAFLUORIDE
  name = G4_TUNGSTEN_HEXAFLUORIDE
  specific = 4
FEATURE [App::DocumentObjectGroupPython] U_element001  label="U_element : 1"  # scripted group (container) (typed FeaturePython)
  n = 1
  ref = U_element
FEATURE [App::DocumentObjectGroupPython] C_element117  label="C_element : 064"  # scripted group (container) (typed FeaturePython)
  n = 2
  ref = C_element
FEATURE [App::DocumentObjectGroupPython] G4_URANIUM_DICARBIDE  # scripted group (container) (typed FeaturePython)
  Dunit = g/cm3
  Dvalue = 11.28
  Group = -> [U_element001,C_element117]
  conduct = 2
  density = 1
  expand = 3
  formula = G4_URANIUM_DICARBIDE
  name = G4_URANIUM_DICARBIDE
  specific = 4
FEATURE [App::DocumentObjectGroupPython] U_element002  label="U_element : 002"  # scripted group (container) (typed FeaturePython)
  n = 1
  ref = U_element
FEATURE [App::DocumentObjectGroupPython] C_element118  label="C_element : 065"  # scripted group (container) (typed FeaturePython)
  n = 1
  ref = C_element
FEATURE [App::DocumentObjectGroupPython] G4_URANIUM_MONOCARBIDE  # scripted group (container) (typed FeaturePython)
  Dunit = g/cm3
  Dvalue = 13.63
  Group = -> [U_element002,C_element118]
  conduct = 2
  density = 1
  expand = 3
  formula = G4_URANIUM_MONOCARBIDE
  name = G4_URANIUM_MONOCARBIDE
  specific = 4
FEATURE [App::DocumentObjectGroupPython] U_element003  label="U_element : 003"  # scripted group (container) (typed FeaturePython)
  n = 1
  ref = U_element
FEATURE [App::DocumentObjectGroupPython] O_element100  label="O_element : 054"  # scripted group (container) (typed FeaturePython)
  n = 2
  ref = O_element
FEATURE [App::DocumentObjectGroupPython] G4_URANIUM_OXIDE  # scripted group (container) (typed FeaturePython)
  Dunit = g/cm3
  Dvalue = 10.96
  Group = -> [U_element003,O_element100]
  conduct = 2
  density = 1
  expand = 3
  formula = G4_URANIUM_OXIDE
  name = G4_URANIUM_OXIDE
  specific = 4
FEATURE [App::DocumentObjectGroupPython] C_element119  label="C_element : 066"  # scripted group (container) (typed FeaturePython)
  n = 1
  ref = C_element
FEATURE [App::DocumentObjectGroupPython] H_element107  label="H_element : 057"  # scripted group (container) (typed FeaturePython)
  n = 4
  ref = H_element
FEATURE [App::DocumentObjectGroupPython] N_element046  label="N_element : 019"  # scripted group (container) (typed FeaturePython)
  n = 2
  ref = N_element
FEATURE [App::DocumentObjectGroupPython] O_element101  label="O_element : 055"  # scripted group (container) (typed FeaturePython)
  n = 1
  ref = O_element
FEATURE [App::DocumentObjectGroupPython] G4_UREA  # scripted group (container) (typed FeaturePython)
  Dunit = g/cm3
  Dvalue = 1.323
  Group = -> [C_element119,H_element107,N_element046,O_element101]
  conduct = 2
  density = 1
  expand = 3
  formula = G4_UREA
  name = G4_UREA
  specific = 4
FEATURE [App::DocumentObjectGroupPython] C_element120  label="C_element : 067"  # scripted group (container) (typed FeaturePython)
  n = 5
  ref = C_element
FEATURE [App::DocumentObjectGroupPython] H_element108  label="H_element : 058"  # scripted group (container) (typed FeaturePython)
  n = 11
  ref = H_element
FEATURE [App::DocumentObjectGroupPython] N_element047  label="N_element : 020"  # scripted group (container) (typed FeaturePython)
  n = 1
  ref = N_element
FEATURE [App::DocumentObjectGroupPython] O_element102  label="O_element : 056"  # scripted group (container) (typed FeaturePython)
  n = 2
  ref = O_element
FEATURE [App::DocumentObjectGroupPython] G4_VALINE  # scripted group (container) (typed FeaturePython)
  Dunit = g/cm3
  Dvalue = 1.23
  Group = -> [C_element120,H_element108,N_element047,O_element102]
  conduct = 2
  density = 1
  expand = 3
  formula = G4_VALINE
  name = G4_VALINE
  specific = 4
FEATURE [App::DocumentObjectGroupPython] H_element109  label="H_element : 0.009"  # scripted group (container) (typed FeaturePython)
  n = 0.009417
FEATURE [App::DocumentObjectGroupPython] C_element121  label="C_element : 0.281"  # scripted group (container) (typed FeaturePython)
  n = 0.280555
FEATURE [App::DocumentObjectGroupPython] F_element018  label="F_element : 0.710"  # scripted group (container) (typed FeaturePython)
  n = 0.710028
FEATURE [App::DocumentObjectGroupPython] G4_VITON  # scripted group (container) (typed FeaturePython)
  Dunit = g/cm3
  Dvalue = 1.8
  Group = -> [H_element109,C_element121,F_element018]
  conduct = 2
  density = 1
  expand = 3
  formula = G4_VITON
  name = G4_VITON
  specific = 4
FEATURE [App::DocumentObjectGroupPython] H_element110  label="H_element : 059"  # scripted group (container) (typed FeaturePython)
  n = 2
  ref = H_element
FEATURE [App::DocumentObjectGroupPython] O_element103  label="O_element : 057"  # scripted group (container) (typed FeaturePython)
  n = 1
  ref = O_element
FEATURE [App::DocumentObjectGroupPython] G4_WATER  # scripted group (container) (typed FeaturePython)
  Dunit = g/cm3
  Dvalue = 1
  Group = -> [H_element110,O_element103]
  conduct = 2
  density = 1
  expand = 3
  formula = G4_WATER
  name = G4_WATER
  specific = 4
FEATURE [App::DocumentObjectGroupPython] H_element111  label="H_element : 060"  # scripted group (container) (typed FeaturePython)
  n = 2
  ref = H_element
FEATURE [App::DocumentObjectGroupPython] O_element104  label="O_element : 058"  # scripted group (container) (typed FeaturePython)
  n = 1
  ref = O_element
FEATURE [App::DocumentObjectGroupPython] G4_WATER_VAPOR  # scripted group (container) (typed FeaturePython)
  Dunit = g/cm3
  Dvalue = 0.000756182
  Group = -> [H_element111,O_element104]
  conduct = 2
  density = 1
  expand = 3
  formula = G4_WATER_VAPOR
  name = G4_WATER_VAPOR
  specific = 4
FEATURE [App::DocumentObjectGroupPython] C_element122  label="C_element : 068"  # scripted group (container) (typed FeaturePython)
  n = 8
  ref = C_element
FEATURE [App::DocumentObjectGroupPython] H_element112  label="H_element : 061"  # scripted group (container) (typed FeaturePython)
  n = 10
  ref = H_element
FEATURE [App::DocumentObjectGroupPython] G4_XYLENE  # scripted group (container) (typed FeaturePython)
  Dunit = g/cm3
  Dvalue = 0.87
  Group = -> [C_element122,H_element112]
  conduct = 2
  density = 1
  expand = 3
  formula = G4_XYLENE
  name = G4_XYLENE
  specific = 4
FEATURE [App::DocumentObjectGroupPython] C_element123  label="C_element : 069"  # scripted group (container) (typed FeaturePython)
  n = 1
  ref = C_element
FEATURE [App::DocumentObjectGroupPython] G4_GRAPHITE  # scripted group (container) (typed FeaturePython)
  Dunit = g/cm3
  Dvalue = 2.21
  Group = -> [C_element123]
  conduct = 2
  density = 1
  expand = 3
  formula = G4_GRAPHITE
  name = G4_GRAPHITE
  specific = 4
FEATURE [App::DocumentObjectGroupPython] NIST  # scripted group (container) (typed FeaturePython)
  Group = -> [G4_A_150_TISSUE,G4_ACETONE,G4_ACETYLENE,G4_ADENINE,G4_ADIPOSE_TISSUE_ICRP,G4_AIR,G4_ALANINE,G4_ALUMINUM_OXIDE,G4_AMBER,G4_AMMONIA,G4_ANILINE,G4_ANTHRACENE,G4_B_100_BONE,G4_BAKELITE,G4_BARIUM_FLUORIDE,G4_BARIUM_SULFATE,G4_BENZENE,G4_BERYLLIUM_OXIDE,G4_BGO,G4_BLOOD_ICRP,G4_BONE_COMPACT_ICRU,G4_BONE_CORTICAL_ICRP,G4_BORON_CARBIDE,G4_BORON_OXIDE,G4_BRAIN_ICRP,G4_BUTANE,G4_N_BUTYL_ALCOHOL,G4_C_552,+152 more]
FEATURE [App::DocumentObjectGroupPython] H_element113  label="H_element : 062"  # scripted group (container) (typed FeaturePython)
  n = 1
  ref = H_element
FEATURE [App::DocumentObjectGroupPython] G4_H  # scripted group (container) (typed FeaturePython)
  Dunit = g/cm3
  Dvalue = 8.3748e-05
  Group = -> [H_element113]
  conduct = 2
  density = 1
  expand = 3
  formula = H
  name = G4_H
  specific = 4
FEATURE [App::DocumentObjectGroupPython] He_element001  label="He_element : 1"  # scripted group (container) (typed FeaturePython)
  n = 1
  ref = He_element
FEATURE [App::DocumentObjectGroupPython] G4_He  # scripted group (container) (typed FeaturePython)
  Dunit = g/cm3
  Dvalue = 0.000166322
  Group = -> [He_element001]
  conduct = 2
  density = 1
  expand = 3
  formula = He
  name = G4_He
  specific = 4
FEATURE [App::DocumentObjectGroupPython] Li_element008  label="Li_element : 008"  # scripted group (container) (typed FeaturePython)
  n = 1
  ref = Li_element
FEATURE [App::DocumentObjectGroupPython] G4_Li  # scripted group (container) (typed FeaturePython)
  Dunit = g/cm3
  Dvalue = 0.534
  Group = -> [Li_element008]
  conduct = 2
  density = 1
  expand = 3
  formula = Li
  name = G4_Li
  specific = 4
FEATURE [App::DocumentObjectGroupPython] Be_element002  label="Be_element : 002"  # scripted group (container) (typed FeaturePython)
  n = 1
  ref = Be_element
FEATURE [App::DocumentObjectGroupPython] G4_Be  # scripted group (container) (typed FeaturePython)
  Dunit = g/cm3
  Dvalue = 1.848
  Group = -> [Be_element002]
  conduct = 2
  density = 1
  expand = 3
  formula = Be
  name = G4_Be
  specific = 4
FEATURE [App::DocumentObjectGroupPython] B_element007  label="B_element : 007"  # scripted group (container) (typed FeaturePython)
  n = 1
  ref = B_element
FEATURE [App::DocumentObjectGroupPython] G4_B  # scripted group (container) (typed FeaturePython)
  Dunit = g/cm3
  Dvalue = 2.37
  Group = -> [B_element007]
  conduct = 2
  density = 1
  expand = 3
  formula = B
  name = G4_B
  specific = 4
FEATURE [App::DocumentObjectGroupPython] C_element124  label="C_element : 070"  # scripted group (container) (typed FeaturePython)
  n = 1
  ref = C_element
FEATURE [App::DocumentObjectGroupPython] G4_C  # scripted group (container) (typed FeaturePython)
  Dunit = g/cm3
  Dvalue = 2
  Group = -> [C_element124]
  conduct = 2
  density = 1
  expand = 3
  formula = C
  name = G4_C
  specific = 4
FEATURE [App::DocumentObjectGroupPython] N_element048  label="N_element : 021"  # scripted group (container) (typed FeaturePython)
  n = 1
  ref = N_element
FEATURE [App::DocumentObjectGroupPython] G4_N  # scripted group (container) (typed FeaturePython)
  Dunit = g/cm3
  Dvalue = 0.0011652
  Group = -> [N_element048]
  conduct = 2
  density = 1
  expand = 3
  formula = N
  name = G4_N
  specific = 4
FEATURE [App::DocumentObjectGroupPython] O_element105  label="O_element : 059"  # scripted group (container) (typed FeaturePython)
  n = 1
  ref = O_element
FEATURE [App::DocumentObjectGroupPython] G4_O  # scripted group (container) (typed FeaturePython)
  Dunit = g/cm3
  Dvalue = 0.00133151
  Group = -> [O_element105]
  conduct = 2
  density = 1
  expand = 3
  formula = O
  name = G4_O
  specific = 4
FEATURE [App::DocumentObjectGroupPython] F_element019  label="F_element : 008"  # scripted group (container) (typed FeaturePython)
  n = 1
  ref = F_element
FEATURE [App::DocumentObjectGroupPython] G4_F  # scripted group (container) (typed FeaturePython)
  Dunit = g/cm3
  Dvalue = 0.00158029
  Group = -> [F_element019]
  conduct = 2
  density = 1
  expand = 3
  formula = F
  name = G4_F
  specific = 4
FEATURE [App::DocumentObjectGroupPython] Ne_element001  label="Ne_element : 1"  # scripted group (container) (typed FeaturePython)
  n = 1
  ref = Ne_element
FEATURE [App::DocumentObjectGroupPython] G4_Ne  # scripted group (container) (typed FeaturePython)
  Dunit = g/cm3
  Dvalue = 0.000838505
  Group = -> [Ne_element001]
  conduct = 2
  density = 1
  expand = 3
  formula = Ne
  name = G4_Ne
  specific = 4
FEATURE [App::DocumentObjectGroupPython] Na_element020  label="Na_element : 005"  # scripted group (container) (typed FeaturePython)
  n = 1
  ref = Na_element
FEATURE [App::DocumentObjectGroupPython] G4_Na  # scripted group (container) (typed FeaturePython)
  Dunit = g/cm3
  Dvalue = 0.971
  Group = -> [Na_element020]
  conduct = 2
  density = 1
  expand = 3
  formula = Na
  name = G4_Na
  specific = 4
FEATURE [App::DocumentObjectGroupPython] Mg_element011  label="Mg_element : 005"  # scripted group (container) (typed FeaturePython)
  n = 1
  ref = Mg_element
FEATURE [App::DocumentObjectGroupPython] G4_Mg  # scripted group (container) (typed FeaturePython)
  Dunit = g/cm3
  Dvalue = 1.74
  Group = -> [Mg_element011]
  conduct = 2
  density = 1
  expand = 3
  formula = Mg
  name = G4_Mg
  specific = 4
FEATURE [App::DocumentObjectGroupPython] Al_element004  label="Al_element : 1"  # scripted group (container) (typed FeaturePython)
  n = 1
  ref = Al_element
FEATURE [App::DocumentObjectGroupPython] G4_Al  # scripted group (container) (typed FeaturePython)
  Dunit = g/cm3
  Dvalue = 2.699
  Group = -> [Al_element004]
  conduct = 2
  density = 1
  expand = 3
  formula = Al
  name = G4_Al
  specific = 4
FEATURE [App::DocumentObjectGroupPython] Si_element007  label="Si_element : 002"  # scripted group (container) (typed FeaturePython)
  n = 1
  ref = Si_element
FEATURE [App::DocumentObjectGroupPython] G4_Si  # scripted group (container) (typed FeaturePython)
  Dunit = g/cm3
  Dvalue = 2.33
  Group = -> [Si_element007]
  conduct = 2
  density = 1
  expand = 3
  formula = Si
  name = G4_Si
  specific = 4
FEATURE [App::DocumentObjectGroupPython] P_element013  label="P_element : 002"  # scripted group (container) (typed FeaturePython)
  n = 1
  ref = P_element
FEATURE [App::DocumentObjectGroupPython] G4_P  # scripted group (container) (typed FeaturePython)
  Dunit = g/cm3
  Dvalue = 2.2
  Group = -> [P_element013]
  conduct = 2
  density = 1
  expand = 3
  formula = P
  name = G4_P
  specific = 4
FEATURE [App::DocumentObjectGroupPython] S_element023  label="S_element : 007"  # scripted group (container) (typed FeaturePython)
  n = 1
  ref = S_element
FEATURE [App::DocumentObjectGroupPython] G4_S  # scripted group (container) (typed FeaturePython)
  Dunit = g/cm3
  Dvalue = 2
  Group = -> [S_element023]
  conduct = 2
  density = 1
  expand = 3
  formula = S
  name = G4_S
  specific = 4
FEATURE [App::DocumentObjectGroupPython] Cl_element029  label="Cl_element : 015"  # scripted group (container) (typed FeaturePython)
  n = 1
  ref = Cl_element
FEATURE [App::DocumentObjectGroupPython] G4_Cl  # scripted group (container) (typed FeaturePython)
  Dunit = g/cm3
  Dvalue = 0.00299473
  Group = -> [Cl_element029]
  conduct = 2
  density = 1
  expand = 3
  formula = Cl
  name = G4_Cl
  specific = 4
FEATURE [App::DocumentObjectGroupPython] Ar_element002  label="Ar_element : 1"  # scripted group (container) (typed FeaturePython)
  n = 1
  ref = Ar_element
FEATURE [App::DocumentObjectGroupPython] G4_Ar  # scripted group (container) (typed FeaturePython)
  Dunit = g/cm3
  Dvalue = 0.00166201
  Group = -> [Ar_element002]
  conduct = 2
  density = 1
  expand = 3
  formula = Ar
  name = G4_Ar
  specific = 4
FEATURE [App::DocumentObjectGroupPython] K_element013  label="K_element : 003"  # scripted group (container) (typed FeaturePython)
  n = 1
  ref = K_element
FEATURE [App::DocumentObjectGroupPython] G4_K  # scripted group (container) (typed FeaturePython)
  Dunit = g/cm3
  Dvalue = 0.862
  Group = -> [K_element013]
  conduct = 2
  density = 1
  expand = 3
  formula = K
  name = G4_K
  specific = 4
FEATURE [App::DocumentObjectGroupPython] Ca_element014  label="Ca_element : 007"  # scripted group (container) (typed FeaturePython)
  n = 1
  ref = Ca_element
FEATURE [App::DocumentObjectGroupPython] G4_Ca  # scripted group (container) (typed FeaturePython)
  Dunit = g/cm3
  Dvalue = 1.55
  Group = -> [Ca_element014]
  conduct = 2
  density = 1
  expand = 3
  formula = Ca
  name = G4_Ca
  specific = 4
FEATURE [App::DocumentObjectGroupPython] Sc_element001  label="Sc_element : 1"  # scripted group (container) (typed FeaturePython)
  n = 1
  ref = Sc_element
FEATURE [App::DocumentObjectGroupPython] G4_Sc  # scripted group (container) (typed FeaturePython)
  Dunit = g/cm3
  Dvalue = 2.989
  Group = -> [Sc_element001]
  conduct = 2
  density = 1
  expand = 3
  formula = Sc
  name = G4_Sc
  specific = 4
FEATURE [App::DocumentObjectGroupPython] Ti_element004  label="Ti_element : 002"  # scripted group (container) (typed FeaturePython)
  n = 1
  ref = Ti_element
FEATURE [App::DocumentObjectGroupPython] G4_Ti  # scripted group (container) (typed FeaturePython)
  Dunit = g/cm3
  Dvalue = 4.54
  Group = -> [Ti_element004]
  conduct = 2
  density = 1
  expand = 3
  formula = Ti
  name = G4_Ti
  specific = 4
FEATURE [App::DocumentObjectGroupPython] V_element001  label="V_element : 1"  # scripted group (container) (typed FeaturePython)
  n = 1
  ref = V_element
FEATURE [App::DocumentObjectGroupPython] G4_V  # scripted group (container) (typed FeaturePython)
  Dunit = g/cm3
  Dvalue = 6.11
  Group = -> [V_element001]
  conduct = 2
  density = 1
  expand = 3
  formula = V
  name = G4_V
  specific = 4
FEATURE [App::DocumentObjectGroupPython] Cr_element001  label="Cr_element : 1"  # scripted group (container) (typed FeaturePython)
  n = 1
  ref = Cr_element
FEATURE [App::DocumentObjectGroupPython] G4_Cr  # scripted group (container) (typed FeaturePython)
  Dunit = g/cm3
  Dvalue = 7.18
  Group = -> [Cr_element001]
  conduct = 2
  density = 1
  expand = 3
  formula = Cr
  name = G4_Cr
  specific = 4
FEATURE [App::DocumentObjectGroupPython] Mn_element001  label="Mn_element : 1"  # scripted group (container) (typed FeaturePython)
  n = 1
  ref = Mn_element
FEATURE [App::DocumentObjectGroupPython] G4_Mn  # scripted group (container) (typed FeaturePython)
  Dunit = g/cm3
  Dvalue = 7.44
  Group = -> [Mn_element001]
  conduct = 2
  density = 1
  expand = 3
  formula = Mn
  name = G4_Mn
  specific = 4
FEATURE [App::DocumentObjectGroupPython] Fe_element007  label="Fe_element : 004"  # scripted group (container) (typed FeaturePython)
  n = 1
  ref = Fe_element
FEATURE [App::DocumentObjectGroupPython] G4_Fe  # scripted group (container) (typed FeaturePython)
  Dunit = g/cm3
  Dvalue = 7.874
  Group = -> [Fe_element007]
  conduct = 2
  density = 1
  expand = 3
  formula = Fe
  name = G4_Fe
  specific = 4
FEATURE [App::DocumentObjectGroupPython] Co_element001  label="Co_element : 1"  # scripted group (container) (typed FeaturePython)
  n = 1
  ref = Co_element
FEATURE [App::DocumentObjectGroupPython] G4_Co  # scripted group (container) (typed FeaturePython)
  Dunit = g/cm3
  Dvalue = 8.9
  Group = -> [Co_element001]
  conduct = 2
  density = 1
  expand = 3
  formula = Co
  name = G4_Co
  specific = 4
FEATURE [App::DocumentObjectGroupPython] Ni_element001  label="Ni_element : 1"  # scripted group (container) (typed FeaturePython)
  n = 1
  ref = Ni_element
FEATURE [App::DocumentObjectGroupPython] G4_Ni  # scripted group (container) (typed FeaturePython)
  Dunit = g/cm3
  Dvalue = 8.902
  Group = -> [Ni_element001]
  conduct = 2
  density = 1
  expand = 3
  formula = Ni
  name = G4_Ni
  specific = 4
FEATURE [App::DocumentObjectGroupPython] Cu_element001  label="Cu_element : 1"  # scripted group (container) (typed FeaturePython)
  n = 1
  ref = Cu_element
FEATURE [App::DocumentObjectGroupPython] G4_Cu  # scripted group (container) (typed FeaturePython)
  Dunit = g/cm3
  Dvalue = 8.96
  Group = -> [Cu_element001]
  conduct = 2
  density = 1
  expand = 3
  formula = Cu
  name = G4_Cu
  specific = 4
FEATURE [App::DocumentObjectGroupPython] Zn_element001  label="Zn_element : 1"  # scripted group (container) (typed FeaturePython)
  n = 1
  ref = Zn_element
FEATURE [App::DocumentObjectGroupPython] G4_Zn  # scripted group (container) (typed FeaturePython)
  Dunit = g/cm3
  Dvalue = 7.133
  Group = -> [Zn_element001]
  conduct = 2
  density = 1
  expand = 3
  formula = Zn
  name = G4_Zn
  specific = 4
FEATURE [App::DocumentObjectGroupPython] Ga_element002  label="Ga_element : 002"  # scripted group (container) (typed FeaturePython)
  n = 1
  ref = Ga_element
FEATURE [App::DocumentObjectGroupPython] G4_Ga  # scripted group (container) (typed FeaturePython)
  Dunit = g/cm3
  Dvalue = 5.904
  Group = -> [Ga_element002]
  conduct = 2
  density = 1
  expand = 3
  formula = Ga
  name = G4_Ga
  specific = 4
FEATURE [App::DocumentObjectGroupPython] Ge_element002  label="Ge_element : 1"  # scripted group (container) (typed FeaturePython)
  n = 1
  ref = Ge_element
FEATURE [App::DocumentObjectGroupPython] G4_Ge  # scripted group (container) (typed FeaturePython)
  Dunit = g/cm3
  Dvalue = 5.323
  Group = -> [Ge_element002]
  conduct = 2
  density = 1
  expand = 3
  formula = Ge
  name = G4_Ge
  specific = 4
FEATURE [App::DocumentObjectGroupPython] As_element003  label="As_element : 002"  # scripted group (container) (typed FeaturePython)
  n = 1
  ref = As_element
FEATURE [App::DocumentObjectGroupPython] G4_As  # scripted group (container) (typed FeaturePython)
  Dunit = g/cm3
  Dvalue = 5.73
  Group = -> [As_element003]
  conduct = 2
  density = 1
  expand = 3
  formula = As
  name = G4_As
  specific = 4
FEATURE [App::DocumentObjectGroupPython] Se_element001  label="Se_element : 1"  # scripted group (container) (typed FeaturePython)
  n = 1
  ref = Se_element
FEATURE [App::DocumentObjectGroupPython] G4_Se  # scripted group (container) (typed FeaturePython)
  Dunit = g/cm3
  Dvalue = 4.5
  Group = -> [Se_element001]
  conduct = 2
  density = 1
  expand = 3
  formula = Se
  name = G4_Se
  specific = 4
FEATURE [App::DocumentObjectGroupPython] Br_element007  label="Br_element : 004"  # scripted group (container) (typed FeaturePython)
  n = 1
  ref = Br_element
FEATURE [App::DocumentObjectGroupPython] G4_Br  # scripted group (container) (typed FeaturePython)
  Dunit = g/cm3
  Dvalue = 0.0070721
  Group = -> [Br_element007]
  conduct = 2
  density = 1
  expand = 3
  formula = Br
  name = G4_Br
  specific = 4
FEATURE [App::DocumentObjectGroupPython] Kr_element001  label="Kr_element : 1"  # scripted group (container) (typed FeaturePython)
  n = 1
  ref = Kr_element
FEATURE [App::DocumentObjectGroupPython] G4_Kr  # scripted group (container) (typed FeaturePython)
  Dunit = g/cm3
  Dvalue = 0.00347832
  Group = -> [Kr_element001]
  conduct = 2
  density = 1
  expand = 3
  formula = Kr
  name = G4_Kr
  specific = 4
FEATURE [App::DocumentObjectGroupPython] Rb_element001  label="Rb_element : 1"  # scripted group (container) (typed FeaturePython)
  n = 1
  ref = Rb_element
FEATURE [App::DocumentObjectGroupPython] G4_Rb  # scripted group (container) (typed FeaturePython)
  Dunit = g/cm3
  Dvalue = 1.532
  Group = -> [Rb_element001]
  conduct = 2
  density = 1
  expand = 3
  formula = Rb
  name = G4_Rb
  specific = 4
FEATURE [App::DocumentObjectGroupPython] Sr_element001  label="Sr_element : 1"  # scripted group (container) (typed FeaturePython)
  n = 1
  ref = Sr_element
FEATURE [App::DocumentObjectGroupPython] G4_Sr  # scripted group (container) (typed FeaturePython)
  Dunit = g/cm3
  Dvalue = 2.54
  Group = -> [Sr_element001]
  conduct = 2
  density = 1
  expand = 3
  formula = Sr
  name = G4_Sr
  specific = 4
FEATURE [App::DocumentObjectGroupPython] Y_element001  label="Y_element : 1"  # scripted group (container) (typed FeaturePython)
  n = 1
  ref = Y_element
FEATURE [App::DocumentObjectGroupPython] G4_Y  # scripted group (container) (typed FeaturePython)
  Dunit = g/cm3
  Dvalue = 4.469
  Group = -> [Y_element001]
  conduct = 2
  density = 1
  expand = 3
  formula = Y
  name = G4_Y
  specific = 4
FEATURE [App::DocumentObjectGroupPython] Zr_element001  label="Zr_element : 1"  # scripted group (container) (typed FeaturePython)
  n = 1
  ref = Zr_element
FEATURE [App::DocumentObjectGroupPython] G4_Zr  # scripted group (container) (typed FeaturePython)
  Dunit = g/cm3
  Dvalue = 6.506
  Group = -> [Zr_element001]
  conduct = 2
  density = 1
  expand = 3
  formula = Zr
  name = G4_Zr
  specific = 4
FEATURE [App::DocumentObjectGroupPython] Nb_element001  label="Nb_element : 1"  # scripted group (container) (typed FeaturePython)
  n = 1
  ref = Nb_element
FEATURE [App::DocumentObjectGroupPython] G4_Nb  # scripted group (container) (typed FeaturePython)
  Dunit = g/cm3
  Dvalue = 8.57
  Group = -> [Nb_element001]
  conduct = 2
  density = 1
  expand = 3
  formula = Nb
  name = G4_Nb
  specific = 4
FEATURE [App::DocumentObjectGroupPython] Mo_element001  label="Mo_element : 1"  # scripted group (container) (typed FeaturePython)
  n = 1
  ref = Mo_element
FEATURE [App::DocumentObjectGroupPython] G4_Mo  # scripted group (container) (typed FeaturePython)
  Dunit = g/cm3
  Dvalue = 10.22
  Group = -> [Mo_element001]
  conduct = 2
  density = 1
  expand = 3
  formula = Mo
  name = G4_Mo
  specific = 4
FEATURE [App::DocumentObjectGroupPython] Tc_element001  label="Tc_element : 1"  # scripted group (container) (typed FeaturePython)
  n = 1
  ref = Tc_element
FEATURE [App::DocumentObjectGroupPython] G4_Tc  # scripted group (container) (typed FeaturePython)
  Dunit = g/cm3
  Dvalue = 11.5
  Group = -> [Tc_element001]
  conduct = 2
  density = 1
  expand = 3
  formula = Tc
  name = G4_Tc
  specific = 4
FEATURE [App::DocumentObjectGroupPython] Ru_element001  label="Ru_element : 1"  # scripted group (container) (typed FeaturePython)
  n = 1
  ref = Ru_element
FEATURE [App::DocumentObjectGroupPython] G4_Ru  # scripted group (container) (typed FeaturePython)
  Dunit = g/cm3
  Dvalue = 12.41
  Group = -> [Ru_element001]
  conduct = 2
  density = 1
  expand = 3
  formula = Ru
  name = G4_Ru
  specific = 4
FEATURE [App::DocumentObjectGroupPython] Rh_element001  label="Rh_element : 1"  # scripted group (container) (typed FeaturePython)
  n = 1
  ref = Rh_element
FEATURE [App::DocumentObjectGroupPython] G4_Rh  # scripted group (container) (typed FeaturePython)
  Dunit = g/cm3
  Dvalue = 12.41
  Group = -> [Rh_element001]
  conduct = 2
  density = 1
  expand = 3
  formula = Rh
  name = G4_Rh
  specific = 4
FEATURE [App::DocumentObjectGroupPython] Pd_element001  label="Pd_element : 1"  # scripted group (container) (typed FeaturePython)
  n = 1
  ref = Pd_element
FEATURE [App::DocumentObjectGroupPython] G4_Pd  # scripted group (container) (typed FeaturePython)
  Dunit = g/cm3
  Dvalue = 12.02
  Group = -> [Pd_element001]
  conduct = 2
  density = 1
  expand = 3
  formula = Pd
  name = G4_Pd
  specific = 4
FEATURE [App::DocumentObjectGroupPython] Ag_element006  label="Ag_element : 004"  # scripted group (container) (typed FeaturePython)
  n = 1
  ref = Ag_element
FEATURE [App::DocumentObjectGroupPython] G4_Ag  # scripted group (container) (typed FeaturePython)
  Dunit = g/cm3
  Dvalue = 10.5
  Group = -> [Ag_element006]
  conduct = 2
  density = 1
  expand = 3
  formula = Ag
  name = G4_Ag
  specific = 4
FEATURE [App::DocumentObjectGroupPython] Cd_element003  label="Cd_element : 003"  # scripted group (container) (typed FeaturePython)
  n = 1
  ref = Cd_element
FEATURE [App::DocumentObjectGroupPython] G4_Cd  # scripted group (container) (typed FeaturePython)
  Dunit = g/cm3
  Dvalue = 8.65
  Group = -> [Cd_element003]
  conduct = 2
  density = 1
  expand = 3
  formula = Cd
  name = G4_Cd
  specific = 4
FEATURE [App::DocumentObjectGroupPython] In_element001  label="In_element : 1"  # scripted group (container) (typed FeaturePython)
  n = 1
  ref = In_element
FEATURE [App::DocumentObjectGroupPython] G4_In  # scripted group (container) (typed FeaturePython)
  Dunit = g/cm3
  Dvalue = 7.31
  Group = -> [In_element001]
  conduct = 2
  density = 1
  expand = 3
  formula = In
  name = G4_In
  specific = 4
FEATURE [App::DocumentObjectGroupPython] Sn_element001  label="Sn_element : 1"  # scripted group (container) (typed FeaturePython)
  n = 1
  ref = Sn_element
FEATURE [App::DocumentObjectGroupPython] G4_Sn  # scripted group (container) (typed FeaturePython)
  Dunit = g/cm3
  Dvalue = 7.31
  Group = -> [Sn_element001]
  conduct = 2
  density = 1
  expand = 3
  formula = Sn
  name = G4_Sn
  specific = 4
FEATURE [App::DocumentObjectGroupPython] Sb_element001  label="Sb_element : 1"  # scripted group (container) (typed FeaturePython)
  n = 1
  ref = Sb_element
FEATURE [App::DocumentObjectGroupPython] G4_Sb  # scripted group (container) (typed FeaturePython)
  Dunit = g/cm3
  Dvalue = 6.691
  Group = -> [Sb_element001]
  conduct = 2
  density = 1
  expand = 3
  formula = Sb
  name = G4_Sb
  specific = 4
FEATURE [App::DocumentObjectGroupPython] Te_element002  label="Te_element : 002"  # scripted group (container) (typed FeaturePython)
  n = 1
  ref = Te_element
FEATURE [App::DocumentObjectGroupPython] G4_Te  # scripted group (container) (typed FeaturePython)
  Dunit = g/cm3
  Dvalue = 6.24
  Group = -> [Te_element002]
  conduct = 2
  density = 1
  expand = 3
  formula = Te
  name = G4_Te
  specific = 4
FEATURE [App::DocumentObjectGroupPython] I_element010  label="I_element : 006"  # scripted group (container) (typed FeaturePython)
  n = 1
  ref = I_element
FEATURE [App::DocumentObjectGroupPython] G4_I  # scripted group (container) (typed FeaturePython)
  Dunit = g/cm3
  Dvalue = 4.93
  Group = -> [I_element010]
  conduct = 2
  density = 1
  expand = 3
  formula = I
  name = G4_I
  specific = 4
FEATURE [App::DocumentObjectGroupPython] Xe_element001  label="Xe_element : 1"  # scripted group (container) (typed FeaturePython)
  n = 1
  ref = Xe_element
FEATURE [App::DocumentObjectGroupPython] G4_Xe  # scripted group (container) (typed FeaturePython)
  Dunit = g/cm3
  Dvalue = 0.00548536
  Group = -> [Xe_element001]
  conduct = 2
  density = 1
  expand = 3
  formula = Xe
  name = G4_Xe
  specific = 4
FEATURE [App::DocumentObjectGroupPython] Cs_element003  label="Cs_element : 003"  # scripted group (container) (typed FeaturePython)
  n = 1
  ref = Cs_element
FEATURE [App::DocumentObjectGroupPython] G4_Cs  # scripted group (container) (typed FeaturePython)
  Dunit = g/cm3
  Dvalue = 1.873
  Group = -> [Cs_element003]
  conduct = 2
  density = 1
  expand = 3
  formula = Cs
  name = G4_Cs
  specific = 4
FEATURE [App::DocumentObjectGroupPython] Ba_element003  label="Ba_element : 003"  # scripted group (container) (typed FeaturePython)
  n = 1
  ref = Ba_element
FEATURE [App::DocumentObjectGroupPython] G4_Ba  # scripted group (container) (typed FeaturePython)
  Dunit = g/cm3
  Dvalue = 3.5
  Group = -> [Ba_element003]
  conduct = 2
  density = 1
  expand = 3
  formula = Ba
  name = G4_Ba
  specific = 4
FEATURE [App::DocumentObjectGroupPython] La_element003  label="La_element : 003"  # scripted group (container) (typed FeaturePython)
  n = 1
  ref = La_element
FEATURE [App::DocumentObjectGroupPython] G4_La  # scripted group (container) (typed FeaturePython)
  Dunit = g/cm3
  Dvalue = 6.154
  Group = -> [La_element003]
  conduct = 2
  density = 1
  expand = 3
  formula = La
  name = G4_La
  specific = 4
FEATURE [App::DocumentObjectGroupPython] Ce_element002  label="Ce_element : 1"  # scripted group (container) (typed FeaturePython)
  n = 1
  ref = Ce_element
FEATURE [App::DocumentObjectGroupPython] G4_Ce  # scripted group (container) (typed FeaturePython)
  Dunit = g/cm3
  Dvalue = 6.657
  Group = -> [Ce_element002]
  conduct = 2
  density = 1
  expand = 3
  formula = Ce
  name = G4_Ce
  specific = 4
FEATURE [App::DocumentObjectGroupPython] Pr_element001  label="Pr_element : 1"  # scripted group (container) (typed FeaturePython)
  n = 1
  ref = Pr_element
FEATURE [App::DocumentObjectGroupPython] G4_Pr  # scripted group (container) (typed FeaturePython)
  Dunit = g/cm3
  Dvalue = 6.71
  Group = -> [Pr_element001]
  conduct = 2
  density = 1
  expand = 3
  formula = Pr
  name = G4_Pr
  specific = 4
FEATURE [App::DocumentObjectGroupPython] Nd_element001  label="Nd_element : 1"  # scripted group (container) (typed FeaturePython)
  n = 1
  ref = Nd_element
FEATURE [App::DocumentObjectGroupPython] G4_Nd  # scripted group (container) (typed FeaturePython)
  Dunit = g/cm3
  Dvalue = 6.9
  Group = -> [Nd_element001]
  conduct = 2
  density = 1
  expand = 3
  formula = Nd
  name = G4_Nd
  specific = 4
FEATURE [App::DocumentObjectGroupPython] Pm_element001  label="Pm_element : 1"  # scripted group (container) (typed FeaturePython)
  n = 1
  ref = Pm_element
FEATURE [App::DocumentObjectGroupPython] G4_Pm  # scripted group (container) (typed FeaturePython)
  Dunit = g/cm3
  Dvalue = 7.22
  Group = -> [Pm_element001]
  conduct = 2
  density = 1
  expand = 3
  formula = Pm
  name = G4_Pm
  specific = 4
FEATURE [App::DocumentObjectGroupPython] Sm_element001  label="Sm_element : 1"  # scripted group (container) (typed FeaturePython)
  n = 1
  ref = Sm_element
FEATURE [App::DocumentObjectGroupPython] G4_Sm  # scripted group (container) (typed FeaturePython)
  Dunit = g/cm3
  Dvalue = 7.46
  Group = -> [Sm_element001]
  conduct = 2
  density = 1
  expand = 3
  formula = Sm
  name = G4_Sm
  specific = 4
FEATURE [App::DocumentObjectGroupPython] Eu_element001  label="Eu_element : 1"  # scripted group (container) (typed FeaturePython)
  n = 1
  ref = Eu_element
FEATURE [App::DocumentObjectGroupPython] G4_Eu  # scripted group (container) (typed FeaturePython)
  Dunit = g/cm3
  Dvalue = 5.243
  Group = -> [Eu_element001]
  conduct = 2
  density = 1
  expand = 3
  formula = Eu
  name = G4_Eu
  specific = 4
FEATURE [App::DocumentObjectGroupPython] Gd_element002  label="Gd_element : 1"  # scripted group (container) (typed FeaturePython)
  n = 1
  ref = Gd_element
FEATURE [App::DocumentObjectGroupPython] G4_Gd  # scripted group (container) (typed FeaturePython)
  Dunit = g/cm3
  Dvalue = 7.9004
  Group = -> [Gd_element002]
  conduct = 2
  density = 1
  expand = 3
  formula = Gd
  name = G4_Gd
  specific = 4
FEATURE [App::DocumentObjectGroupPython] Tb_element001  label="Tb_element : 1"  # scripted group (container) (typed FeaturePython)
  n = 1
  ref = Tb_element
FEATURE [App::DocumentObjectGroupPython] G4_Tb  # scripted group (container) (typed FeaturePython)
  Dunit = g/cm3
  Dvalue = 8.229
  Group = -> [Tb_element001]
  conduct = 2
  density = 1
  expand = 3
  formula = Tb
  name = G4_Tb
  specific = 4
FEATURE [App::DocumentObjectGroupPython] Dy_element001  label="Dy_element : 1"  # scripted group (container) (typed FeaturePython)
  n = 1
  ref = Dy_element
FEATURE [App::DocumentObjectGroupPython] G4_Dy  # scripted group (container) (typed FeaturePython)
  Dunit = g/cm3
  Dvalue = 8.55
  Group = -> [Dy_element001]
  conduct = 2
  density = 1
  expand = 3
  formula = Dy
  name = G4_Dy
  specific = 4
FEATURE [App::DocumentObjectGroupPython] Ho_element001  label="Ho_element : 1"  # scripted group (container) (typed FeaturePython)
  n = 1
  ref = Ho_element
FEATURE [App::DocumentObjectGroupPython] G4_Ho  # scripted group (container) (typed FeaturePython)
  Dunit = g/cm3
  Dvalue = 8.795
  Group = -> [Ho_element001]
  conduct = 2
  density = 1
  expand = 3
  formula = Ho
  name = G4_Ho
  specific = 4
FEATURE [App::DocumentObjectGroupPython] Er_element001  label="Er_element : 1"  # scripted group (container) (typed FeaturePython)
  n = 1
  ref = Er_element
FEATURE [App::DocumentObjectGroupPython] G4_Er  # scripted group (container) (typed FeaturePython)
  Dunit = g/cm3
  Dvalue = 9.066
  Group = -> [Er_element001]
  conduct = 2
  density = 1
  expand = 3
  formula = Er
  name = G4_Er
  specific = 4
FEATURE [App::DocumentObjectGroupPython] Tm_element001  label="Tm_element : 1"  # scripted group (container) (typed FeaturePython)
  n = 1
  ref = Tm_element
FEATURE [App::DocumentObjectGroupPython] G4_Tm  # scripted group (container) (typed FeaturePython)
  Dunit = g/cm3
  Dvalue = 9.321
  Group = -> [Tm_element001]
  conduct = 2
  density = 1
  expand = 3
  formula = Tm
  name = G4_Tm
  specific = 4
FEATURE [App::DocumentObjectGroupPython] Yb_element001  label="Yb_element : 1"  # scripted group (container) (typed FeaturePython)
  n = 1
  ref = Yb_element
FEATURE [App::DocumentObjectGroupPython] G4_Yb  # scripted group (container) (typed FeaturePython)
  Dunit = g/cm3
  Dvalue = 6.73
  Group = -> [Yb_element001]
  conduct = 2
  density = 1
  expand = 3
  formula = Yb
  name = G4_Yb
  specific = 4
FEATURE [App::DocumentObjectGroupPython] Lu_element001  label="Lu_element : 1"  # scripted group (container) (typed FeaturePython)
  n = 1
  ref = Lu_element
FEATURE [App::DocumentObjectGroupPython] G4_Lu  # scripted group (container) (typed FeaturePython)
  Dunit = g/cm3
  Dvalue = 9.84
  Group = -> [Lu_element001]
  conduct = 2
  density = 1
  expand = 3
  formula = Lu
  name = G4_Lu
  specific = 4
FEATURE [App::DocumentObjectGroupPython] Hf_element001  label="Hf_element : 1"  # scripted group (container) (typed FeaturePython)
  n = 1
  ref = Hf_element
FEATURE [App::DocumentObjectGroupPython] G4_Hf  # scripted group (container) (typed FeaturePython)
  Dunit = g/cm3
  Dvalue = 13.31
  Group = -> [Hf_element001]
  conduct = 2
  density = 1
  expand = 3
  formula = Hf
  name = G4_Hf
  specific = 4
FEATURE [App::DocumentObjectGroupPython] Ta_element001  label="Ta_element : 1"  # scripted group (container) (typed FeaturePython)
  n = 1
  ref = Ta_element
FEATURE [App::DocumentObjectGroupPython] G4_Ta  # scripted group (container) (typed FeaturePython)
  Dunit = g/cm3
  Dvalue = 16.654
  Group = -> [Ta_element001]
  conduct = 2
  density = 1
  expand = 3
  formula = Ta
  name = G4_Ta
  specific = 4
FEATURE [App::DocumentObjectGroupPython] W_element004  label="W_element : 004"  # scripted group (container) (typed FeaturePython)
  n = 1
  ref = W_element
FEATURE [App::DocumentObjectGroupPython] G4_W  # scripted group (container) (typed FeaturePython)
  Dunit = g/cm3
  Dvalue = 19.3
  Group = -> [W_element004]
  conduct = 2
  density = 1
  expand = 3
  formula = W
  name = G4_W
  specific = 4
FEATURE [App::DocumentObjectGroupPython] Re_element001  label="Re_element : 1"  # scripted group (container) (typed FeaturePython)
  n = 1
  ref = Re_element
FEATURE [App::DocumentObjectGroupPython] G4_Re  # scripted group (container) (typed FeaturePython)
  Dunit = g/cm3
  Dvalue = 21.02
  Group = -> [Re_element001]
  conduct = 2
  density = 1
  expand = 3
  formula = Re
  name = G4_Re
  specific = 4
FEATURE [App::DocumentObjectGroupPython] Os_element001  label="Os_element : 1"  # scripted group (container) (typed FeaturePython)
  n = 1
  ref = Os_element
FEATURE [App::DocumentObjectGroupPython] G4_Os  # scripted group (container) (typed FeaturePython)
  Dunit = g/cm3
  Dvalue = 22.57
  Group = -> [Os_element001]
  conduct = 2
  density = 1
  expand = 3
  formula = Os
  name = G4_Os
  specific = 4
FEATURE [App::DocumentObjectGroupPython] Ir_element001  label="Ir_element : 1"  # scripted group (container) (typed FeaturePython)
  n = 1
  ref = Ir_element
FEATURE [App::DocumentObjectGroupPython] G4_Ir  # scripted group (container) (typed FeaturePython)
  Dunit = g/cm3
  Dvalue = 22.42
  Group = -> [Ir_element001]
  conduct = 2
  density = 1
  expand = 3
  formula = Ir
  name = G4_Ir
  specific = 4
FEATURE [App::DocumentObjectGroupPython] Pt_element001  label="Pt_element : 1"  # scripted group (container) (typed FeaturePython)
  n = 1
  ref = Pt_element
FEATURE [App::DocumentObjectGroupPython] G4_Pt  # scripted group (container) (typed FeaturePython)
  Dunit = g/cm3
  Dvalue = 21.45
  Group = -> [Pt_element001]
  conduct = 2
  density = 1
  expand = 3
  formula = Pt
  name = G4_Pt
  specific = 4
FEATURE [App::DocumentObjectGroupPython] Au_element001  label="Au_element : 1"  # scripted group (container) (typed FeaturePython)
  n = 1
  ref = Au_element
FEATURE [App::DocumentObjectGroupPython] G4_Au  # scripted group (container) (typed FeaturePython)
  Dunit = g/cm3
  Dvalue = 19.32
  Group = -> [Au_element001]
  conduct = 2
  density = 1
  expand = 3
  formula = Au
  name = G4_Au
  specific = 4
FEATURE [App::DocumentObjectGroupPython] Hg_element002  label="Hg_element : 002"  # scripted group (container) (typed FeaturePython)
  n = 1
  ref = Hg_element
FEATURE [App::DocumentObjectGroupPython] G4_Hg  # scripted group (container) (typed FeaturePython)
  Dunit = g/cm3
  Dvalue = 13.546
  Group = -> [Hg_element002]
  conduct = 2
  density = 1
  expand = 3
  formula = Hg
  name = G4_Hg
  specific = 4
FEATURE [App::DocumentObjectGroupPython] Tl_element002  label="Tl_element : 002"  # scripted group (container) (typed FeaturePython)
  n = 1
  ref = Tl_element
FEATURE [App::DocumentObjectGroupPython] G4_Tl  # scripted group (container) (typed FeaturePython)
  Dunit = g/cm3
  Dvalue = 11.72
  Group = -> [Tl_element002]
  conduct = 2
  density = 1
  expand = 3
  formula = Tl
  name = G4_Tl
  specific = 4
FEATURE [App::DocumentObjectGroupPython] Pb_element003  label="Pb_element : 1"  # scripted group (container) (typed FeaturePython)
  n = 1
  ref = Pb_element
FEATURE [App::DocumentObjectGroupPython] G4_Pb  # scripted group (container) (typed FeaturePython)
  Dunit = g/cm3
  Dvalue = 11.35
  Group = -> [Pb_element003]
  conduct = 2
  density = 1
  expand = 3
  formula = Pb
  name = G4_Pb
  specific = 4
FEATURE [App::DocumentObjectGroupPython] Bi_element002  label="Bi_element : 1"  # scripted group (container) (typed FeaturePython)
  n = 1
  ref = Bi_element
FEATURE [App::DocumentObjectGroupPython] G4_Bi  # scripted group (container) (typed FeaturePython)
  Dunit = g/cm3
  Dvalue = 9.747
  Group = -> [Bi_element002]
  conduct = 2
  density = 1
  expand = 3
  formula = Bi
  name = G4_Bi
  specific = 4
FEATURE [App::DocumentObjectGroupPython] Po_element001  label="Po_element : 1"  # scripted group (container) (typed FeaturePython)
  n = 1
  ref = Po_element
FEATURE [App::DocumentObjectGroupPython] G4_Po  # scripted group (container) (typed FeaturePython)
  Dunit = g/cm3
  Dvalue = 9.32
  Group = -> [Po_element001]
  conduct = 2
  density = 1
  expand = 3
  formula = Po
  name = G4_Po
  specific = 4
FEATURE [App::DocumentObjectGroupPython] At_element001  label="At_element : 1"  # scripted group (container) (typed FeaturePython)
  n = 1
  ref = At_element
FEATURE [App::DocumentObjectGroupPython] G4_At  # scripted group (container) (typed FeaturePython)
  Dunit = g/cm3
  Dvalue = 9.32
  Group = -> [At_element001]
  conduct = 2
  density = 1
  expand = 3
  formula = At
  name = G4_At
  specific = 4
FEATURE [App::DocumentObjectGroupPython] Rn_element001  label="Rn_element : 1"  # scripted group (container) (typed FeaturePython)
  n = 1
  ref = Rn_element
FEATURE [App::DocumentObjectGroupPython] G4_Rn  # scripted group (container) (typed FeaturePython)
  Dunit = g/cm3
  Dvalue = 0.00900662
  Group = -> [Rn_element001]
  conduct = 2
  density = 1
  expand = 3
  formula = Rn
  name = G4_Rn
  specific = 4
FEATURE [App::DocumentObjectGroupPython] Fr_element001  label="Fr_element : 1"  # scripted group (container) (typed FeaturePython)
  n = 1
  ref = Fr_element
FEATURE [App::DocumentObjectGroupPython] G4_Fr  # scripted group (container) (typed FeaturePython)
  Dunit = g/cm3
  Dvalue = 1
  Group = -> [Fr_element001]
  conduct = 2
  density = 1
  expand = 3
  formula = Fr
  name = G4_Fr
  specific = 4
FEATURE [App::DocumentObjectGroupPython] Ra_element001  label="Ra_element : 1"  # scripted group (container) (typed FeaturePython)
  n = 1
  ref = Ra_element
FEATURE [App::DocumentObjectGroupPython] G4_Ra  # scripted group (container) (typed FeaturePython)
  Dunit = g/cm3
  Dvalue = 5
  Group = -> [Ra_element001]
  conduct = 2
  density = 1
  expand = 3
  formula = Ra
  name = G4_Ra
  specific = 4
FEATURE [App::DocumentObjectGroupPython] Ac_element001  label="Ac_element : 1"  # scripted group (container) (typed FeaturePython)
  n = 1
  ref = Ac_element
FEATURE [App::DocumentObjectGroupPython] G4_Ac  # scripted group (container) (typed FeaturePython)
  Dunit = g/cm3
  Dvalue = 10.07
  Group = -> [Ac_element001]
  conduct = 2
  density = 1
  expand = 3
  formula = Ac
  name = G4_Ac
  specific = 4
FEATURE [App::DocumentObjectGroupPython] Th_element001  label="Th_element : 1"  # scripted group (container) (typed FeaturePython)
  n = 1
  ref = Th_element
FEATURE [App::DocumentObjectGroupPython] G4_Th  # scripted group (container) (typed FeaturePython)
  Dunit = g/cm3
  Dvalue = 11.72
  Group = -> [Th_element001]
  conduct = 2
  density = 1
  expand = 3
  formula = Th
  name = G4_Th
  specific = 4
FEATURE [App::DocumentObjectGroupPython] Pa_element001  label="Pa_element : 1"  # scripted group (container) (typed FeaturePython)
  n = 1
  ref = Pa_element
FEATURE [App::DocumentObjectGroupPython] G4_Pa  # scripted group (container) (typed FeaturePython)
  Dunit = g/cm3
  Dvalue = 15.37
  Group = -> [Pa_element001]
  conduct = 2
  density = 1
  expand = 3
  formula = Pa
  name = G4_Pa
  specific = 4
FEATURE [App::DocumentObjectGroupPython] U_element004  label="U_element : 004"  # scripted group (container) (typed FeaturePython)
  n = 1
  ref = U_element
FEATURE [App::DocumentObjectGroupPython] G4_U  # scripted group (container) (typed FeaturePython)
  Dunit = g/cm3
  Dvalue = 18.95
  Group = -> [U_element004]
  conduct = 2
  density = 1
  expand = 3
  formula = U
  name = G4_U
  specific = 4
FEATURE [App::DocumentObjectGroupPython] Np_element001  label="Np_element : 1"  # scripted group (container) (typed FeaturePython)
  n = 1
  ref = Np_element
FEATURE [App::DocumentObjectGroupPython] G4_Np  # scripted group (container) (typed FeaturePython)
  Dunit = g/cm3
  Dvalue = 20.25
  Group = -> [Np_element001]
  conduct = 2
  density = 1
  expand = 3
  formula = Np
  name = G4_Np
  specific = 4
FEATURE [App::DocumentObjectGroupPython] Pu_element002  label="Pu_element : 002"  # scripted group (container) (typed FeaturePython)
  n = 1
  ref = Pu_element
FEATURE [App::DocumentObjectGroupPython] G4_Pu  # scripted group (container) (typed FeaturePython)
  Dunit = g/cm3
  Dvalue = 19.84
  Group = -> [Pu_element002]
  conduct = 2
  density = 1
  expand = 3
  formula = Pu
  name = G4_Pu
  specific = 4
FEATURE [App::DocumentObjectGroupPython] Am_element001  label="Am_element : 1"  # scripted group (container) (typed FeaturePython)
  n = 1
  ref = Am_element
FEATURE [App::DocumentObjectGroupPython] G4_Am  # scripted group (container) (typed FeaturePython)
  Dunit = g/cm3
  Dvalue = 13.67
  Group = -> [Am_element001]
  conduct = 2
  density = 1
  expand = 3
  formula = Am
  name = G4_Am
  specific = 4
FEATURE [App::DocumentObjectGroupPython] Cm_element001  label="Cm_element : 1"  # scripted group (container) (typed FeaturePython)
  n = 1
  ref = Cm_element
FEATURE [App::DocumentObjectGroupPython] G4_Cm  # scripted group (container) (typed FeaturePython)
  Dunit = g/cm3
  Dvalue = 13.51
  Group = -> [Cm_element001]
  conduct = 2
  density = 1
  expand = 3
  formula = Cm
  name = G4_Cm
  specific = 4
FEATURE [App::DocumentObjectGroupPython] Bk_element001  label="Bk_element : 1"  # scripted group (container) (typed FeaturePython)
  n = 1
  ref = Bk_element
FEATURE [App::DocumentObjectGroupPython] G4_Bk  # scripted group (container) (typed FeaturePython)
  Dunit = g/cm3
  Dvalue = 14
  Group = -> [Bk_element001]
  conduct = 2
  density = 1
  expand = 3
  formula = Bk
  name = G4_Bk
  specific = 4
FEATURE [App::DocumentObjectGroupPython] Cf_element001  label="Cf_element : 1"  # scripted group (container) (typed FeaturePython)
  n = 1
  ref = Cf_element
FEATURE [App::DocumentObjectGroupPython] G4_Cf  # scripted group (container) (typed FeaturePython)
  Dunit = g/cm3
  Dvalue = 10
  Group = -> [Cf_element001]
  conduct = 2
  density = 1
  expand = 3
  formula = Cf
  name = G4_Cf
  specific = 4
FEATURE [App::DocumentObjectGroupPython] Element  # scripted group (container) (typed FeaturePython)
  Group = -> [G4_H,G4_He,G4_Li,G4_Be,G4_B,G4_C,G4_N,G4_O,G4_F,G4_Ne,G4_Na,G4_Mg,G4_Al,G4_Si,G4_P,G4_S,G4_Cl,G4_Ar,G4_K,G4_Ca,G4_Sc,G4_Ti,G4_V,G4_Cr,G4_Mn,G4_Fe,G4_Co,G4_Ni,G4_Cu,G4_Zn,G4_Ga,G4_Ge,G4_As,G4_Se,G4_Br,G4_Kr,G4_Rb,G4_Sr,G4_Y,G4_Zr,G4_Nb,G4_Mo,G4_Tc,G4_Ru,G4_Rh,G4_Pd,G4_Ag,G4_Cd,G4_In,G4_Sn,G4_Sb,G4_Te,G4_I,G4_Xe,G4_Cs,G4_Ba,G4_La,G4_Ce,G4_Pr,G4_Nd,G4_Pm,G4_Sm,G4_Eu,G4_Gd,G4_Tb,G4_Dy,G4_Ho,G4_Er,+30 more]
FEATURE [App::DocumentObjectGroupPython] H_element114  label="H_element : 063"  # scripted group (container) (typed FeaturePython)
  n = 2
  ref = H_element
FEATURE [App::DocumentObjectGroupPython] G4_lH2  # scripted group (container) (typed FeaturePython)
  Dunit = g/cm3
  Dvalue = 0.0708
  Group = -> [H_element114]
  conduct = 2
  density = 1
  expand = 3
  formula = G4_lH2
  name = G4_lH2
  specific = 4
FEATURE [App::DocumentObjectGroupPython] N_element049  label="N_element : 022"  # scripted group (container) (typed FeaturePython)
  n = 2
  ref = N_element
FEATURE [App::DocumentObjectGroupPython] G4_lN2  # scripted group (container) (typed FeaturePython)
  Dunit = g/cm3
  Dvalue = 0.807
  Group = -> [N_element049]
  conduct = 2
  density = 1
  expand = 3
  formula = G4_lN2
  name = G4_lN2
  specific = 4
FEATURE [App::DocumentObjectGroupPython] O_element106  label="O_element : 060"  # scripted group (container) (typed FeaturePython)
  n = 2
  ref = O_element
FEATURE [App::DocumentObjectGroupPython] G4_lO2  # scripted group (container) (typed FeaturePython)
  Dunit = g/cm3
  Dvalue = 1.141
  Group = -> [O_element106]
  conduct = 2
  density = 1
  expand = 3
  formula = G4_lO2
  name = G4_lO2
  specific = 4
FEATURE [App::DocumentObjectGroupPython] Ar_element003  label="Ar_element : 002"  # scripted group (container) (typed FeaturePython)
  n = 1
  ref = Ar_element
FEATURE [App::DocumentObjectGroupPython] G4_lAr  # scripted group (container) (typed FeaturePython)
  Dunit = g/cm3
  Dvalue = 1.396
  Group = -> [Ar_element003]
  conduct = 2
  density = 1
  expand = 3
  formula = G4_lAr
  name = G4_lAr
  specific = 4
FEATURE [App::DocumentObjectGroupPython] Br_element008  label="Br_element : 005"  # scripted group (container) (typed FeaturePython)
  n = 1
  ref = Br_element
FEATURE [App::DocumentObjectGroupPython] G4_lBr  # scripted group (container) (typed FeaturePython)
  Dunit = g/cm3
  Dvalue = 3.1028
  Group = -> [Br_element008]
  conduct = 2
  density = 1
  expand = 3
  formula = G4_lBr
  name = G4_lBr
  specific = 4
FEATURE [App::DocumentObjectGroupPython] Kr_element002  label="Kr_element : 002"  # scripted group (container) (typed FeaturePython)
  n = 1
  ref = Kr_element
FEATURE [App::DocumentObjectGroupPython] G4_lKr  # scripted group (container) (typed FeaturePython)
  Dunit = g/cm3
  Dvalue = 2.418
  Group = -> [Kr_element002]
  conduct = 2
  density = 1
  expand = 3
  formula = G4_lKr
  name = G4_lKr
  specific = 4
FEATURE [App::DocumentObjectGroupPython] Xe_element002  label="Xe_element : 002"  # scripted group (container) (typed FeaturePython)
  n = 1
  ref = Xe_element
FEATURE [App::DocumentObjectGroupPython] G4_lXe  # scripted group (container) (typed FeaturePython)
  Dunit = g/cm3
  Dvalue = 2.953
  Group = -> [Xe_element002]
  conduct = 2
  density = 1
  expand = 3
  formula = G4_lXe
  name = G4_lXe
  specific = 4
FEATURE [App::DocumentObjectGroupPython] O_element107  label="O_element : 061"  # scripted group (container) (typed FeaturePython)
  n = 4
  ref = O_element
FEATURE [App::DocumentObjectGroupPython] Pb_element004  label="Pb_element : 002"  # scripted group (container) (typed FeaturePython)
  n = 1
  ref = Pb_element
FEATURE [App::DocumentObjectGroupPython] W_element005  label="W_element : 005"  # scripted group (container) (typed FeaturePython)
  n = 1
  ref = W_element
FEATURE [App::DocumentObjectGroupPython] G4_PbWO4  # scripted group (container) (typed FeaturePython)
  Dunit = g/cm3
  Dvalue = 8.28
  Group = -> [O_element107,Pb_element004,W_element005]
  conduct = 2
  density = 1
  expand = 3
  formula = G4_PbWO4
  name = G4_PbWO4
  specific = 4
FEATURE [App::DocumentObjectGroupPython] H_element115  label="H_element : 064"  # scripted group (container) (typed FeaturePython)
  n = 1
  ref = H_element
FEATURE [App::DocumentObjectGroupPython] G4_Galactic  # scripted group (container) (typed FeaturePython)
  Dunit = g/cm3
  Dvalue = 0
  Group = -> [H_element115]
  conduct = 2
  density = 1
  expand = 3
  formula = G4_Galactic
  name = G4_Galactic
  specific = 4
FEATURE [App::DocumentObjectGroupPython] C_element125  label="C_element : 071"  # scripted group (container) (typed FeaturePython)
  n = 1
  ref = C_element
FEATURE [App::DocumentObjectGroupPython] G4_GRAPHITE_POROUS  # scripted group (container) (typed FeaturePython)
  Dunit = g/cm3
  Dvalue = 1.7
  Group = -> [C_element125]
  conduct = 2
  density = 1
  expand = 3
  formula = G4_GRAPHITE_POROUS
  name = G4_GRAPHITE_POROUS
  specific = 4
FEATURE [App::DocumentObjectGroupPython] H_element116  label="H_element : 0.150"  # scripted group (container) (typed FeaturePython)
  n = 0.080538
FEATURE [App::DocumentObjectGroupPython] C_element126  label="C_element : 0.600"  # scripted group (container) (typed FeaturePython)
  n = 0.599848
FEATURE [App::DocumentObjectGroupPython] O_element108  label="O_element : 0.320"  # scripted group (container) (typed FeaturePython)
  n = 0.319614
FEATURE [App::DocumentObjectGroupPython] G4_LUCITE  # scripted group (container) (typed FeaturePython)
  Dunit = g/cm3
  Dvalue = 1.19
  Group = -> [H_element116,C_element126,O_element108]
  conduct = 2
  density = 1
  expand = 3
  formula = G4_LUCITE
  name = G4_LUCITE
  specific = 4
FEATURE [App::DocumentObjectGroupPython] Cu_element002  label="Cu_element : 62"  # scripted group (container) (typed FeaturePython)
  n = 62
  ref = Cu_element
FEATURE [App::DocumentObjectGroupPython] Zn_element002  label="Zn_element : 35"  # scripted group (container) (typed FeaturePython)
  n = 35
  ref = Zn_element
FEATURE [App::DocumentObjectGroupPython] Pb_element005  label="Pb_element : 3"  # scripted group (container) (typed FeaturePython)
  n = 3
  ref = Pb_element
FEATURE [App::DocumentObjectGroupPython] G4_BRASS  # scripted group (container) (typed FeaturePython)
  Dunit = g/cm3
  Dvalue = 8.52
  Group = -> [Cu_element002,Zn_element002,Pb_element005]
  conduct = 2
  density = 1
  expand = 3
  formula = G4_BRASS
  name = G4_BRASS
  specific = 4
FEATURE [App::DocumentObjectGroupPython] Cu_element003  label="Cu_element : 89"  # scripted group (container) (typed FeaturePython)
  n = 89
  ref = Cu_element
FEATURE [App::DocumentObjectGroupPython] Zn_element003  label="Zn_element : 9"  # scripted group (container) (typed FeaturePython)
  n = 9
  ref = Zn_element
FEATURE [App::DocumentObjectGroupPython] Pb_element006  label="Pb_element : 2"  # scripted group (container) (typed FeaturePython)
  n = 2
  ref = Pb_element
FEATURE [App::DocumentObjectGroupPython] G4_BRONZE  # scripted group (container) (typed FeaturePython)
  Dunit = g/cm3
  Dvalue = 8.82
  Group = -> [Cu_element003,Zn_element003,Pb_element006]
  conduct = 2
  density = 1
  expand = 3
  formula = G4_BRONZE
  name = G4_BRONZE
  specific = 4
FEATURE [App::DocumentObjectGroupPython] Fe_element008  label="Fe_element : 74"  # scripted group (container) (typed FeaturePython)
  n = 74
  ref = Fe_element
FEATURE [App::DocumentObjectGroupPython] Cr_element002  label="Cr_element : 18"  # scripted group (container) (typed FeaturePython)
  n = 18
  ref = Cr_element
FEATURE [App::DocumentObjectGroupPython] Ni_element002  label="Ni_element : 8"  # scripted group (container) (typed FeaturePython)
  n = 8
  ref = Ni_element
FEATURE [App::DocumentObjectGroupPython] G4_STAINLESS_STEEL  label="G4_STAINLESS-STEEL"  # scripted group (container) (typed FeaturePython)
  Dunit = g/cm3
  Dvalue = 8
  Group = -> [Fe_element008,Cr_element002,Ni_element002]
  conduct = 2
  density = 1
  expand = 3
  formula = G4_STAINLESS-STEEL
  name = G4_STAINLESS-STEEL
  specific = 4
FEATURE [App::DocumentObjectGroupPython] H_element117  label="H_element : 065"  # scripted group (container) (typed FeaturePython)
  n = 18
  ref = H_element
FEATURE [App::DocumentObjectGroupPython] C_element127  label="C_element : 072"  # scripted group (container) (typed FeaturePython)
  n = 12
  ref = C_element
FEATURE [App::DocumentObjectGroupPython] O_element109  label="O_element : 062"  # scripted group (container) (typed FeaturePython)
  n = 7
  ref = O_element
FEATURE [App::DocumentObjectGroupPython] G4_CR39  # scripted group (container) (typed FeaturePython)
  Dunit = g/cm3
  Dvalue = 1.32
  Group = -> [H_element117,C_element127,O_element109]
  conduct = 2
  density = 1
  expand = 3
  formula = G4_CR39
  name = G4_CR39
  specific = 4
FEATURE [App::DocumentObjectGroupPython] H_element118  label="H_element : 38"  # scripted group (container) (typed FeaturePython)
  n = 38
  ref = H_element
FEATURE [App::DocumentObjectGroupPython] C_element128  label="C_element : 073"  # scripted group (container) (typed FeaturePython)
  n = 18
  ref = C_element
FEATURE [App::DocumentObjectGroupPython] O_element110  label="O_element : 063"  # scripted group (container) (typed FeaturePython)
  n = 1
  ref = O_element
FEATURE [App::DocumentObjectGroupPython] G4_OCTADECANOL  # scripted group (container) (typed FeaturePython)
  Dunit = g/cm3
  Dvalue = 0.812
  Group = -> [H_element118,C_element128,O_element110]
  conduct = 2
  density = 1
  expand = 3
  formula = G4_OCTADECANOL
  name = G4_OCTADECANOL
  specific = 4
FEATURE [App::DocumentObjectGroupPython] HEP  # scripted group (container) (typed FeaturePython)
  Group = -> [G4_lH2,G4_lN2,G4_lO2,G4_lAr,G4_lBr,G4_lKr,G4_lXe,G4_PbWO4,G4_Galactic,G4_GRAPHITE_POROUS,G4_LUCITE,G4_BRASS,G4_BRONZE,G4_STAINLESS_STEEL,G4_CR39,G4_OCTADECANOL]
FEATURE [App::DocumentObjectGroupPython] C_element129  label="C_element : 074"  # scripted group (container) (typed FeaturePython)
  n = 14
  ref = C_element
FEATURE [App::DocumentObjectGroupPython] H_element119  label="H_element : 066"  # scripted group (container) (typed FeaturePython)
  n = 10
  ref = H_element
FEATURE [App::DocumentObjectGroupPython] O_element111  label="O_element : 064"  # scripted group (container) (typed FeaturePython)
  n = 2
  ref = O_element
FEATURE [App::DocumentObjectGroupPython] N_element050  label="N_element : 023"  # scripted group (container) (typed FeaturePython)
  n = 2
  ref = N_element
FEATURE [App::DocumentObjectGroupPython] G4_KEVLAR  # scripted group (container) (typed FeaturePython)
  Dunit = g/cm3
  Dvalue = 1.44
  Group = -> [C_element129,H_element119,O_element111,N_element050]
  conduct = 2
  density = 1
  expand = 3
  formula = G4_KEVLAR
  name = G4_KEVLAR
  specific = 4
FEATURE [App::DocumentObjectGroupPython] C_element130  label="C_element : 075"  # scripted group (container) (typed FeaturePython)
  n = 10
  ref = C_element
FEATURE [App::DocumentObjectGroupPython] H_element120  label="H_element : 067"  # scripted group (container) (typed FeaturePython)
  n = 8
  ref = H_element
FEATURE [App::DocumentObjectGroupPython] O_element112  label="O_element : 065"  # scripted group (container) (typed FeaturePython)
  n = 4
  ref = O_element
FEATURE [App::DocumentObjectGroupPython] G4_DACRON  # scripted group (container) (typed FeaturePython)
  Dunit = g/cm3
  Dvalue = 1.4
  Group = -> [C_element130,H_element120,O_element112]
  conduct = 2
  density = 1
  expand = 3
  formula = G4_DACRON
  name = G4_DACRON
  specific = 4
FEATURE [App::DocumentObjectGroupPython] C_element131  label="C_element : 076"  # scripted group (container) (typed FeaturePython)
  n = 4
  ref = C_element
FEATURE [App::DocumentObjectGroupPython] H_element121  label="H_element : 068"  # scripted group (container) (typed FeaturePython)
  n = 5
  ref = H_element
FEATURE [App::DocumentObjectGroupPython] Cl_element030  label="Cl_element : 016"  # scripted group (container) (typed FeaturePython)
  n = 1
  ref = Cl_element
FEATURE [App::DocumentObjectGroupPython] G4_NEOPRENE  # scripted group (container) (typed FeaturePython)
  Dunit = g/cm3
  Dvalue = 1.23
  Group = -> [C_element131,H_element121,Cl_element030]
  conduct = 2
  density = 1
  expand = 3
  formula = G4_NEOPRENE
  name = G4_NEOPRENE
  specific = 4
FEATURE [App::DocumentObjectGroupPython] Space  # scripted group (container) (typed FeaturePython)
  Group = -> [G4_KEVLAR,G4_DACRON,G4_NEOPRENE]
FEATURE [App::DocumentObjectGroupPython] H_element122  label="H_element : 069"  # scripted group (container) (typed FeaturePython)
  n = 5
  ref = H_element
FEATURE [App::DocumentObjectGroupPython] C_element132  label="C_element : 077"  # scripted group (container) (typed FeaturePython)
  n = 4
  ref = C_element
FEATURE [App::DocumentObjectGroupPython] N_element051  label="N_element : 3"  # scripted group (container) (typed FeaturePython)
  n = 3
  ref = N_element
FEATURE [App::DocumentObjectGroupPython] O_element113  label="O_element : 066"  # scripted group (container) (typed FeaturePython)
  n = 1
  ref = O_element
FEATURE [App::DocumentObjectGroupPython] G4_CYTOSINE  # scripted group (container) (typed FeaturePython)
  Dunit = g/cm3
  Dvalue = 1.55
  Group = -> [H_element122,C_element132,N_element051,O_element113]
  conduct = 2
  density = 1
  expand = 3
  formula = G4_CYTOSINE
  name = G4_CYTOSINE
  specific = 4
FEATURE [App::DocumentObjectGroupPython] H_element123  label="H_element : 070"  # scripted group (container) (typed FeaturePython)
  n = 6
  ref = H_element
FEATURE [App::DocumentObjectGroupPython] C_element133  label="C_element : 078"  # scripted group (container) (typed FeaturePython)
  n = 5
  ref = C_element
FEATURE [App::DocumentObjectGroupPython] N_element052  label="N_element : 024"  # scripted group (container) (typed FeaturePython)
  n = 2
  ref = N_element
FEATURE [App::DocumentObjectGroupPython] O_element114  label="O_element : 067"  # scripted group (container) (typed FeaturePython)
  n = 2
  ref = O_element
FEATURE [App::DocumentObjectGroupPython] G4_THYMINE  # scripted group (container) (typed FeaturePython)
  Dunit = g/cm3
  Dvalue = 1.23
  Group = -> [H_element123,C_element133,N_element052,O_element114]
  conduct = 2
  density = 1
  expand = 3
  formula = G4_THYMINE
  name = G4_THYMINE
  specific = 4
FEATURE [App::DocumentObjectGroupPython] H_element124  label="H_element : 071"  # scripted group (container) (typed FeaturePython)
  n = 4
  ref = H_element
FEATURE [App::DocumentObjectGroupPython] C_element134  label="C_element : 079"  # scripted group (container) (typed FeaturePython)
  n = 4
  ref = C_element
FEATURE [App::DocumentObjectGroupPython] N_element053  label="N_element : 025"  # scripted group (container) (typed FeaturePython)
  n = 2
  ref = N_element
FEATURE [App::DocumentObjectGroupPython] O_element115  label="O_element : 068"  # scripted group (container) (typed FeaturePython)
  n = 2
  ref = O_element
FEATURE [App::DocumentObjectGroupPython] G4_URACIL  # scripted group (container) (typed FeaturePython)
  Dunit = g/cm3
  Dvalue = 1.32
  Group = -> [H_element124,C_element134,N_element053,O_element115]
  conduct = 2
  density = 1
  expand = 3
  formula = G4_URACIL
  name = G4_URACIL
  specific = 4
FEATURE [App::DocumentObjectGroupPython] H_element125  label="H_element : 072"  # scripted group (container) (typed FeaturePython)
  n = 4
  ref = H_element
FEATURE [App::DocumentObjectGroupPython] C_element135  label="C_element : 080"  # scripted group (container) (typed FeaturePython)
  n = 5
  ref = C_element
FEATURE [App::DocumentObjectGroupPython] N_element054  label="N_element : 026"  # scripted group (container) (typed FeaturePython)
  n = 5
  ref = N_element
FEATURE [App::DocumentObjectGroupPython] G4_DNA_ADENINE  # scripted group (container) (typed FeaturePython)
  Dunit = g/cm3
  Dvalue = 1
  Group = -> [H_element125,C_element135,N_element054]
  conduct = 2
  density = 1
  expand = 3
  formula = G4_DNA_ADENINE
  name = G4_DNA_ADENINE
  specific = 4
FEATURE [App::DocumentObjectGroupPython] H_element126  label="H_element : 073"  # scripted group (container) (typed FeaturePython)
  n = 4
  ref = H_element
FEATURE [App::DocumentObjectGroupPython] C_element136  label="C_element : 081"  # scripted group (container) (typed FeaturePython)
  n = 5
  ref = C_element
FEATURE [App::DocumentObjectGroupPython] N_element055  label="N_element : 027"  # scripted group (container) (typed FeaturePython)
  n = 5
  ref = N_element
FEATURE [App::DocumentObjectGroupPython] O_element116  label="O_element : 069"  # scripted group (container) (typed FeaturePython)
  n = 1
  ref = O_element
FEATURE [App::DocumentObjectGroupPython] G4_DNA_GUANINE  # scripted group (container) (typed FeaturePython)
  Dunit = g/cm3
  Dvalue = 1
  Group = -> [H_element126,C_element136,N_element055,O_element116]
  conduct = 2
  density = 1
  expand = 3
  formula = G4_DNA_GUANINE
  name = G4_DNA_GUANINE
  specific = 4
FEATURE [App::DocumentObjectGroupPython] H_element127  label="H_element : 074"  # scripted group (container) (typed FeaturePython)
  n = 4
  ref = H_element
FEATURE [App::DocumentObjectGroupPython] C_element137  label="C_element : 082"  # scripted group (container) (typed FeaturePython)
  n = 4
  ref = C_element
FEATURE [App::DocumentObjectGroupPython] N_element056  label="N_element : 028"  # scripted group (container) (typed FeaturePython)
  n = 3
  ref = N_element
FEATURE [App::DocumentObjectGroupPython] O_element117  label="O_element : 070"  # scripted group (container) (typed FeaturePython)
  n = 1
  ref = O_element
FEATURE [App::DocumentObjectGroupPython] G4_DNA_CYTOSINE  # scripted group (container) (typed FeaturePython)
  Dunit = g/cm3
  Dvalue = 1
  Group = -> [H_element127,C_element137,N_element056,O_element117]
  conduct = 2
  density = 1
  expand = 3
  formula = G4_DNA_CYTOSINE
  name = G4_DNA_CYTOSINE
  specific = 4
FEATURE [App::DocumentObjectGroupPython] H_element128  label="H_element : 075"  # scripted group (container) (typed FeaturePython)
  n = 5
  ref = H_element
FEATURE [App::DocumentObjectGroupPython] C_element138  label="C_element : 083"  # scripted group (container) (typed FeaturePython)
  n = 5
  ref = C_element
FEATURE [App::DocumentObjectGroupPython] N_element057  label="N_element : 029"  # scripted group (container) (typed FeaturePython)
  n = 2
  ref = N_element
FEATURE [App::DocumentObjectGroupPython] O_element118  label="O_element : 071"  # scripted group (container) (typed FeaturePython)
  n = 2
  ref = O_element
FEATURE [App::DocumentObjectGroupPython] G4_DNA_THYMINE  # scripted group (container) (typed FeaturePython)
  Dunit = g/cm3
  Dvalue = 1
  Group = -> [H_element128,C_element138,N_element057,O_element118]
  conduct = 2
  density = 1
  expand = 3
  formula = G4_DNA_THYMINE
  name = G4_DNA_THYMINE
  specific = 4
FEATURE [App::DocumentObjectGroupPython] H_element129  label="H_element : 076"  # scripted group (container) (typed FeaturePython)
  n = 3
  ref = H_element
FEATURE [App::DocumentObjectGroupPython] C_element139  label="C_element : 084"  # scripted group (container) (typed FeaturePython)
  n = 4
  ref = C_element
FEATURE [App::DocumentObjectGroupPython] N_element058  label="N_element : 030"  # scripted group (container) (typed FeaturePython)
  n = 2
  ref = N_element
FEATURE [App::DocumentObjectGroupPython] O_element119  label="O_element : 072"  # scripted group (container) (typed FeaturePython)
  n = 2
  ref = O_element
FEATURE [App::DocumentObjectGroupPython] G4_DNA_URACIL  # scripted group (container) (typed FeaturePython)
  Dunit = g/cm3
  Dvalue = 1
  Group = -> [H_element129,C_element139,N_element058,O_element119]
  conduct = 2
  density = 1
  expand = 3
  formula = G4_DNA_URACIL
  name = G4_DNA_URACIL
  specific = 4
FEATURE [App::DocumentObjectGroupPython] H_element130  label="H_element : 077"  # scripted group (container) (typed FeaturePython)
  n = 10
  ref = H_element
FEATURE [App::DocumentObjectGroupPython] C_element140  label="C_element : 085"  # scripted group (container) (typed FeaturePython)
  n = 10
  ref = C_element
FEATURE [App::DocumentObjectGroupPython] N_element059  label="N_element : 031"  # scripted group (container) (typed FeaturePython)
  n = 5
  ref = N_element
FEATURE [App::DocumentObjectGroupPython] O_element120  label="O_element : 073"  # scripted group (container) (typed FeaturePython)
  n = 4
  ref = O_element
FEATURE [App::DocumentObjectGroupPython] G4_DNA_ADENOSINE  # scripted group (container) (typed FeaturePython)
  Dunit = g/cm3
  Dvalue = 1
  Group = -> [H_element130,C_element140,N_element059,O_element120]
  conduct = 2
  density = 1
  expand = 3
  formula = G4_DNA_ADENOSINE
  name = G4_DNA_ADENOSINE
  specific = 4
FEATURE [App::DocumentObjectGroupPython] H_element131  label="H_element : 078"  # scripted group (container) (typed FeaturePython)
  n = 10
  ref = H_element
FEATURE [App::DocumentObjectGroupPython] C_element141  label="C_element : 086"  # scripted group (container) (typed FeaturePython)
  n = 10
  ref = C_element
FEATURE [App::DocumentObjectGroupPython] N_element060  label="N_element : 032"  # scripted group (container) (typed FeaturePython)
  n = 5
  ref = N_element
FEATURE [App::DocumentObjectGroupPython] O_element121  label="O_element : 074"  # scripted group (container) (typed FeaturePython)
  n = 5
  ref = O_element
FEATURE [App::DocumentObjectGroupPython] G4_DNA_GUANOSINE  # scripted group (container) (typed FeaturePython)
  Dunit = g/cm3
  Dvalue = 1
  Group = -> [H_element131,C_element141,N_element060,O_element121]
  conduct = 2
  density = 1
  expand = 3
  formula = G4_DNA_GUANOSINE
  name = G4_DNA_GUANOSINE
  specific = 4
FEATURE [App::DocumentObjectGroupPython] H_element132  label="H_element : 079"  # scripted group (container) (typed FeaturePython)
  n = 10
  ref = H_element
FEATURE [App::DocumentObjectGroupPython] C_element142  label="C_element : 087"  # scripted group (container) (typed FeaturePython)
  n = 9
  ref = C_element
FEATURE [App::DocumentObjectGroupPython] N_element061  label="N_element : 033"  # scripted group (container) (typed FeaturePython)
  n = 3
  ref = N_element
FEATURE [App::DocumentObjectGroupPython] O_element122  label="O_element : 075"  # scripted group (container) (typed FeaturePython)
  n = 5
  ref = O_element
FEATURE [App::DocumentObjectGroupPython] G4_DNA_CYTIDINE  # scripted group (container) (typed FeaturePython)
  Dunit = g/cm3
  Dvalue = 1
  Group = -> [H_element132,C_element142,N_element061,O_element122]
  conduct = 2
  density = 1
  expand = 3
  formula = G4_DNA_CYTIDINE
  name = G4_DNA_CYTIDINE
  specific = 4
FEATURE [App::DocumentObjectGroupPython] H_element133  label="H_element : 080"  # scripted group (container) (typed FeaturePython)
  n = 9
  ref = H_element
FEATURE [App::DocumentObjectGroupPython] C_element143  label="C_element : 088"  # scripted group (container) (typed FeaturePython)
  n = 9
  ref = C_element
FEATURE [App::DocumentObjectGroupPython] N_element062  label="N_element : 034"  # scripted group (container) (typed FeaturePython)
  n = 2
  ref = N_element
FEATURE [App::DocumentObjectGroupPython] O_element123  label="O_element : 076"  # scripted group (container) (typed FeaturePython)
  n = 6
  ref = O_element
FEATURE [App::DocumentObjectGroupPython] G4_DNA_URIDINE  # scripted group (container) (typed FeaturePython)
  Dunit = g/cm3
  Dvalue = 1
  Group = -> [H_element133,C_element143,N_element062,O_element123]
  conduct = 2
  density = 1
  expand = 3
  formula = G4_DNA_URIDINE
  name = G4_DNA_URIDINE
  specific = 4
FEATURE [App::DocumentObjectGroupPython] H_element134  label="H_element : 081"  # scripted group (container) (typed FeaturePython)
  n = 11
  ref = H_element
FEATURE [App::DocumentObjectGroupPython] C_element144  label="C_element : 089"  # scripted group (container) (typed FeaturePython)
  n = 10
  ref = C_element
FEATURE [App::DocumentObjectGroupPython] N_element063  label="N_element : 035"  # scripted group (container) (typed FeaturePython)
  n = 2
  ref = N_element
FEATURE [App::DocumentObjectGroupPython] O_element124  label="O_element : 077"  # scripted group (container) (typed FeaturePython)
  n = 6
  ref = O_element
FEATURE [App::DocumentObjectGroupPython] G4_DNA_METHYLURIDINE  # scripted group (container) (typed FeaturePython)
  Dunit = g/cm3
  Dvalue = 1
  Group = -> [H_element134,C_element144,N_element063,O_element124]
  conduct = 2
  density = 1
  expand = 3
  formula = G4_DNA_METHYLURIDINE
  name = G4_DNA_METHYLURIDINE
  specific = 4
FEATURE [App::DocumentObjectGroupPython] P_element014  label="P_element : 003"  # scripted group (container) (typed FeaturePython)
  n = 1
  ref = P_element
FEATURE [App::DocumentObjectGroupPython] O_element125  label="O_element : 078"  # scripted group (container) (typed FeaturePython)
  n = 3
  ref = O_element
FEATURE [App::DocumentObjectGroupPython] G4_DNA_MONOPHOSPHATE  # scripted group (container) (typed FeaturePython)
  Dunit = g/cm3
  Dvalue = 1
  Group = -> [P_element014,O_element125]
  conduct = 2
  density = 1
  expand = 3
  formula = G4_DNA_MONOPHOSPHATE
  name = G4_DNA_MONOPHOSPHATE
  specific = 4
FEATURE [App::DocumentObjectGroupPython] H_element135  label="H_element : 082"  # scripted group (container) (typed FeaturePython)
  n = 10
  ref = H_element
FEATURE [App::DocumentObjectGroupPython] C_element145  label="C_element : 090"  # scripted group (container) (typed FeaturePython)
  n = 10
  ref = C_element
FEATURE [App::DocumentObjectGroupPython] N_element064  label="N_element : 036"  # scripted group (container) (typed FeaturePython)
  n = 5
  ref = N_element
FEATURE [App::DocumentObjectGroupPython] O_element126  label="O_element : 079"  # scripted group (container) (typed FeaturePython)
  n = 7
  ref = O_element
FEATURE [App::DocumentObjectGroupPython] P_element015  label="P_element : 004"  # scripted group (container) (typed FeaturePython)
  n = 1
  ref = P_element
FEATURE [App::DocumentObjectGroupPython] G4_DNA_A  # scripted group (container) (typed FeaturePython)
  Dunit = g/cm3
  Dvalue = 1
  Group = -> [H_element135,C_element145,N_element064,O_element126,P_element015]
  conduct = 2
  density = 1
  expand = 3
  formula = G4_DNA_A
  name = G4_DNA_A
  specific = 4
FEATURE [App::DocumentObjectGroupPython] H_element136  label="H_element : 083"  # scripted group (container) (typed FeaturePython)
  n = 10
  ref = H_element
FEATURE [App::DocumentObjectGroupPython] C_element146  label="C_element : 091"  # scripted group (container) (typed FeaturePython)
  n = 10
  ref = C_element
FEATURE [App::DocumentObjectGroupPython] N_element065  label="N_element : 037"  # scripted group (container) (typed FeaturePython)
  n = 5
  ref = N_element
FEATURE [App::DocumentObjectGroupPython] O_element127  label="O_element : 8"  # scripted group (container) (typed FeaturePython)
  n = 8
  ref = O_element
FEATURE [App::DocumentObjectGroupPython] P_element016  label="P_element : 005"  # scripted group (container) (typed FeaturePython)
  n = 1
  ref = P_element
FEATURE [App::DocumentObjectGroupPython] G4_DNA_G  # scripted group (container) (typed FeaturePython)
  Dunit = g/cm3
  Dvalue = 1
  Group = -> [H_element136,C_element146,N_element065,O_element127,P_element016]
  conduct = 2
  density = 1
  expand = 3
  formula = G4_DNA_G
  name = G4_DNA_G
  specific = 4
FEATURE [App::DocumentObjectGroupPython] H_element137  label="H_element : 084"  # scripted group (container) (typed FeaturePython)
  n = 10
  ref = H_element
FEATURE [App::DocumentObjectGroupPython] C_element147  label="C_element : 092"  # scripted group (container) (typed FeaturePython)
  n = 9
  ref = C_element
FEATURE [App::DocumentObjectGroupPython] N_element066  label="N_element : 038"  # scripted group (container) (typed FeaturePython)
  n = 3
  ref = N_element
FEATURE [App::DocumentObjectGroupPython] O_element128  label="O_element : 080"  # scripted group (container) (typed FeaturePython)
  n = 8
  ref = O_element
FEATURE [App::DocumentObjectGroupPython] P_element017  label="P_element : 006"  # scripted group (container) (typed FeaturePython)
  n = 1
  ref = P_element
FEATURE [App::DocumentObjectGroupPython] G4_DNA_C  # scripted group (container) (typed FeaturePython)
  Dunit = g/cm3
  Dvalue = 1
  Group = -> [H_element137,C_element147,N_element066,O_element128,P_element017]
  conduct = 2
  density = 1
  expand = 3
  formula = G4_DNA_C
  name = G4_DNA_C
  specific = 4
FEATURE [App::DocumentObjectGroupPython] H_element138  label="H_element : 085"  # scripted group (container) (typed FeaturePython)
  n = 9
  ref = H_element
FEATURE [App::DocumentObjectGroupPython] C_element148  label="C_element : 093"  # scripted group (container) (typed FeaturePython)
  n = 9
  ref = C_element
FEATURE [App::DocumentObjectGroupPython] N_element067  label="N_element : 039"  # scripted group (container) (typed FeaturePython)
  n = 2
  ref = N_element
FEATURE [App::DocumentObjectGroupPython] O_element129  label="O_element : 9"  # scripted group (container) (typed FeaturePython)
  n = 9
  ref = O_element
FEATURE [App::DocumentObjectGroupPython] P_element018  label="P_element : 007"  # scripted group (container) (typed FeaturePython)
  n = 1
  ref = P_element
FEATURE [App::DocumentObjectGroupPython] G4_DNA_U  # scripted group (container) (typed FeaturePython)
  Dunit = g/cm3
  Dvalue = 1
  Group = -> [H_element138,C_element148,N_element067,O_element129,P_element018]
  conduct = 2
  density = 1
  expand = 3
  formula = G4_DNA_U
  name = G4_DNA_U
  specific = 4
FEATURE [App::DocumentObjectGroupPython] H_element139  label="H_element : 086"  # scripted group (container) (typed FeaturePython)
  n = 11
  ref = H_element
FEATURE [App::DocumentObjectGroupPython] C_element149  label="C_element : 094"  # scripted group (container) (typed FeaturePython)
  n = 10
  ref = C_element
FEATURE [App::DocumentObjectGroupPython] N_element068  label="N_element : 040"  # scripted group (container) (typed FeaturePython)
  n = 2
  ref = N_element
FEATURE [App::DocumentObjectGroupPython] O_element130  label="O_element : 081"  # scripted group (container) (typed FeaturePython)
  n = 9
  ref = O_element
FEATURE [App::DocumentObjectGroupPython] P_element019  label="P_element : 008"  # scripted group (container) (typed FeaturePython)
  n = 1
  ref = P_element
FEATURE [App::DocumentObjectGroupPython] G4_DNA_MU  # scripted group (container) (typed FeaturePython)
  Dunit = g/cm3
  Dvalue = 1
  Group = -> [H_element139,C_element149,N_element068,O_element130,P_element019]
  conduct = 2
  density = 1
  expand = 3
  formula = G4_DNA_MU
  name = G4_DNA_MU
  specific = 4
FEATURE [App::DocumentObjectGroupPython] BioChemical  # scripted group (container) (typed FeaturePython)
  Group = -> [G4_CYTOSINE,G4_THYMINE,G4_URACIL,G4_DNA_ADENINE,G4_DNA_GUANINE,G4_DNA_CYTOSINE,G4_DNA_THYMINE,G4_DNA_URACIL,G4_DNA_ADENOSINE,G4_DNA_GUANOSINE,G4_DNA_CYTIDINE,G4_DNA_URIDINE,G4_DNA_METHYLURIDINE,G4_DNA_MONOPHOSPHATE,G4_DNA_A,G4_DNA_G,G4_DNA_C,G4_DNA_U,G4_DNA_MU]
FEATURE [App::DocumentObjectGroupPython] G4Materials  # scripted group (container) (typed FeaturePython)
  Group = -> [NIST,Element,HEP,Space,BioChemical]
  version = 1
FEATURE [App::DocumentObjectGroupPython] Geant4  # scripted group (container) (typed FeaturePython)
  Group = -> [G4Isotopes,G4Elements,G4Materials]
FEATURE [App::DocumentObjectGroupPython] Materials  # scripted group (container) (typed FeaturePython)
  Group = -> [Geant4]
FEATURE [Part::FeaturePython] GDMLBox_WorldBox  # WARN: FeaturePython — macro-defined, semantics opaque (R4)
  lunit = 2
  material = 5
  x = 100
  y = 100
  z = 100
FEATURE [Part::FeaturePython] GDMLBox_Box  # WARN: FeaturePython — macro-defined, semantics opaque (R4)
  Placement = pos=(0,0,-5) rot=(0,0,1;0.523599rad)
  lunit = 2
  material = 0
  x = 10
  y = 10
  z = 10
FEATURE [Part::FeaturePython] GDMLTube  # WARN: FeaturePython — macro-defined, semantics opaque (R4)
  Placement = pos=(0,0,5) rot=(0,1,0;-0.523599rad)
  aunit = 1
  deltaphi = 360
  lunit = 2
  material = 0
  rmax = 3
  rmin = 0
  startphi = 0
  z = 20
FEATURE [Part::Fuse] Fuse
  Base = -> GDMLBox_Box
  Placement = pos=(-1.1021,1.1021,0.645598) rot=(0.678598,0.281085,0.678598;1.09606rad)
  Tool = -> GDMLTube
FEATURE [App::Part] Bool_Fuse
  Group = -> [GDMLBox_Box,GDMLTube,Fuse]
  Origin = -> Origin003
  Placement = pos=(20,0,6) rot=(1,0,0;1.5708rad)
FEATURE [App::Part] worldVOL
  Group = -> [GDMLBox_WorldBox,Bool_Fuse]
  Origin = -> Origin
